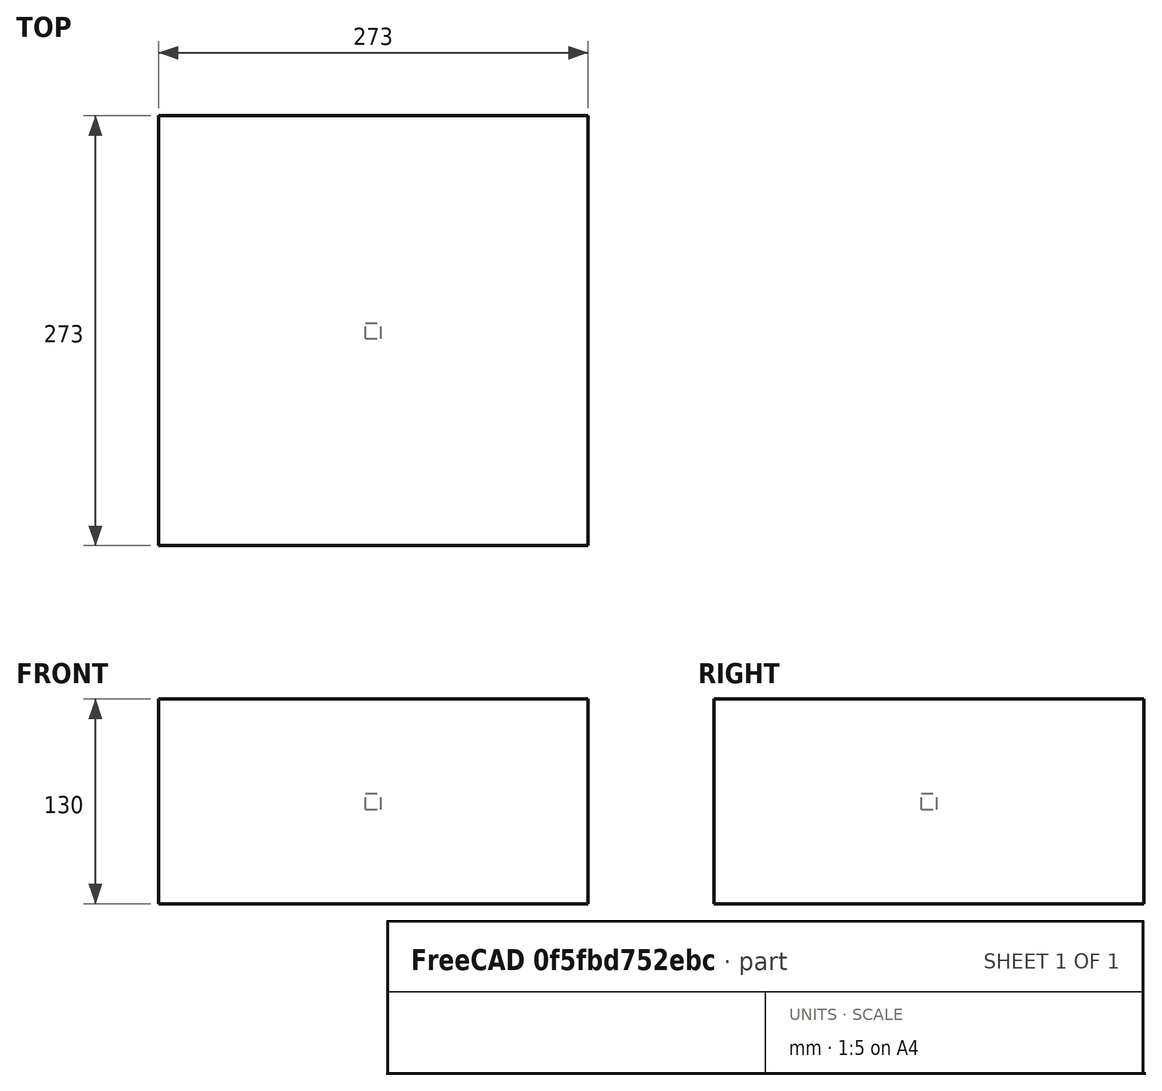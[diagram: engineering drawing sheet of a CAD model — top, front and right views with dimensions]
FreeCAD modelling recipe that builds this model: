
FCSTD DOCUMENT  (FreeCAD 0.20RUnknown)
Label: testExperiment
License: All rights reserved
LicenseURL: http://en.wikipedia.org/wiki/All_rights_reserved
objects: App::DocumentObjectGroupPython×1251, Part::FeaturePython×3, App::Part×2
note: 2 computed .brp shape members not serialized (recipe doc carries the construction recipe); baked Part::Feature solids carry a one-line shape summary decoded from their .brp

FEATURE [App::DocumentObjectGroupPython] HALFPI  # scripted group (container) (typed FeaturePython)
  name = HALFPI
  value = pi/2.
FEATURE [App::DocumentObjectGroupPython] PI  # scripted group (container) (typed FeaturePython)
  name = PI
  value = 1.*pi
FEATURE [App::DocumentObjectGroupPython] TWOPI  # scripted group (container) (typed FeaturePython)
  name = TWOPI
  value = 2.*pi
FEATURE [App::DocumentObjectGroupPython] Constants  # scripted group (container) (typed FeaturePython)
  Group = -> [HALFPI,PI,TWOPI]
FEATURE [App::DocumentObjectGroupPython] Variables  # scripted group (container) (typed FeaturePython)
FEATURE [App::DocumentObjectGroupPython] Quantities  # scripted group (container) (typed FeaturePython)
FEATURE [App::DocumentObjectGroupPython] Isotopes  # scripted group (container) (typed FeaturePython)
FEATURE [App::DocumentObjectGroupPython] Elements  # scripted group (container) (typed FeaturePython)
FEATURE [App::DocumentObjectGroupPython] Matrix  # scripted group (container) (typed FeaturePython)
FEATURE [App::DocumentObjectGroupPython] Surfaces  # scripted group (container) (typed FeaturePython)
FEATURE [App::DocumentObjectGroupPython] Opticals  # scripted group (container) (typed FeaturePython)
  Group = -> [Matrix,Surfaces]
FEATURE [App::DocumentObjectGroupPython] G4Isotopes  # scripted group (container) (typed FeaturePython)
FEATURE [App::DocumentObjectGroupPython] H_element  # scripted group (container) (typed FeaturePython)
  Z = 1
  atom_value = 1.008
  formula = H
  name = H_element
FEATURE [App::DocumentObjectGroupPython] He_element  # scripted group (container) (typed FeaturePython)
  Z = 2
  atom_value = 4.0026
  formula = He
  name = He_element
FEATURE [App::DocumentObjectGroupPython] Li_element  # scripted group (container) (typed FeaturePython)
  Z = 3
  atom_value = 6.94
  formula = Li
  name = Li_element
FEATURE [App::DocumentObjectGroupPython] Be_element  # scripted group (container) (typed FeaturePython)
  Z = 4
  atom_value = 9.01218
  formula = Be
  name = Be_element
FEATURE [App::DocumentObjectGroupPython] B_element  # scripted group (container) (typed FeaturePython)
  Z = 5
  atom_value = 10.81
  formula = B
  name = B_element
FEATURE [App::DocumentObjectGroupPython] C_element  # scripted group (container) (typed FeaturePython)
  Z = 6
  atom_value = 12.011
  formula = C
  name = C_element
FEATURE [App::DocumentObjectGroupPython] N_element  # scripted group (container) (typed FeaturePython)
  Z = 7
  atom_value = 14.007
  formula = N
  name = N_element
FEATURE [App::DocumentObjectGroupPython] O_element  # scripted group (container) (typed FeaturePython)
  Z = 8
  atom_value = 15.999
  formula = O
  name = O_element
FEATURE [App::DocumentObjectGroupPython] F_element  # scripted group (container) (typed FeaturePython)
  Z = 9
  atom_value = 18.9984
  formula = F
  name = F_element
FEATURE [App::DocumentObjectGroupPython] Ne_element  # scripted group (container) (typed FeaturePython)
  Z = 10
  atom_value = 20.1797
  formula = Ne
  name = Ne_element
FEATURE [App::DocumentObjectGroupPython] Na_element  # scripted group (container) (typed FeaturePython)
  Z = 11
  atom_value = 22.9898
  formula = Na
  name = Na_element
FEATURE [App::DocumentObjectGroupPython] Mg_element  # scripted group (container) (typed FeaturePython)
  Z = 12
  atom_value = 24.305
  formula = Mg
  name = Mg_element
FEATURE [App::DocumentObjectGroupPython] Al_element  # scripted group (container) (typed FeaturePython)
  Z = 13
  atom_value = 26.9815
  formula = Al
  name = Al_element
FEATURE [App::DocumentObjectGroupPython] Si_element  # scripted group (container) (typed FeaturePython)
  Z = 14
  atom_value = 28.085
  formula = Si
  name = Si_element
FEATURE [App::DocumentObjectGroupPython] P_element  # scripted group (container) (typed FeaturePython)
  Z = 15
  atom_value = 30.9738
  formula = P
  name = P_element
FEATURE [App::DocumentObjectGroupPython] S_element  # scripted group (container) (typed FeaturePython)
  Z = 16
  atom_value = 32.06
  formula = S
  name = S_element
FEATURE [App::DocumentObjectGroupPython] Cl_element  # scripted group (container) (typed FeaturePython)
  Z = 17
  atom_value = 35.45
  formula = Cl
  name = Cl_element
FEATURE [App::DocumentObjectGroupPython] Ar_element  # scripted group (container) (typed FeaturePython)
  Z = 18
  atom_value = 39.95
  formula = Ar
  name = Ar_element
FEATURE [App::DocumentObjectGroupPython] K_element  # scripted group (container) (typed FeaturePython)
  Z = 19
  atom_value = 39.0983
  formula = K
  name = K_element
FEATURE [App::DocumentObjectGroupPython] Ca_element  # scripted group (container) (typed FeaturePython)
  Z = 20
  atom_value = 40.078
  formula = Ca
  name = Ca_element
FEATURE [App::DocumentObjectGroupPython] Sc_element  # scripted group (container) (typed FeaturePython)
  Z = 21
  atom_value = 44.9559
  formula = Sc
  name = Sc_element
FEATURE [App::DocumentObjectGroupPython] Ti_element  # scripted group (container) (typed FeaturePython)
  Z = 22
  atom_value = 47.867
  formula = Ti
  name = Ti_element
FEATURE [App::DocumentObjectGroupPython] V_element  # scripted group (container) (typed FeaturePython)
  Z = 23
  atom_value = 50.9415
  formula = V
  name = V_element
FEATURE [App::DocumentObjectGroupPython] Cr_element  # scripted group (container) (typed FeaturePython)
  Z = 24
  atom_value = 51.9961
  formula = Cr
  name = Cr_element
FEATURE [App::DocumentObjectGroupPython] Mn_element  # scripted group (container) (typed FeaturePython)
  Z = 25
  atom_value = 54.938
  formula = Mn
  name = Mn_element
FEATURE [App::DocumentObjectGroupPython] Fe_element  # scripted group (container) (typed FeaturePython)
  Z = 26
  atom_value = 55.845
  formula = Fe
  name = Fe_element
FEATURE [App::DocumentObjectGroupPython] Co_element  # scripted group (container) (typed FeaturePython)
  Z = 27
  atom_value = 58.9332
  formula = Co
  name = Co_element
FEATURE [App::DocumentObjectGroupPython] Ni_element  # scripted group (container) (typed FeaturePython)
  Z = 28
  atom_value = 58.6934
  formula = Ni
  name = Ni_element
FEATURE [App::DocumentObjectGroupPython] Cu_element  # scripted group (container) (typed FeaturePython)
  Z = 29
  atom_value = 63.546
  formula = Cu
  name = Cu_element
FEATURE [App::DocumentObjectGroupPython] Zn_element  # scripted group (container) (typed FeaturePython)
  Z = 30
  atom_value = 65.38
  formula = Zn
  name = Zn_element
FEATURE [App::DocumentObjectGroupPython] Ga_element  # scripted group (container) (typed FeaturePython)
  Z = 31
  atom_value = 69.723
  formula = Ga
  name = Ga_element
FEATURE [App::DocumentObjectGroupPython] Ge_element  # scripted group (container) (typed FeaturePython)
  Z = 32
  atom_value = 72.63
  formula = Ge
  name = Ge_element
FEATURE [App::DocumentObjectGroupPython] As_element  # scripted group (container) (typed FeaturePython)
  Z = 33
  atom_value = 74.9216
  formula = As
  name = As_element
FEATURE [App::DocumentObjectGroupPython] Se_element  # scripted group (container) (typed FeaturePython)
  Z = 34
  atom_value = 78.971
  formula = Se
  name = Se_element
FEATURE [App::DocumentObjectGroupPython] Br_element  # scripted group (container) (typed FeaturePython)
  Z = 35
  atom_value = 79.904
  formula = Br
  name = Br_element
FEATURE [App::DocumentObjectGroupPython] Kr_element  # scripted group (container) (typed FeaturePython)
  Z = 36
  atom_value = 83.798
  formula = Kr
  name = Kr_element
FEATURE [App::DocumentObjectGroupPython] Rb_element  # scripted group (container) (typed FeaturePython)
  Z = 37
  atom_value = 85.4678
  formula = Rb
  name = Rb_element
FEATURE [App::DocumentObjectGroupPython] Sr_element  # scripted group (container) (typed FeaturePython)
  Z = 38
  atom_value = 87.62
  formula = Sr
  name = Sr_element
FEATURE [App::DocumentObjectGroupPython] Y_element  # scripted group (container) (typed FeaturePython)
  Z = 39
  atom_value = 88.9058
  formula = Y
  name = Y_element
FEATURE [App::DocumentObjectGroupPython] Zr_element  # scripted group (container) (typed FeaturePython)
  Z = 40
  atom_value = 91.224
  formula = Zr
  name = Zr_element
FEATURE [App::DocumentObjectGroupPython] Nb_element  # scripted group (container) (typed FeaturePython)
  Z = 41
  atom_value = 92.9064
  formula = Nb
  name = Nb_element
FEATURE [App::DocumentObjectGroupPython] Mo_element  # scripted group (container) (typed FeaturePython)
  Z = 42
  atom_value = 95.95
  formula = Mo
  name = Mo_element
FEATURE [App::DocumentObjectGroupPython] Tc_element  # scripted group (container) (typed FeaturePython)
  Z = 43
  atom_value = 97
  formula = Tc
  name = Tc_element
FEATURE [App::DocumentObjectGroupPython] Ru_element  # scripted group (container) (typed FeaturePython)
  Z = 44
  atom_value = 101.07
  formula = Ru
  name = Ru_element
FEATURE [App::DocumentObjectGroupPython] Rh_element  # scripted group (container) (typed FeaturePython)
  Z = 45
  atom_value = 102.905
  formula = Rh
  name = Rh_element
FEATURE [App::DocumentObjectGroupPython] Pd_element  # scripted group (container) (typed FeaturePython)
  Z = 46
  atom_value = 106.42
  formula = Pd
  name = Pd_element
FEATURE [App::DocumentObjectGroupPython] Ag_element  # scripted group (container) (typed FeaturePython)
  Z = 47
  atom_value = 107.868
  formula = Ag
  name = Ag_element
FEATURE [App::DocumentObjectGroupPython] Cd_element  # scripted group (container) (typed FeaturePython)
  Z = 48
  atom_value = 112.414
  formula = Cd
  name = Cd_element
FEATURE [App::DocumentObjectGroupPython] In_element  # scripted group (container) (typed FeaturePython)
  Z = 49
  atom_value = 114.818
  formula = In
  name = In_element
FEATURE [App::DocumentObjectGroupPython] Sn_element  # scripted group (container) (typed FeaturePython)
  Z = 50
  atom_value = 118.71
  formula = Sn
  name = Sn_element
FEATURE [App::DocumentObjectGroupPython] Sb_element  # scripted group (container) (typed FeaturePython)
  Z = 51
  atom_value = 121.76
  formula = Sb
  name = Sb_element
FEATURE [App::DocumentObjectGroupPython] Te_element  # scripted group (container) (typed FeaturePython)
  Z = 52
  atom_value = 127.6
  formula = Te
  name = Te_element
FEATURE [App::DocumentObjectGroupPython] I_element  # scripted group (container) (typed FeaturePython)
  Z = 53
  atom_value = 126.904
  formula = I
  name = I_element
FEATURE [App::DocumentObjectGroupPython] Xe_element  # scripted group (container) (typed FeaturePython)
  Z = 54
  atom_value = 131.293
  formula = Xe
  name = Xe_element
FEATURE [App::DocumentObjectGroupPython] Cs_element  # scripted group (container) (typed FeaturePython)
  Z = 55
  atom_value = 132.905
  formula = Cs
  name = Cs_element
FEATURE [App::DocumentObjectGroupPython] Ba_element  # scripted group (container) (typed FeaturePython)
  Z = 56
  atom_value = 137.327
  formula = Ba
  name = Ba_element
FEATURE [App::DocumentObjectGroupPython] La_element  # scripted group (container) (typed FeaturePython)
  Z = 57
  atom_value = 138.905
  formula = La
  name = La_element
FEATURE [App::DocumentObjectGroupPython] Ce_element  # scripted group (container) (typed FeaturePython)
  Z = 58
  atom_value = 140.116
  formula = Ce
  name = Ce_element
FEATURE [App::DocumentObjectGroupPython] Pr_element  # scripted group (container) (typed FeaturePython)
  Z = 59
  atom_value = 140.908
  formula = Pr
  name = Pr_element
FEATURE [App::DocumentObjectGroupPython] Nd_element  # scripted group (container) (typed FeaturePython)
  Z = 60
  atom_value = 144.242
  formula = Nd
  name = Nd_element
FEATURE [App::DocumentObjectGroupPython] Pm_element  # scripted group (container) (typed FeaturePython)
  Z = 61
  atom_value = 145
  formula = Pm
  name = Pm_element
FEATURE [App::DocumentObjectGroupPython] Sm_element  # scripted group (container) (typed FeaturePython)
  Z = 62
  atom_value = 150.36
  formula = Sm
  name = Sm_element
FEATURE [App::DocumentObjectGroupPython] Eu_element  # scripted group (container) (typed FeaturePython)
  Z = 63
  atom_value = 151.964
  formula = Eu
  name = Eu_element
FEATURE [App::DocumentObjectGroupPython] Gd_element  # scripted group (container) (typed FeaturePython)
  Z = 64
  atom_value = 157.25
  formula = Gd
  name = Gd_element
FEATURE [App::DocumentObjectGroupPython] Tb_element  # scripted group (container) (typed FeaturePython)
  Z = 65
  atom_value = 158.925
  formula = Tb
  name = Tb_element
FEATURE [App::DocumentObjectGroupPython] Dy_element  # scripted group (container) (typed FeaturePython)
  Z = 66
  atom_value = 162.5
  formula = Dy
  name = Dy_element
FEATURE [App::DocumentObjectGroupPython] Ho_element  # scripted group (container) (typed FeaturePython)
  Z = 67
  atom_value = 164.93
  formula = Ho
  name = Ho_element
FEATURE [App::DocumentObjectGroupPython] Er_element  # scripted group (container) (typed FeaturePython)
  Z = 68
  atom_value = 167.259
  formula = Er
  name = Er_element
FEATURE [App::DocumentObjectGroupPython] Tm_element  # scripted group (container) (typed FeaturePython)
  Z = 69
  atom_value = 168.934
  formula = Tm
  name = Tm_element
FEATURE [App::DocumentObjectGroupPython] Yb_element  # scripted group (container) (typed FeaturePython)
  Z = 70
  atom_value = 173.045
  formula = Yb
  name = Yb_element
FEATURE [App::DocumentObjectGroupPython] Lu_element  # scripted group (container) (typed FeaturePython)
  Z = 71
  atom_value = 174.967
  formula = Lu
  name = Lu_element
FEATURE [App::DocumentObjectGroupPython] Hf_element  # scripted group (container) (typed FeaturePython)
  Z = 72
  atom_value = 178.49
  formula = Hf
  name = Hf_element
FEATURE [App::DocumentObjectGroupPython] Ta_element  # scripted group (container) (typed FeaturePython)
  Z = 73
  atom_value = 180.948
  formula = Ta
  name = Ta_element
FEATURE [App::DocumentObjectGroupPython] W_element  # scripted group (container) (typed FeaturePython)
  Z = 74
  atom_value = 183.84
  formula = W
  name = W_element
FEATURE [App::DocumentObjectGroupPython] Re_element  # scripted group (container) (typed FeaturePython)
  Z = 75
  atom_value = 186.207
  formula = Re
  name = Re_element
FEATURE [App::DocumentObjectGroupPython] Os_element  # scripted group (container) (typed FeaturePython)
  Z = 76
  atom_value = 190.23
  formula = Os
  name = Os_element
FEATURE [App::DocumentObjectGroupPython] Ir_element  # scripted group (container) (typed FeaturePython)
  Z = 77
  atom_value = 192.217
  formula = Ir
  name = Ir_element
FEATURE [App::DocumentObjectGroupPython] Pt_element  # scripted group (container) (typed FeaturePython)
  Z = 78
  atom_value = 195.084
  formula = Pt
  name = Pt_element
FEATURE [App::DocumentObjectGroupPython] Au_element  # scripted group (container) (typed FeaturePython)
  Z = 79
  atom_value = 196.967
  formula = Au
  name = Au_element
FEATURE [App::DocumentObjectGroupPython] Hg_element  # scripted group (container) (typed FeaturePython)
  Z = 80
  atom_value = 200.592
  formula = Hg
  name = Hg_element
FEATURE [App::DocumentObjectGroupPython] Tl_element  # scripted group (container) (typed FeaturePython)
  Z = 81
  atom_value = 204.38
  formula = Tl
  name = Tl_element
FEATURE [App::DocumentObjectGroupPython] Pb_element  # scripted group (container) (typed FeaturePython)
  Z = 82
  atom_value = 207.2
  formula = Pb
  name = Pb_element
FEATURE [App::DocumentObjectGroupPython] Bi_element  # scripted group (container) (typed FeaturePython)
  Z = 83
  atom_value = 208.98
  formula = Bi
  name = Bi_element
FEATURE [App::DocumentObjectGroupPython] Po_element  # scripted group (container) (typed FeaturePython)
  Z = 84
  atom_value = 209
  formula = Po
  name = Po_element
FEATURE [App::DocumentObjectGroupPython] At_element  # scripted group (container) (typed FeaturePython)
  Z = 85
  atom_value = 210
  formula = At
  name = At_element
FEATURE [App::DocumentObjectGroupPython] Rn_element  # scripted group (container) (typed FeaturePython)
  Z = 86
  atom_value = 222
  formula = Rn
  name = Rn_element
FEATURE [App::DocumentObjectGroupPython] Fr_element  # scripted group (container) (typed FeaturePython)
  Z = 87
  atom_value = 223
  formula = Fr
  name = Fr_element
FEATURE [App::DocumentObjectGroupPython] Ra_element  # scripted group (container) (typed FeaturePython)
  Z = 88
  atom_value = 226
  formula = Ra
  name = Ra_element
FEATURE [App::DocumentObjectGroupPython] Ac_element  # scripted group (container) (typed FeaturePython)
  Z = 89
  atom_value = 227
  formula = Ac
  name = Ac_element
FEATURE [App::DocumentObjectGroupPython] Th_element  # scripted group (container) (typed FeaturePython)
  Z = 90
  atom_value = 232.038
  formula = Th
  name = Th_element
FEATURE [App::DocumentObjectGroupPython] Pa_element  # scripted group (container) (typed FeaturePython)
  Z = 91
  atom_value = 231.036
  formula = Pa
  name = Pa_element
FEATURE [App::DocumentObjectGroupPython] U_element  # scripted group (container) (typed FeaturePython)
  Z = 92
  atom_value = 238.029
  formula = U
  name = U_element
FEATURE [App::DocumentObjectGroupPython] Np_element  # scripted group (container) (typed FeaturePython)
  Z = 93
  atom_value = 237
  formula = Np
  name = Np_element
FEATURE [App::DocumentObjectGroupPython] Pu_element  # scripted group (container) (typed FeaturePython)
  Z = 94
  atom_value = 244
  formula = Pu
  name = Pu_element
FEATURE [App::DocumentObjectGroupPython] Am_element  # scripted group (container) (typed FeaturePython)
  Z = 95
  atom_value = 243
  formula = Am
  name = Am_element
FEATURE [App::DocumentObjectGroupPython] Cm_element  # scripted group (container) (typed FeaturePython)
  Z = 96
  atom_value = 247
  formula = Cm
  name = Cm_element
FEATURE [App::DocumentObjectGroupPython] Bk_element  # scripted group (container) (typed FeaturePython)
  Z = 97
  atom_value = 247
  formula = Bk
  name = Bk_element
FEATURE [App::DocumentObjectGroupPython] Cf_element  # scripted group (container) (typed FeaturePython)
  Z = 98
  atom_value = 251
  formula = Cf
  name = Cf_element
FEATURE [App::DocumentObjectGroupPython] G4Elements  # scripted group (container) (typed FeaturePython)
  Group = -> [H_element,He_element,Li_element,Be_element,B_element,C_element,N_element,O_element,F_element,Ne_element,Na_element,Mg_element,Al_element,Si_element,P_element,S_element,Cl_element,Ar_element,K_element,Ca_element,Sc_element,Ti_element,V_element,Cr_element,Mn_element,Fe_element,Co_element,Ni_element,Cu_element,Zn_element,Ga_element,Ge_element,As_element,Se_element,Br_element,Kr_element,Rb_element,+61 more]
FEATURE [App::DocumentObjectGroupPython] H_element001  label="H_element : 0.101"  # scripted group (container) (typed FeaturePython)
  n = 0.101327
FEATURE [App::DocumentObjectGroupPython] C_element001  label="C_element : 0.775"  # scripted group (container) (typed FeaturePython)
  n = 0.7755
FEATURE [App::DocumentObjectGroupPython] N_element001  label="N_element : 0.035"  # scripted group (container) (typed FeaturePython)
  n = 0.035057
FEATURE [App::DocumentObjectGroupPython] O_element001  label="O_element : 0.052"  # scripted group (container) (typed FeaturePython)
  n = 0.0523159
FEATURE [App::DocumentObjectGroupPython] F_element001  label="F_element : 0.017"  # scripted group (container) (typed FeaturePython)
  n = 0.017422
FEATURE [App::DocumentObjectGroupPython] Ca_element001  label="Ca_element : 0.018"  # scripted group (container) (typed FeaturePython)
  n = 0.018378
FEATURE [App::DocumentObjectGroupPython] G4_A_150_TISSUE  label="G4_A-150_TISSUE"  # scripted group (container) (typed FeaturePython)
  Dunit = g/cm3
  Dvalue = 1.127
  Group = -> [H_element001,C_element001,N_element001,O_element001,F_element001,Ca_element001]
  conduct = 2
  density = 1
  expand = 3
  formula = G4_A-150_TISSUE
  name = G4_A-150_TISSUE
  specific = 4
FEATURE [App::DocumentObjectGroupPython] C_element002  label="C_element : 3"  # scripted group (container) (typed FeaturePython)
  n = 3
  ref = C_element
FEATURE [App::DocumentObjectGroupPython] H_element002  label="H_element : 6"  # scripted group (container) (typed FeaturePython)
  n = 6
  ref = H_element
FEATURE [App::DocumentObjectGroupPython] O_element002  label="O_element : 1"  # scripted group (container) (typed FeaturePython)
  n = 1
  ref = O_element
FEATURE [App::DocumentObjectGroupPython] G4_ACETONE  # scripted group (container) (typed FeaturePython)
  Dunit = g/cm3
  Dvalue = 0.7899
  Group = -> [C_element002,H_element002,O_element002]
  conduct = 2
  density = 1
  expand = 3
  formula = G4_ACETONE
  name = G4_ACETONE
  specific = 4
FEATURE [App::DocumentObjectGroupPython] C_element003  label="C_element : 2"  # scripted group (container) (typed FeaturePython)
  n = 2
  ref = C_element
FEATURE [App::DocumentObjectGroupPython] H_element003  label="H_element : 2"  # scripted group (container) (typed FeaturePython)
  n = 2
  ref = H_element
FEATURE [App::DocumentObjectGroupPython] G4_ACETYLENE  # scripted group (container) (typed FeaturePython)
  Dunit = g/cm3
  Dvalue = 0.0010967
  Group = -> [C_element003,H_element003]
  conduct = 2
  density = 1
  expand = 3
  formula = G4_ACETYLENE
  name = G4_ACETYLENE
  specific = 4
FEATURE [App::DocumentObjectGroupPython] C_element004  label="C_element : 5"  # scripted group (container) (typed FeaturePython)
  n = 5
  ref = C_element
FEATURE [App::DocumentObjectGroupPython] H_element004  label="H_element : 5"  # scripted group (container) (typed FeaturePython)
  n = 5
  ref = H_element
FEATURE [App::DocumentObjectGroupPython] N_element002  label="N_element : 5"  # scripted group (container) (typed FeaturePython)
  n = 5
  ref = N_element
FEATURE [App::DocumentObjectGroupPython] G4_ADENINE  # scripted group (container) (typed FeaturePython)
  Dunit = g/cm3
  Dvalue = 1.6
  Group = -> [C_element004,H_element004,N_element002]
  conduct = 2
  density = 1
  expand = 3
  formula = G4_ADENINE
  name = G4_ADENINE
  specific = 4
FEATURE [App::DocumentObjectGroupPython] H_element005  label="H_element : 0.114"  # scripted group (container) (typed FeaturePython)
  n = 0.114
FEATURE [App::DocumentObjectGroupPython] C_element005  label="C_element : 0.598"  # scripted group (container) (typed FeaturePython)
  n = 0.598
FEATURE [App::DocumentObjectGroupPython] N_element003  label="N_element : 0.007"  # scripted group (container) (typed FeaturePython)
  n = 0.007
FEATURE [App::DocumentObjectGroupPython] O_element003  label="O_element : 0.278"  # scripted group (container) (typed FeaturePython)
  n = 0.278
FEATURE [App::DocumentObjectGroupPython] Na_element001  label="Na_element : 0.001"  # scripted group (container) (typed FeaturePython)
  n = 0.001
FEATURE [App::DocumentObjectGroupPython] S_element001  label="S_element : 0.001"  # scripted group (container) (typed FeaturePython)
  n = 0.001
FEATURE [App::DocumentObjectGroupPython] Cl_element001  label="Cl_element : 0.001"  # scripted group (container) (typed FeaturePython)
  n = 0.001
FEATURE [App::DocumentObjectGroupPython] G4_ADIPOSE_TISSUE_ICRP  # scripted group (container) (typed FeaturePython)
  Dunit = g/cm3
  Dvalue = 0.95
  Group = -> [H_element005,C_element005,N_element003,O_element003,Na_element001,S_element001,Cl_element001]
  conduct = 2
  density = 1
  expand = 3
  formula = G4_ADIPOSE_TISSUE_ICRP
  name = G4_ADIPOSE_TISSUE_ICRP
  specific = 4
FEATURE [App::DocumentObjectGroupPython] C_element006  label="C_element : 0.000"  # scripted group (container) (typed FeaturePython)
  n = 0.000124
FEATURE [App::DocumentObjectGroupPython] N_element004  label="N_element : 0.755"  # scripted group (container) (typed FeaturePython)
  n = 0.755268
FEATURE [App::DocumentObjectGroupPython] O_element004  label="O_element : 0.232"  # scripted group (container) (typed FeaturePython)
  n = 0.231781
FEATURE [App::DocumentObjectGroupPython] Ar_element001  label="Ar_element : 0.013"  # scripted group (container) (typed FeaturePython)
  n = 0.012827
FEATURE [App::DocumentObjectGroupPython] G4_AIR  # scripted group (container) (typed FeaturePython)
  Dunit = g/cm3
  Dvalue = 0.00120479
  Group = -> [C_element006,N_element004,O_element004,Ar_element001]
  conduct = 2
  density = 1
  expand = 3
  formula = G4_AIR
  name = G4_AIR
  specific = 4
FEATURE [App::DocumentObjectGroupPython] C_element007  label="C_element : 006"  # scripted group (container) (typed FeaturePython)
  n = 3
  ref = C_element
FEATURE [App::DocumentObjectGroupPython] H_element006  label="H_element : 7"  # scripted group (container) (typed FeaturePython)
  n = 7
  ref = H_element
FEATURE [App::DocumentObjectGroupPython] N_element005  label="N_element : 1"  # scripted group (container) (typed FeaturePython)
  n = 1
  ref = N_element
FEATURE [App::DocumentObjectGroupPython] O_element005  label="O_element : 2"  # scripted group (container) (typed FeaturePython)
  n = 2
  ref = O_element
FEATURE [App::DocumentObjectGroupPython] G4_ALANINE  # scripted group (container) (typed FeaturePython)
  Dunit = g/cm3
  Dvalue = 1.42
  Group = -> [C_element007,H_element006,N_element005,O_element005]
  conduct = 2
  density = 1
  expand = 3
  formula = G4_ALANINE
  name = G4_ALANINE
  specific = 4
FEATURE [App::DocumentObjectGroupPython] Al_element001  label="Al_element : 2"  # scripted group (container) (typed FeaturePython)
  n = 2
  ref = Al_element
FEATURE [App::DocumentObjectGroupPython] O_element006  label="O_element : 3"  # scripted group (container) (typed FeaturePython)
  n = 3
  ref = O_element
FEATURE [App::DocumentObjectGroupPython] G4_ALUMINUM_OXIDE  # scripted group (container) (typed FeaturePython)
  Dunit = g/cm3
  Dvalue = 3.97
  Group = -> [Al_element001,O_element006]
  conduct = 2
  density = 1
  expand = 3
  formula = G4_ALUMINUM_OXIDE
  name = G4_ALUMINUM_OXIDE
  specific = 4
FEATURE [App::DocumentObjectGroupPython] H_element007  label="H_element : 0.106"  # scripted group (container) (typed FeaturePython)
  n = 0.10593
FEATURE [App::DocumentObjectGroupPython] C_element008  label="C_element : 0.789"  # scripted group (container) (typed FeaturePython)
  n = 0.788974
FEATURE [App::DocumentObjectGroupPython] O_element007  label="O_element : 0.105"  # scripted group (container) (typed FeaturePython)
  n = 0.105096
FEATURE [App::DocumentObjectGroupPython] G4_AMBER  # scripted group (container) (typed FeaturePython)
  Dunit = g/cm3
  Dvalue = 1.1
  Group = -> [H_element007,C_element008,O_element007]
  conduct = 2
  density = 1
  expand = 3
  formula = G4_AMBER
  name = G4_AMBER
  specific = 4
FEATURE [App::DocumentObjectGroupPython] N_element006  label="N_element : 006"  # scripted group (container) (typed FeaturePython)
  n = 1
  ref = N_element
FEATURE [App::DocumentObjectGroupPython] H_element008  label="H_element : 3"  # scripted group (container) (typed FeaturePython)
  n = 3
  ref = H_element
FEATURE [App::DocumentObjectGroupPython] G4_AMMONIA  # scripted group (container) (typed FeaturePython)
  Dunit = g/cm3
  Dvalue = 0.000826019
  Group = -> [N_element006,H_element008]
  conduct = 2
  density = 1
  expand = 3
  formula = G4_AMMONIA
  name = G4_AMMONIA
  specific = 4
FEATURE [App::DocumentObjectGroupPython] C_element009  label="C_element : 6"  # scripted group (container) (typed FeaturePython)
  n = 6
  ref = C_element
FEATURE [App::DocumentObjectGroupPython] H_element009  label="H_element : 008"  # scripted group (container) (typed FeaturePython)
  n = 7
  ref = H_element
FEATURE [App::DocumentObjectGroupPython] N_element007  label="N_element : 007"  # scripted group (container) (typed FeaturePython)
  n = 1
  ref = N_element
FEATURE [App::DocumentObjectGroupPython] G4_ANILINE  # scripted group (container) (typed FeaturePython)
  Dunit = g/cm3
  Dvalue = 1.0235
  Group = -> [C_element009,H_element009,N_element007]
  conduct = 2
  density = 1
  expand = 3
  formula = G4_ANILINE
  name = G4_ANILINE
  specific = 4
FEATURE [App::DocumentObjectGroupPython] C_element010  label="C_element : 14"  # scripted group (container) (typed FeaturePython)
  n = 14
  ref = C_element
FEATURE [App::DocumentObjectGroupPython] H_element010  label="H_element : 10"  # scripted group (container) (typed FeaturePython)
  n = 10
  ref = H_element
FEATURE [App::DocumentObjectGroupPython] G4_ANTHRACENE  # scripted group (container) (typed FeaturePython)
  Dunit = g/cm3
  Dvalue = 1.283
  Group = -> [C_element010,H_element010]
  conduct = 2
  density = 1
  expand = 3
  formula = G4_ANTHRACENE
  name = G4_ANTHRACENE
  specific = 4
FEATURE [App::DocumentObjectGroupPython] H_element011  label="H_element : 0.065"  # scripted group (container) (typed FeaturePython)
  n = 0.0654709
FEATURE [App::DocumentObjectGroupPython] C_element011  label="C_element : 0.537"  # scripted group (container) (typed FeaturePython)
  n = 0.536944
FEATURE [App::DocumentObjectGroupPython] N_element008  label="N_element : 0.021"  # scripted group (container) (typed FeaturePython)
  n = 0.0215
FEATURE [App::DocumentObjectGroupPython] O_element008  label="O_element : 0.032"  # scripted group (container) (typed FeaturePython)
  n = 0.032085
FEATURE [App::DocumentObjectGroupPython] F_element002  label="F_element : 0.167"  # scripted group (container) (typed FeaturePython)
  n = 0.167411
FEATURE [App::DocumentObjectGroupPython] Ca_element002  label="Ca_element : 0.177"  # scripted group (container) (typed FeaturePython)
  n = 0.176589
FEATURE [App::DocumentObjectGroupPython] G4_B_100_BONE  label="G4_B-100_BONE"  # scripted group (container) (typed FeaturePython)
  Dunit = g/cm3
  Dvalue = 1.45
  Group = -> [H_element011,C_element011,N_element008,O_element008,F_element002,Ca_element002]
  conduct = 2
  density = 1
  expand = 3
  formula = G4_B-100_BONE
  name = G4_B-100_BONE
  specific = 4
FEATURE [App::DocumentObjectGroupPython] H_element012  label="H_element : 0.057"  # scripted group (container) (typed FeaturePython)
  n = 0.057441
FEATURE [App::DocumentObjectGroupPython] C_element012  label="C_element : 0.790"  # scripted group (container) (typed FeaturePython)
  n = 0.774591
FEATURE [App::DocumentObjectGroupPython] O_element009  label="O_element : 0.168"  # scripted group (container) (typed FeaturePython)
  n = 0.167968
FEATURE [App::DocumentObjectGroupPython] G4_BAKELITE  # scripted group (container) (typed FeaturePython)
  Dunit = g/cm3
  Dvalue = 1.25
  Group = -> [H_element012,C_element012,O_element009]
  conduct = 2
  density = 1
  expand = 3
  formula = G4_BAKELITE
  name = G4_BAKELITE
  specific = 4
FEATURE [App::DocumentObjectGroupPython] Ba_element001  label="Ba_element : 1"  # scripted group (container) (typed FeaturePython)
  n = 1
  ref = Ba_element
FEATURE [App::DocumentObjectGroupPython] F_element003  label="F_element : 2"  # scripted group (container) (typed FeaturePython)
  n = 2
  ref = F_element
FEATURE [App::DocumentObjectGroupPython] G4_BARIUM_FLUORIDE  # scripted group (container) (typed FeaturePython)
  Dunit = g/cm3
  Dvalue = 4.89
  Group = -> [Ba_element001,F_element003]
  conduct = 2
  density = 1
  expand = 3
  formula = G4_BARIUM_FLUORIDE
  name = G4_BARIUM_FLUORIDE
  specific = 4
FEATURE [App::DocumentObjectGroupPython] Ba_element002  label="Ba_element : 002"  # scripted group (container) (typed FeaturePython)
  n = 1
  ref = Ba_element
FEATURE [App::DocumentObjectGroupPython] S_element002  label="S_element : 1"  # scripted group (container) (typed FeaturePython)
  n = 1
  ref = S_element
FEATURE [App::DocumentObjectGroupPython] O_element010  label="O_element : 4"  # scripted group (container) (typed FeaturePython)
  n = 4
  ref = O_element
FEATURE [App::DocumentObjectGroupPython] G4_BARIUM_SULFATE  # scripted group (container) (typed FeaturePython)
  Dunit = g/cm3
  Dvalue = 4.5
  Group = -> [Ba_element002,S_element002,O_element010]
  conduct = 2
  density = 1
  expand = 3
  formula = G4_BARIUM_SULFATE
  name = G4_BARIUM_SULFATE
  specific = 4
FEATURE [App::DocumentObjectGroupPython] C_element013  label="C_element : 007"  # scripted group (container) (typed FeaturePython)
  n = 6
  ref = C_element
FEATURE [App::DocumentObjectGroupPython] H_element013  label="H_element : 009"  # scripted group (container) (typed FeaturePython)
  n = 6
  ref = H_element
FEATURE [App::DocumentObjectGroupPython] G4_BENZENE  # scripted group (container) (typed FeaturePython)
  Dunit = g/cm3
  Dvalue = 0.87865
  Group = -> [C_element013,H_element013]
  conduct = 2
  density = 1
  expand = 3
  formula = G4_BENZENE
  name = G4_BENZENE
  specific = 4
FEATURE [App::DocumentObjectGroupPython] Be_element001  label="Be_element : 1"  # scripted group (container) (typed FeaturePython)
  n = 1
  ref = Be_element
FEATURE [App::DocumentObjectGroupPython] O_element011  label="O_element : 005"  # scripted group (container) (typed FeaturePython)
  n = 1
  ref = O_element
FEATURE [App::DocumentObjectGroupPython] G4_BERYLLIUM_OXIDE  # scripted group (container) (typed FeaturePython)
  Dunit = g/cm3
  Dvalue = 3.01
  Group = -> [Be_element001,O_element011]
  conduct = 2
  density = 1
  expand = 3
  formula = G4_BERYLLIUM_OXIDE
  name = G4_BERYLLIUM_OXIDE
  specific = 4
FEATURE [App::DocumentObjectGroupPython] Bi_element001  label="Bi_element : 4"  # scripted group (container) (typed FeaturePython)
  n = 4
  ref = Bi_element
FEATURE [App::DocumentObjectGroupPython] Ge_element001  label="Ge_element : 3"  # scripted group (container) (typed FeaturePython)
  n = 3
  ref = Ge_element
FEATURE [App::DocumentObjectGroupPython] O_element012  label="O_element : 12"  # scripted group (container) (typed FeaturePython)
  n = 12
  ref = O_element
FEATURE [App::DocumentObjectGroupPython] G4_BGO  # scripted group (container) (typed FeaturePython)
  Dunit = g/cm3
  Dvalue = 7.13
  Group = -> [Bi_element001,Ge_element001,O_element012]
  conduct = 2
  density = 1
  expand = 3
  formula = G4_BGO
  name = G4_BGO
  specific = 4
FEATURE [App::DocumentObjectGroupPython] H_element014  label="H_element : 0.102"  # scripted group (container) (typed FeaturePython)
  n = 0.102
FEATURE [App::DocumentObjectGroupPython] C_element014  label="C_element : 0.110"  # scripted group (container) (typed FeaturePython)
  n = 0.11
FEATURE [App::DocumentObjectGroupPython] N_element009  label="N_element : 0.033"  # scripted group (container) (typed FeaturePython)
  n = 0.033
FEATURE [App::DocumentObjectGroupPython] O_element013  label="O_element : 0.745"  # scripted group (container) (typed FeaturePython)
  n = 0.745
FEATURE [App::DocumentObjectGroupPython] Na_element002  label="Na_element : 0.002"  # scripted group (container) (typed FeaturePython)
  n = 0.001
FEATURE [App::DocumentObjectGroupPython] P_element001  label="P_element : 0.001"  # scripted group (container) (typed FeaturePython)
  n = 0.001
FEATURE [App::DocumentObjectGroupPython] S_element003  label="S_element : 0.002"  # scripted group (container) (typed FeaturePython)
  n = 0.002
FEATURE [App::DocumentObjectGroupPython] Cl_element002  label="Cl_element : 0.003"  # scripted group (container) (typed FeaturePython)
  n = 0.003
FEATURE [App::DocumentObjectGroupPython] K_element001  label="K_element : 0.002"  # scripted group (container) (typed FeaturePython)
  n = 0.002
FEATURE [App::DocumentObjectGroupPython] Fe_element001  label="Fe_element : 0.001"  # scripted group (container) (typed FeaturePython)
  n = 0.001
FEATURE [App::DocumentObjectGroupPython] G4_BLOOD_ICRP  # scripted group (container) (typed FeaturePython)
  Dunit = g/cm3
  Dvalue = 1.06
  Group = -> [H_element014,C_element014,N_element009,O_element013,Na_element002,P_element001,S_element003,Cl_element002,K_element001,Fe_element001]
  conduct = 2
  density = 1
  expand = 3
  formula = G4_BLOOD_ICRP
  name = G4_BLOOD_ICRP
  specific = 4
FEATURE [App::DocumentObjectGroupPython] H_element015  label="H_element : 0.064"  # scripted group (container) (typed FeaturePython)
  n = 0.064
FEATURE [App::DocumentObjectGroupPython] C_element015  label="C_element : 0.278"  # scripted group (container) (typed FeaturePython)
  n = 0.278
FEATURE [App::DocumentObjectGroupPython] N_element010  label="N_element : 0.027"  # scripted group (container) (typed FeaturePython)
  n = 0.027
FEATURE [App::DocumentObjectGroupPython] O_element014  label="O_element : 0.410"  # scripted group (container) (typed FeaturePython)
  n = 0.41
FEATURE [App::DocumentObjectGroupPython] Mg_element001  label="Mg_element : 0.002"  # scripted group (container) (typed FeaturePython)
  n = 0.002
FEATURE [App::DocumentObjectGroupPython] P_element002  label="P_element : 0.070"  # scripted group (container) (typed FeaturePython)
  n = 0.07
FEATURE [App::DocumentObjectGroupPython] S_element004  label="S_element : 0.003"  # scripted group (container) (typed FeaturePython)
  n = 0.002
FEATURE [App::DocumentObjectGroupPython] Ca_element003  label="Ca_element : 0.147"  # scripted group (container) (typed FeaturePython)
  n = 0.147
FEATURE [App::DocumentObjectGroupPython] G4_BONE_COMPACT_ICRU  # scripted group (container) (typed FeaturePython)
  Dunit = g/cm3
  Dvalue = 1.85
  Group = -> [H_element015,C_element015,N_element010,O_element014,Mg_element001,P_element002,S_element004,Ca_element003]
  conduct = 2
  density = 1
  expand = 3
  formula = G4_BONE_COMPACT_ICRU
  name = G4_BONE_COMPACT_ICRU
  specific = 4
FEATURE [App::DocumentObjectGroupPython] H_element016  label="H_element : 0.034"  # scripted group (container) (typed FeaturePython)
  n = 0.034
FEATURE [App::DocumentObjectGroupPython] C_element016  label="C_element : 0.155"  # scripted group (container) (typed FeaturePython)
  n = 0.155
FEATURE [App::DocumentObjectGroupPython] N_element011  label="N_element : 0.042"  # scripted group (container) (typed FeaturePython)
  n = 0.042
FEATURE [App::DocumentObjectGroupPython] O_element015  label="O_element : 0.435"  # scripted group (container) (typed FeaturePython)
  n = 0.435
FEATURE [App::DocumentObjectGroupPython] Na_element003  label="Na_element : 0.003"  # scripted group (container) (typed FeaturePython)
  n = 0.001
FEATURE [App::DocumentObjectGroupPython] Mg_element002  label="Mg_element : 0.003"  # scripted group (container) (typed FeaturePython)
  n = 0.002
FEATURE [App::DocumentObjectGroupPython] P_element003  label="P_element : 0.103"  # scripted group (container) (typed FeaturePython)
  n = 0.103
FEATURE [App::DocumentObjectGroupPython] S_element005  label="S_element : 0.004"  # scripted group (container) (typed FeaturePython)
  n = 0.003
FEATURE [App::DocumentObjectGroupPython] Ca_element004  label="Ca_element : 0.225"  # scripted group (container) (typed FeaturePython)
  n = 0.225
FEATURE [App::DocumentObjectGroupPython] G4_BONE_CORTICAL_ICRP  # scripted group (container) (typed FeaturePython)
  Dunit = g/cm3
  Dvalue = 1.92
  Group = -> [H_element016,C_element016,N_element011,O_element015,Na_element003,Mg_element002,P_element003,S_element005,Ca_element004]
  conduct = 2
  density = 1
  expand = 3
  formula = G4_BONE_CORTICAL_ICRP
  name = G4_BONE_CORTICAL_ICRP
  specific = 4
FEATURE [App::DocumentObjectGroupPython] B_element001  label="B_element : 4"  # scripted group (container) (typed FeaturePython)
  n = 4
  ref = B_element
FEATURE [App::DocumentObjectGroupPython] C_element017  label="C_element : 1"  # scripted group (container) (typed FeaturePython)
  n = 1
  ref = C_element
FEATURE [App::DocumentObjectGroupPython] G4_BORON_CARBIDE  # scripted group (container) (typed FeaturePython)
  Dunit = g/cm3
  Dvalue = 2.52
  Group = -> [B_element001,C_element017]
  conduct = 2
  density = 1
  expand = 3
  formula = G4_BORON_CARBIDE
  name = G4_BORON_CARBIDE
  specific = 4
FEATURE [App::DocumentObjectGroupPython] B_element002  label="B_element : 2"  # scripted group (container) (typed FeaturePython)
  n = 2
  ref = B_element
FEATURE [App::DocumentObjectGroupPython] O_element016  label="O_element : 006"  # scripted group (container) (typed FeaturePython)
  n = 3
  ref = O_element
FEATURE [App::DocumentObjectGroupPython] G4_BORON_OXIDE  # scripted group (container) (typed FeaturePython)
  Dunit = g/cm3
  Dvalue = 1.812
  Group = -> [B_element002,O_element016]
  conduct = 2
  density = 1
  expand = 3
  formula = G4_BORON_OXIDE
  name = G4_BORON_OXIDE
  specific = 4
FEATURE [App::DocumentObjectGroupPython] H_element017  label="H_element : 0.107"  # scripted group (container) (typed FeaturePython)
  n = 0.107
FEATURE [App::DocumentObjectGroupPython] C_element018  label="C_element : 0.145"  # scripted group (container) (typed FeaturePython)
  n = 0.145
FEATURE [App::DocumentObjectGroupPython] N_element012  label="N_element : 0.022"  # scripted group (container) (typed FeaturePython)
  n = 0.022
FEATURE [App::DocumentObjectGroupPython] O_element017  label="O_element : 0.712"  # scripted group (container) (typed FeaturePython)
  n = 0.712
FEATURE [App::DocumentObjectGroupPython] Na_element004  label="Na_element : 0.004"  # scripted group (container) (typed FeaturePython)
  n = 0.002
FEATURE [App::DocumentObjectGroupPython] P_element004  label="P_element : 0.004"  # scripted group (container) (typed FeaturePython)
  n = 0.004
FEATURE [App::DocumentObjectGroupPython] S_element006  label="S_element : 0.005"  # scripted group (container) (typed FeaturePython)
  n = 0.002
FEATURE [App::DocumentObjectGroupPython] Cl_element003  label="Cl_element : 0.004"  # scripted group (container) (typed FeaturePython)
  n = 0.003
FEATURE [App::DocumentObjectGroupPython] K_element002  label="K_element : 0.003"  # scripted group (container) (typed FeaturePython)
  n = 0.003
FEATURE [App::DocumentObjectGroupPython] G4_BRAIN_ICRP  # scripted group (container) (typed FeaturePython)
  Dunit = g/cm3
  Dvalue = 1.04
  Group = -> [H_element017,C_element018,N_element012,O_element017,Na_element004,P_element004,S_element006,Cl_element003,K_element002]
  conduct = 2
  density = 1
  expand = 3
  formula = G4_BRAIN_ICRP
  name = G4_BRAIN_ICRP
  specific = 4
FEATURE [App::DocumentObjectGroupPython] C_element019  label="C_element : 4"  # scripted group (container) (typed FeaturePython)
  n = 4
  ref = C_element
FEATURE [App::DocumentObjectGroupPython] H_element018  label="H_element : 010"  # scripted group (container) (typed FeaturePython)
  n = 10
  ref = H_element
FEATURE [App::DocumentObjectGroupPython] G4_BUTANE  # scripted group (container) (typed FeaturePython)
  Dunit = g/cm3
  Dvalue = 0.00249343
  Group = -> [C_element019,H_element018]
  conduct = 2
  density = 1
  expand = 3
  formula = G4_BUTANE
  name = G4_BUTANE
  specific = 4
FEATURE [App::DocumentObjectGroupPython] C_element020  label="C_element : 008"  # scripted group (container) (typed FeaturePython)
  n = 4
  ref = C_element
FEATURE [App::DocumentObjectGroupPython] H_element019  label="H_element : 011"  # scripted group (container) (typed FeaturePython)
  n = 10
  ref = H_element
FEATURE [App::DocumentObjectGroupPython] O_element018  label="O_element : 007"  # scripted group (container) (typed FeaturePython)
  n = 1
  ref = O_element
FEATURE [App::DocumentObjectGroupPython] G4_N_BUTYL_ALCOHOL  label="G4_N-BUTYL_ALCOHOL"  # scripted group (container) (typed FeaturePython)
  Dunit = g/cm3
  Dvalue = 0.8098
  Group = -> [C_element020,H_element019,O_element018]
  conduct = 2
  density = 1
  expand = 3
  formula = G4_N-BUTYL_ALCOHOL
  name = G4_N-BUTYL_ALCOHOL
  specific = 4
FEATURE [App::DocumentObjectGroupPython] H_element020  label="H_element : 0.025"  # scripted group (container) (typed FeaturePython)
  n = 0.02468
FEATURE [App::DocumentObjectGroupPython] C_element021  label="C_element : 0.502"  # scripted group (container) (typed FeaturePython)
  n = 0.501611
FEATURE [App::DocumentObjectGroupPython] O_element019  label="O_element : 0.005"  # scripted group (container) (typed FeaturePython)
  n = 0.004527
FEATURE [App::DocumentObjectGroupPython] F_element004  label="F_element : 0.465"  # scripted group (container) (typed FeaturePython)
  n = 0.465209
FEATURE [App::DocumentObjectGroupPython] Si_element001  label="Si_element : 0.004"  # scripted group (container) (typed FeaturePython)
  n = 0.003973
FEATURE [App::DocumentObjectGroupPython] G4_C_552  label="G4_C-552"  # scripted group (container) (typed FeaturePython)
  Dunit = g/cm3
  Dvalue = 1.76
  Group = -> [H_element020,C_element021,O_element019,F_element004,Si_element001]
  conduct = 2
  density = 1
  expand = 3
  formula = G4_C-552
  name = G4_C-552
  specific = 4
FEATURE [App::DocumentObjectGroupPython] Cd_element001  label="Cd_element : 1"  # scripted group (container) (typed FeaturePython)
  n = 1
  ref = Cd_element
FEATURE [App::DocumentObjectGroupPython] Te_element001  label="Te_element : 1"  # scripted group (container) (typed FeaturePython)
  n = 1
  ref = Te_element
FEATURE [App::DocumentObjectGroupPython] G4_CADMIUM_TELLURIDE  # scripted group (container) (typed FeaturePython)
  Dunit = g/cm3
  Dvalue = 6.2
  Group = -> [Cd_element001,Te_element001]
  conduct = 2
  density = 1
  expand = 3
  formula = G4_CADMIUM_TELLURIDE
  name = G4_CADMIUM_TELLURIDE
  specific = 4
FEATURE [App::DocumentObjectGroupPython] Cd_element002  label="Cd_element : 002"  # scripted group (container) (typed FeaturePython)
  n = 1
  ref = Cd_element
FEATURE [App::DocumentObjectGroupPython] W_element001  label="W_element : 1"  # scripted group (container) (typed FeaturePython)
  n = 1
  ref = W_element
FEATURE [App::DocumentObjectGroupPython] O_element020  label="O_element : 008"  # scripted group (container) (typed FeaturePython)
  n = 4
  ref = O_element
FEATURE [App::DocumentObjectGroupPython] G4_CADMIUM_TUNGSTATE  # scripted group (container) (typed FeaturePython)
  Dunit = g/cm3
  Dvalue = 7.9
  Group = -> [Cd_element002,W_element001,O_element020]
  conduct = 2
  density = 1
  expand = 3
  formula = G4_CADMIUM_TUNGSTATE
  name = G4_CADMIUM_TUNGSTATE
  specific = 4
FEATURE [App::DocumentObjectGroupPython] Ca_element005  label="Ca_element : 1"  # scripted group (container) (typed FeaturePython)
  n = 1
  ref = Ca_element
FEATURE [App::DocumentObjectGroupPython] C_element022  label="C_element : 009"  # scripted group (container) (typed FeaturePython)
  n = 1
  ref = C_element
FEATURE [App::DocumentObjectGroupPython] O_element021  label="O_element : 009"  # scripted group (container) (typed FeaturePython)
  n = 3
  ref = O_element
FEATURE [App::DocumentObjectGroupPython] G4_CALCIUM_CARBONATE  # scripted group (container) (typed FeaturePython)
  Dunit = g/cm3
  Dvalue = 2.8
  Group = -> [Ca_element005,C_element022,O_element021]
  conduct = 2
  density = 1
  expand = 3
  formula = G4_CALCIUM_CARBONATE
  name = G4_CALCIUM_CARBONATE
  specific = 4
FEATURE [App::DocumentObjectGroupPython] Ca_element006  label="Ca_element : 002"  # scripted group (container) (typed FeaturePython)
  n = 1
  ref = Ca_element
FEATURE [App::DocumentObjectGroupPython] F_element005  label="F_element : 003"  # scripted group (container) (typed FeaturePython)
  n = 2
  ref = F_element
FEATURE [App::DocumentObjectGroupPython] G4_CALCIUM_FLUORIDE  # scripted group (container) (typed FeaturePython)
  Dunit = g/cm3
  Dvalue = 3.18
  Group = -> [Ca_element006,F_element005]
  conduct = 2
  density = 1
  expand = 3
  formula = G4_CALCIUM_FLUORIDE
  name = G4_CALCIUM_FLUORIDE
  specific = 4
FEATURE [App::DocumentObjectGroupPython] Ca_element007  label="Ca_element : 003"  # scripted group (container) (typed FeaturePython)
  n = 1
  ref = Ca_element
FEATURE [App::DocumentObjectGroupPython] O_element022  label="O_element : 010"  # scripted group (container) (typed FeaturePython)
  n = 1
  ref = O_element
FEATURE [App::DocumentObjectGroupPython] G4_CALCIUM_OXIDE  # scripted group (container) (typed FeaturePython)
  Dunit = g/cm3
  Dvalue = 3.3
  Group = -> [Ca_element007,O_element022]
  conduct = 2
  density = 1
  expand = 3
  formula = G4_CALCIUM_OXIDE
  name = G4_CALCIUM_OXIDE
  specific = 4
FEATURE [App::DocumentObjectGroupPython] Ca_element008  label="Ca_element : 004"  # scripted group (container) (typed FeaturePython)
  n = 1
  ref = Ca_element
FEATURE [App::DocumentObjectGroupPython] S_element007  label="S_element : 002"  # scripted group (container) (typed FeaturePython)
  n = 1
  ref = S_element
FEATURE [App::DocumentObjectGroupPython] O_element023  label="O_element : 011"  # scripted group (container) (typed FeaturePython)
  n = 4
  ref = O_element
FEATURE [App::DocumentObjectGroupPython] G4_CALCIUM_SULFATE  # scripted group (container) (typed FeaturePython)
  Dunit = g/cm3
  Dvalue = 2.96
  Group = -> [Ca_element008,S_element007,O_element023]
  conduct = 2
  density = 1
  expand = 3
  formula = G4_CALCIUM_SULFATE
  name = G4_CALCIUM_SULFATE
  specific = 4
FEATURE [App::DocumentObjectGroupPython] Ca_element009  label="Ca_element : 005"  # scripted group (container) (typed FeaturePython)
  n = 1
  ref = Ca_element
FEATURE [App::DocumentObjectGroupPython] W_element002  label="W_element : 002"  # scripted group (container) (typed FeaturePython)
  n = 1
  ref = W_element
FEATURE [App::DocumentObjectGroupPython] O_element024  label="O_element : 012"  # scripted group (container) (typed FeaturePython)
  n = 4
  ref = O_element
FEATURE [App::DocumentObjectGroupPython] G4_CALCIUM_TUNGSTATE  # scripted group (container) (typed FeaturePython)
  Dunit = g/cm3
  Dvalue = 6.062
  Group = -> [Ca_element009,W_element002,O_element024]
  conduct = 2
  density = 1
  expand = 3
  formula = G4_CALCIUM_TUNGSTATE
  name = G4_CALCIUM_TUNGSTATE
  specific = 4
FEATURE [App::DocumentObjectGroupPython] C_element023  label="C_element : 010"  # scripted group (container) (typed FeaturePython)
  n = 1
  ref = C_element
FEATURE [App::DocumentObjectGroupPython] O_element025  label="O_element : 013"  # scripted group (container) (typed FeaturePython)
  n = 2
  ref = O_element
FEATURE [App::DocumentObjectGroupPython] G4_CARBON_DIOXIDE  # scripted group (container) (typed FeaturePython)
  Dunit = g/cm3
  Dvalue = 0.00184212
  Group = -> [C_element023,O_element025]
  conduct = 2
  density = 1
  expand = 3
  formula = G4_CARBON_DIOXIDE
  name = G4_CARBON_DIOXIDE
  specific = 4
FEATURE [App::DocumentObjectGroupPython] C_element024  label="C_element : 011"  # scripted group (container) (typed FeaturePython)
  n = 1
  ref = C_element
FEATURE [App::DocumentObjectGroupPython] Cl_element004  label="Cl_element : 4"  # scripted group (container) (typed FeaturePython)
  n = 4
  ref = Cl_element
FEATURE [App::DocumentObjectGroupPython] G4_CARBON_TETRACHLORIDE  # scripted group (container) (typed FeaturePython)
  Dunit = g/cm3
  Dvalue = 1.594
  Group = -> [C_element024,Cl_element004]
  conduct = 2
  density = 1
  expand = 3
  formula = G4_CARBON_TETRACHLORIDE
  name = G4_CARBON_TETRACHLORIDE
  specific = 4
FEATURE [App::DocumentObjectGroupPython] C_element025  label="C_element : 012"  # scripted group (container) (typed FeaturePython)
  n = 6
  ref = C_element
FEATURE [App::DocumentObjectGroupPython] H_element021  label="H_element : 012"  # scripted group (container) (typed FeaturePython)
  n = 10
  ref = H_element
FEATURE [App::DocumentObjectGroupPython] O_element026  label="O_element : 5"  # scripted group (container) (typed FeaturePython)
  n = 5
  ref = O_element
FEATURE [App::DocumentObjectGroupPython] G4_CELLULOSE_CELLOPHANE  # scripted group (container) (typed FeaturePython)
  Dunit = g/cm3
  Dvalue = 1.42
  Group = -> [C_element025,H_element021,O_element026]
  conduct = 2
  density = 1
  expand = 3
  formula = G4_CELLULOSE_CELLOPHANE
  name = G4_CELLULOSE_CELLOPHANE
  specific = 4
FEATURE [App::DocumentObjectGroupPython] H_element022  label="H_element : 0.067"  # scripted group (container) (typed FeaturePython)
  n = 0.067125
FEATURE [App::DocumentObjectGroupPython] C_element026  label="C_element : 0.545"  # scripted group (container) (typed FeaturePython)
  n = 0.545403
FEATURE [App::DocumentObjectGroupPython] O_element027  label="O_element : 0.387"  # scripted group (container) (typed FeaturePython)
  n = 0.387472
FEATURE [App::DocumentObjectGroupPython] G4_CELLULOSE_BUTYRATE  # scripted group (container) (typed FeaturePython)
  Dunit = g/cm3
  Dvalue = 1.2
  Group = -> [H_element022,C_element026,O_element027]
  conduct = 2
  density = 1
  expand = 3
  formula = G4_CELLULOSE_BUTYRATE
  name = G4_CELLULOSE_BUTYRATE
  specific = 4
FEATURE [App::DocumentObjectGroupPython] H_element023  label="H_element : 0.029"  # scripted group (container) (typed FeaturePython)
  n = 0.029216
FEATURE [App::DocumentObjectGroupPython] C_element027  label="C_element : 0.271"  # scripted group (container) (typed FeaturePython)
  n = 0.271296
FEATURE [App::DocumentObjectGroupPython] N_element013  label="N_element : 0.121"  # scripted group (container) (typed FeaturePython)
  n = 0.121276
FEATURE [App::DocumentObjectGroupPython] O_element028  label="O_element : 0.578"  # scripted group (container) (typed FeaturePython)
  n = 0.578212
FEATURE [App::DocumentObjectGroupPython] G4_CELLULOSE_NITRATE  # scripted group (container) (typed FeaturePython)
  Dunit = g/cm3
  Dvalue = 1.49
  Group = -> [H_element023,C_element027,N_element013,O_element028]
  conduct = 2
  density = 1
  expand = 3
  formula = G4_CELLULOSE_NITRATE
  name = G4_CELLULOSE_NITRATE
  specific = 4
FEATURE [App::DocumentObjectGroupPython] H_element024  label="H_element : 0.108"  # scripted group (container) (typed FeaturePython)
  n = 0.107596
FEATURE [App::DocumentObjectGroupPython] N_element014  label="N_element : 0.001"  # scripted group (container) (typed FeaturePython)
  n = 0.0008
FEATURE [App::DocumentObjectGroupPython] O_element029  label="O_element : 0.875"  # scripted group (container) (typed FeaturePython)
  n = 0.874976
FEATURE [App::DocumentObjectGroupPython] S_element008  label="S_element : 0.015"  # scripted group (container) (typed FeaturePython)
  n = 0.014627
FEATURE [App::DocumentObjectGroupPython] Ce_element001  label="Ce_element : 0.002"  # scripted group (container) (typed FeaturePython)
  n = 0.002001
FEATURE [App::DocumentObjectGroupPython] G4_CERIC_SULFATE  # scripted group (container) (typed FeaturePython)
  Dunit = g/cm3
  Dvalue = 1.03
  Group = -> [H_element024,N_element014,O_element029,S_element008,Ce_element001]
  conduct = 2
  density = 1
  expand = 3
  formula = G4_CERIC_SULFATE
  name = G4_CERIC_SULFATE
  specific = 4
FEATURE [App::DocumentObjectGroupPython] Cs_element001  label="Cs_element : 1"  # scripted group (container) (typed FeaturePython)
  n = 1
  ref = Cs_element
FEATURE [App::DocumentObjectGroupPython] F_element006  label="F_element : 1"  # scripted group (container) (typed FeaturePython)
  n = 1
  ref = F_element
FEATURE [App::DocumentObjectGroupPython] G4_CESIUM_FLUORIDE  # scripted group (container) (typed FeaturePython)
  Dunit = g/cm3
  Dvalue = 4.115
  Group = -> [Cs_element001,F_element006]
  conduct = 2
  density = 1
  expand = 3
  formula = G4_CESIUM_FLUORIDE
  name = G4_CESIUM_FLUORIDE
  specific = 4
FEATURE [App::DocumentObjectGroupPython] Cs_element002  label="Cs_element : 002"  # scripted group (container) (typed FeaturePython)
  n = 1
  ref = Cs_element
FEATURE [App::DocumentObjectGroupPython] I_element001  label="I_element : 1"  # scripted group (container) (typed FeaturePython)
  n = 1
  ref = I_element
FEATURE [App::DocumentObjectGroupPython] G4_CESIUM_IODIDE  # scripted group (container) (typed FeaturePython)
  Dunit = g/cm3
  Dvalue = 4.51
  Group = -> [Cs_element002,I_element001]
  conduct = 2
  density = 1
  expand = 3
  formula = G4_CESIUM_IODIDE
  name = G4_CESIUM_IODIDE
  specific = 4
FEATURE [App::DocumentObjectGroupPython] C_element028  label="C_element : 013"  # scripted group (container) (typed FeaturePython)
  n = 6
  ref = C_element
FEATURE [App::DocumentObjectGroupPython] H_element025  label="H_element : 013"  # scripted group (container) (typed FeaturePython)
  n = 5
  ref = H_element
FEATURE [App::DocumentObjectGroupPython] Cl_element005  label="Cl_element : 1"  # scripted group (container) (typed FeaturePython)
  n = 1
  ref = Cl_element
FEATURE [App::DocumentObjectGroupPython] G4_CHLOROBENZENE  # scripted group (container) (typed FeaturePython)
  Dunit = g/cm3
  Dvalue = 1.1058
  Group = -> [C_element028,H_element025,Cl_element005]
  conduct = 2
  density = 1
  expand = 3
  formula = G4_CHLOROBENZENE
  name = G4_CHLOROBENZENE
  specific = 4
FEATURE [App::DocumentObjectGroupPython] C_element029  label="C_element : 014"  # scripted group (container) (typed FeaturePython)
  n = 1
  ref = C_element
FEATURE [App::DocumentObjectGroupPython] H_element026  label="H_element : 1"  # scripted group (container) (typed FeaturePython)
  n = 1
  ref = H_element
FEATURE [App::DocumentObjectGroupPython] Cl_element006  label="Cl_element : 3"  # scripted group (container) (typed FeaturePython)
  n = 3
  ref = Cl_element
FEATURE [App::DocumentObjectGroupPython] G4_CHLOROFORM  # scripted group (container) (typed FeaturePython)
  Dunit = g/cm3
  Dvalue = 1.4832
  Group = -> [C_element029,H_element026,Cl_element006]
  conduct = 2
  density = 1
  expand = 3
  formula = G4_CHLOROFORM
  name = G4_CHLOROFORM
  specific = 4
FEATURE [App::DocumentObjectGroupPython] H_element027  label="H_element : 0.010"  # scripted group (container) (typed FeaturePython)
  n = 0.01
FEATURE [App::DocumentObjectGroupPython] C_element030  label="C_element : 0.001"  # scripted group (container) (typed FeaturePython)
  n = 0.001
FEATURE [App::DocumentObjectGroupPython] O_element030  label="O_element : 0.529"  # scripted group (container) (typed FeaturePython)
  n = 0.529107
FEATURE [App::DocumentObjectGroupPython] Na_element005  label="Na_element : 0.016"  # scripted group (container) (typed FeaturePython)
  n = 0.016
FEATURE [App::DocumentObjectGroupPython] Mg_element003  label="Mg_element : 0.004"  # scripted group (container) (typed FeaturePython)
  n = 0.002
FEATURE [App::DocumentObjectGroupPython] Al_element002  label="Al_element : 0.034"  # scripted group (container) (typed FeaturePython)
  n = 0.033872
FEATURE [App::DocumentObjectGroupPython] Si_element002  label="Si_element : 0.337"  # scripted group (container) (typed FeaturePython)
  n = 0.337021
FEATURE [App::DocumentObjectGroupPython] K_element003  label="K_element : 0.013"  # scripted group (container) (typed FeaturePython)
  n = 0.013
FEATURE [App::DocumentObjectGroupPython] Ca_element010  label="Ca_element : 0.044"  # scripted group (container) (typed FeaturePython)
  n = 0.044
FEATURE [App::DocumentObjectGroupPython] Fe_element002  label="Fe_element : 0.014"  # scripted group (container) (typed FeaturePython)
  n = 0.014
FEATURE [App::DocumentObjectGroupPython] G4_CONCRETE  # scripted group (container) (typed FeaturePython)
  Dunit = g/cm3
  Dvalue = 2.3
  Group = -> [H_element027,C_element030,O_element030,Na_element005,Mg_element003,Al_element002,Si_element002,K_element003,Ca_element010,Fe_element002]
  conduct = 2
  density = 1
  expand = 3
  formula = G4_CONCRETE
  name = G4_CONCRETE
  specific = 4
FEATURE [App::DocumentObjectGroupPython] C_element031  label="C_element : 015"  # scripted group (container) (typed FeaturePython)
  n = 6
  ref = C_element
FEATURE [App::DocumentObjectGroupPython] H_element028  label="H_element : 12"  # scripted group (container) (typed FeaturePython)
  n = 12
  ref = H_element
FEATURE [App::DocumentObjectGroupPython] G4_CYCLOHEXANE  # scripted group (container) (typed FeaturePython)
  Dunit = g/cm3
  Dvalue = 0.779
  Group = -> [C_element031,H_element028]
  conduct = 2
  density = 1
  expand = 3
  formula = G4_CYCLOHEXANE
  name = G4_CYCLOHEXANE
  specific = 4
FEATURE [App::DocumentObjectGroupPython] C_element032  label="C_element : 016"  # scripted group (container) (typed FeaturePython)
  n = 6
  ref = C_element
FEATURE [App::DocumentObjectGroupPython] H_element029  label="H_element : 4"  # scripted group (container) (typed FeaturePython)
  n = 4
  ref = H_element
FEATURE [App::DocumentObjectGroupPython] Cl_element007  label="Cl_element : 2"  # scripted group (container) (typed FeaturePython)
  n = 2
  ref = Cl_element
FEATURE [App::DocumentObjectGroupPython] G4_1_2_DICHLOROBENZENE  label="G4_1.2-DICHLOROBENZENE"  # scripted group (container) (typed FeaturePython)
  Dunit = g/cm3
  Dvalue = 1.3048
  Group = -> [C_element032,H_element029,Cl_element007]
  conduct = 2
  density = 1
  expand = 3
  formula = G4_1.2-DICHLOROBENZENE
  name = G4_1.2-DICHLOROBENZENE
  specific = 4
FEATURE [App::DocumentObjectGroupPython] C_element033  label="C_element : 017"  # scripted group (container) (typed FeaturePython)
  n = 4
  ref = C_element
FEATURE [App::DocumentObjectGroupPython] H_element030  label="H_element : 8"  # scripted group (container) (typed FeaturePython)
  n = 8
  ref = H_element
FEATURE [App::DocumentObjectGroupPython] O_element031  label="O_element : 014"  # scripted group (container) (typed FeaturePython)
  n = 1
  ref = O_element
FEATURE [App::DocumentObjectGroupPython] Cl_element008  label="Cl_element : 005"  # scripted group (container) (typed FeaturePython)
  n = 2
  ref = Cl_element
FEATURE [App::DocumentObjectGroupPython] G4_DICHLORODIETHYL_ETHER  # scripted group (container) (typed FeaturePython)
  Dunit = g/cm3
  Dvalue = 1.2199
  Group = -> [C_element033,H_element030,O_element031,Cl_element008]
  conduct = 2
  density = 1
  expand = 3
  formula = G4_DICHLORODIETHYL_ETHER
  name = G4_DICHLORODIETHYL_ETHER
  specific = 4
FEATURE [App::DocumentObjectGroupPython] C_element034  label="C_element : 018"  # scripted group (container) (typed FeaturePython)
  n = 2
  ref = C_element
FEATURE [App::DocumentObjectGroupPython] H_element031  label="H_element : 014"  # scripted group (container) (typed FeaturePython)
  n = 4
  ref = H_element
FEATURE [App::DocumentObjectGroupPython] Cl_element009  label="Cl_element : 006"  # scripted group (container) (typed FeaturePython)
  n = 2
  ref = Cl_element
FEATURE [App::DocumentObjectGroupPython] G4_1_2_DICHLOROETHANE  label="G4_1.2-DICHLOROETHANE"  # scripted group (container) (typed FeaturePython)
  Dunit = g/cm3
  Dvalue = 1.2351
  Group = -> [C_element034,H_element031,Cl_element009]
  conduct = 2
  density = 1
  expand = 3
  formula = G4_1.2-DICHLOROETHANE
  name = G4_1.2-DICHLOROETHANE
  specific = 4
FEATURE [App::DocumentObjectGroupPython] C_element035  label="C_element : 019"  # scripted group (container) (typed FeaturePython)
  n = 4
  ref = C_element
FEATURE [App::DocumentObjectGroupPython] H_element032  label="H_element : 015"  # scripted group (container) (typed FeaturePython)
  n = 10
  ref = H_element
FEATURE [App::DocumentObjectGroupPython] O_element032  label="O_element : 015"  # scripted group (container) (typed FeaturePython)
  n = 1
  ref = O_element
FEATURE [App::DocumentObjectGroupPython] G4_DIETHYL_ETHER  # scripted group (container) (typed FeaturePython)
  Dunit = g/cm3
  Dvalue = 0.71378
  Group = -> [C_element035,H_element032,O_element032]
  conduct = 2
  density = 1
  expand = 3
  formula = G4_DIETHYL_ETHER
  name = G4_DIETHYL_ETHER
  specific = 4
FEATURE [App::DocumentObjectGroupPython] C_element036  label="C_element : 020"  # scripted group (container) (typed FeaturePython)
  n = 3
  ref = C_element
FEATURE [App::DocumentObjectGroupPython] H_element033  label="H_element : 016"  # scripted group (container) (typed FeaturePython)
  n = 7
  ref = H_element
FEATURE [App::DocumentObjectGroupPython] N_element015  label="N_element : 008"  # scripted group (container) (typed FeaturePython)
  n = 1
  ref = N_element
FEATURE [App::DocumentObjectGroupPython] O_element033  label="O_element : 016"  # scripted group (container) (typed FeaturePython)
  n = 1
  ref = O_element
FEATURE [App::DocumentObjectGroupPython] G4_N_N_DIMETHYL_FORMAMIDE  label="G4_N.N-DIMETHYL_FORMAMIDE"  # scripted group (container) (typed FeaturePython)
  Dunit = g/cm3
  Dvalue = 0.9487
  Group = -> [C_element036,H_element033,N_element015,O_element033]
  conduct = 2
  density = 1
  expand = 3
  formula = G4_N.N-DIMETHYL_FORMAMIDE
  name = G4_N.N-DIMETHYL_FORMAMIDE
  specific = 4
FEATURE [App::DocumentObjectGroupPython] C_element037  label="C_element : 021"  # scripted group (container) (typed FeaturePython)
  n = 2
  ref = C_element
FEATURE [App::DocumentObjectGroupPython] H_element034  label="H_element : 017"  # scripted group (container) (typed FeaturePython)
  n = 6
  ref = H_element
FEATURE [App::DocumentObjectGroupPython] O_element034  label="O_element : 017"  # scripted group (container) (typed FeaturePython)
  n = 1
  ref = O_element
FEATURE [App::DocumentObjectGroupPython] S_element009  label="S_element : 003"  # scripted group (container) (typed FeaturePython)
  n = 1
  ref = S_element
FEATURE [App::DocumentObjectGroupPython] G4_DIMETHYL_SULFOXIDE  # scripted group (container) (typed FeaturePython)
  Dunit = g/cm3
  Dvalue = 1.1014
  Group = -> [C_element037,H_element034,O_element034,S_element009]
  conduct = 2
  density = 1
  expand = 3
  formula = G4_DIMETHYL_SULFOXIDE
  name = G4_DIMETHYL_SULFOXIDE
  specific = 4
FEATURE [App::DocumentObjectGroupPython] C_element038  label="C_element : 022"  # scripted group (container) (typed FeaturePython)
  n = 2
  ref = C_element
FEATURE [App::DocumentObjectGroupPython] H_element035  label="H_element : 018"  # scripted group (container) (typed FeaturePython)
  n = 6
  ref = H_element
FEATURE [App::DocumentObjectGroupPython] G4_ETHANE  # scripted group (container) (typed FeaturePython)
  Dunit = g/cm3
  Dvalue = 0.00125324
  Group = -> [C_element038,H_element035]
  conduct = 2
  density = 1
  expand = 3
  formula = G4_ETHANE
  name = G4_ETHANE
  specific = 4
FEATURE [App::DocumentObjectGroupPython] C_element039  label="C_element : 023"  # scripted group (container) (typed FeaturePython)
  n = 2
  ref = C_element
FEATURE [App::DocumentObjectGroupPython] H_element036  label="H_element : 019"  # scripted group (container) (typed FeaturePython)
  n = 6
  ref = H_element
FEATURE [App::DocumentObjectGroupPython] O_element035  label="O_element : 018"  # scripted group (container) (typed FeaturePython)
  n = 1
  ref = O_element
FEATURE [App::DocumentObjectGroupPython] G4_ETHYL_ALCOHOL  # scripted group (container) (typed FeaturePython)
  Dunit = g/cm3
  Dvalue = 0.7893
  Group = -> [C_element039,H_element036,O_element035]
  conduct = 2
  density = 1
  expand = 3
  formula = G4_ETHYL_ALCOHOL
  name = G4_ETHYL_ALCOHOL
  specific = 4
FEATURE [App::DocumentObjectGroupPython] H_element037  label="H_element : 0.090"  # scripted group (container) (typed FeaturePython)
  n = 0.090027
FEATURE [App::DocumentObjectGroupPython] C_element040  label="C_element : 0.585"  # scripted group (container) (typed FeaturePython)
  n = 0.585182
FEATURE [App::DocumentObjectGroupPython] O_element036  label="O_element : 0.325"  # scripted group (container) (typed FeaturePython)
  n = 0.324791
FEATURE [App::DocumentObjectGroupPython] G4_ETHYL_CELLULOSE  # scripted group (container) (typed FeaturePython)
  Dunit = g/cm3
  Dvalue = 1.13
  Group = -> [H_element037,C_element040,O_element036]
  conduct = 2
  density = 1
  expand = 3
  formula = G4_ETHYL_CELLULOSE
  name = G4_ETHYL_CELLULOSE
  specific = 4
FEATURE [App::DocumentObjectGroupPython] C_element041  label="C_element : 024"  # scripted group (container) (typed FeaturePython)
  n = 2
  ref = C_element
FEATURE [App::DocumentObjectGroupPython] H_element038  label="H_element : 020"  # scripted group (container) (typed FeaturePython)
  n = 4
  ref = H_element
FEATURE [App::DocumentObjectGroupPython] G4_ETHYLENE  # scripted group (container) (typed FeaturePython)
  Dunit = g/cm3
  Dvalue = 0.00117497
  Group = -> [C_element041,H_element038]
  conduct = 2
  density = 1
  expand = 3
  formula = G4_ETHYLENE
  name = G4_ETHYLENE
  specific = 4
FEATURE [App::DocumentObjectGroupPython] H_element039  label="H_element : 0.096"  # scripted group (container) (typed FeaturePython)
  n = 0.096
FEATURE [App::DocumentObjectGroupPython] C_element042  label="C_element : 0.195"  # scripted group (container) (typed FeaturePython)
  n = 0.195
FEATURE [App::DocumentObjectGroupPython] N_element016  label="N_element : 0.057"  # scripted group (container) (typed FeaturePython)
  n = 0.057
FEATURE [App::DocumentObjectGroupPython] O_element037  label="O_element : 0.646"  # scripted group (container) (typed FeaturePython)
  n = 0.646
FEATURE [App::DocumentObjectGroupPython] Na_element006  label="Na_element : 0.017"  # scripted group (container) (typed FeaturePython)
  n = 0.001
FEATURE [App::DocumentObjectGroupPython] P_element005  label="P_element : 0.104"  # scripted group (container) (typed FeaturePython)
  n = 0.001
FEATURE [App::DocumentObjectGroupPython] S_element010  label="S_element : 0.016"  # scripted group (container) (typed FeaturePython)
  n = 0.003
FEATURE [App::DocumentObjectGroupPython] Cl_element010  label="Cl_element : 0.005"  # scripted group (container) (typed FeaturePython)
  n = 0.001
FEATURE [App::DocumentObjectGroupPython] G4_EYE_LENS_ICRP  # scripted group (container) (typed FeaturePython)
  Dunit = g/cm3
  Dvalue = 1.07
  Group = -> [H_element039,C_element042,N_element016,O_element037,Na_element006,P_element005,S_element010,Cl_element010]
  conduct = 2
  density = 1
  expand = 3
  formula = G4_EYE_LENS_ICRP
  name = G4_EYE_LENS_ICRP
  specific = 4
FEATURE [App::DocumentObjectGroupPython] Fe_element003  label="Fe_element : 2"  # scripted group (container) (typed FeaturePython)
  n = 2
  ref = Fe_element
FEATURE [App::DocumentObjectGroupPython] O_element038  label="O_element : 019"  # scripted group (container) (typed FeaturePython)
  n = 3
  ref = O_element
FEATURE [App::DocumentObjectGroupPython] G4_FERRIC_OXIDE  # scripted group (container) (typed FeaturePython)
  Dunit = g/cm3
  Dvalue = 5.2
  Group = -> [Fe_element003,O_element038]
  conduct = 2
  density = 1
  expand = 3
  formula = G4_FERRIC_OXIDE
  name = G4_FERRIC_OXIDE
  specific = 4
FEATURE [App::DocumentObjectGroupPython] Fe_element004  label="Fe_element : 1"  # scripted group (container) (typed FeaturePython)
  n = 1
  ref = Fe_element
FEATURE [App::DocumentObjectGroupPython] B_element003  label="B_element : 1"  # scripted group (container) (typed FeaturePython)
  n = 1
  ref = B_element
FEATURE [App::DocumentObjectGroupPython] G4_FERROBORIDE  # scripted group (container) (typed FeaturePython)
  Dunit = g/cm3
  Dvalue = 7.15
  Group = -> [Fe_element004,B_element003]
  conduct = 2
  density = 1
  expand = 3
  formula = G4_FERROBORIDE
  name = G4_FERROBORIDE
  specific = 4
FEATURE [App::DocumentObjectGroupPython] Fe_element005  label="Fe_element : 003"  # scripted group (container) (typed FeaturePython)
  n = 1
  ref = Fe_element
FEATURE [App::DocumentObjectGroupPython] O_element039  label="O_element : 020"  # scripted group (container) (typed FeaturePython)
  n = 1
  ref = O_element
FEATURE [App::DocumentObjectGroupPython] G4_FERROUS_OXIDE  # scripted group (container) (typed FeaturePython)
  Dunit = g/cm3
  Dvalue = 5.7
  Group = -> [Fe_element005,O_element039]
  conduct = 2
  density = 1
  expand = 3
  formula = G4_FERROUS_OXIDE
  name = G4_FERROUS_OXIDE
  specific = 4
FEATURE [App::DocumentObjectGroupPython] H_element040  label="H_element : 0.115"  # scripted group (container) (typed FeaturePython)
  n = 0.108259
FEATURE [App::DocumentObjectGroupPython] N_element017  label="N_element : 0.000"  # scripted group (container) (typed FeaturePython)
  n = 2.7e-05
FEATURE [App::DocumentObjectGroupPython] O_element040  label="O_element : 0.879"  # scripted group (container) (typed FeaturePython)
  n = 0.878636
FEATURE [App::DocumentObjectGroupPython] Na_element007  label="Na_element : 0.000"  # scripted group (container) (typed FeaturePython)
  n = 2.2e-05
FEATURE [App::DocumentObjectGroupPython] S_element011  label="S_element : 0.013"  # scripted group (container) (typed FeaturePython)
  n = 0.012968
FEATURE [App::DocumentObjectGroupPython] Cl_element011  label="Cl_element : 0.000"  # scripted group (container) (typed FeaturePython)
  n = 3.4e-05
FEATURE [App::DocumentObjectGroupPython] Fe_element006  label="Fe_element : 0.000"  # scripted group (container) (typed FeaturePython)
  n = 5.4e-05
FEATURE [App::DocumentObjectGroupPython] G4_FERROUS_SULFATE  # scripted group (container) (typed FeaturePython)
  Dunit = g/cm3
  Dvalue = 1.024
  Group = -> [H_element040,N_element017,O_element040,Na_element007,S_element011,Cl_element011,Fe_element006]
  conduct = 2
  density = 1
  expand = 3
  formula = G4_FERROUS_SULFATE
  name = G4_FERROUS_SULFATE
  specific = 4
FEATURE [App::DocumentObjectGroupPython] C_element043  label="C_element : 0.099"  # scripted group (container) (typed FeaturePython)
  n = 0.099335
FEATURE [App::DocumentObjectGroupPython] F_element007  label="F_element : 0.314"  # scripted group (container) (typed FeaturePython)
  n = 0.314247
FEATURE [App::DocumentObjectGroupPython] Cl_element012  label="Cl_element : 0.586"  # scripted group (container) (typed FeaturePython)
  n = 0.586418
FEATURE [App::DocumentObjectGroupPython] G4_FREON_12  label="G4_FREON-12"  # scripted group (container) (typed FeaturePython)
  Dunit = g/cm3
  Dvalue = 1.12
  Group = -> [C_element043,F_element007,Cl_element012]
  conduct = 2
  density = 1
  expand = 3
  formula = G4_FREON-12
  name = G4_FREON-12
  specific = 4
FEATURE [App::DocumentObjectGroupPython] C_element044  label="C_element : 0.057"  # scripted group (container) (typed FeaturePython)
  n = 0.057245
FEATURE [App::DocumentObjectGroupPython] F_element008  label="F_element : 0.181"  # scripted group (container) (typed FeaturePython)
  n = 0.181096
FEATURE [App::DocumentObjectGroupPython] Br_element001  label="Br_element : 0.762"  # scripted group (container) (typed FeaturePython)
  n = 0.761659
FEATURE [App::DocumentObjectGroupPython] G4_FREON_12B2  label="G4_FREON-12B2"  # scripted group (container) (typed FeaturePython)
  Dunit = g/cm3
  Dvalue = 1.8
  Group = -> [C_element044,F_element008,Br_element001]
  conduct = 2
  density = 1
  expand = 3
  formula = G4_FREON-12B2
  name = G4_FREON-12B2
  specific = 4
FEATURE [App::DocumentObjectGroupPython] C_element045  label="C_element : 0.115"  # scripted group (container) (typed FeaturePython)
  n = 0.114983
FEATURE [App::DocumentObjectGroupPython] F_element009  label="F_element : 0.546"  # scripted group (container) (typed FeaturePython)
  n = 0.545621
FEATURE [App::DocumentObjectGroupPython] Cl_element013  label="Cl_element : 0.339"  # scripted group (container) (typed FeaturePython)
  n = 0.339396
FEATURE [App::DocumentObjectGroupPython] G4_FREON_13  label="G4_FREON-13"  # scripted group (container) (typed FeaturePython)
  Dunit = g/cm3
  Dvalue = 0.95
  Group = -> [C_element045,F_element009,Cl_element013]
  conduct = 2
  density = 1
  expand = 3
  formula = G4_FREON-13
  name = G4_FREON-13
  specific = 4
FEATURE [App::DocumentObjectGroupPython] C_element046  label="C_element : 025"  # scripted group (container) (typed FeaturePython)
  n = 1
  ref = C_element
FEATURE [App::DocumentObjectGroupPython] F_element010  label="F_element : 3"  # scripted group (container) (typed FeaturePython)
  n = 3
  ref = F_element
FEATURE [App::DocumentObjectGroupPython] Br_element002  label="Br_element : 1"  # scripted group (container) (typed FeaturePython)
  n = 1
  ref = Br_element
FEATURE [App::DocumentObjectGroupPython] G4_FREON_13B1  label="G4_FREON-13B1"  # scripted group (container) (typed FeaturePython)
  Dunit = g/cm3
  Dvalue = 1.5
  Group = -> [C_element046,F_element010,Br_element002]
  conduct = 2
  density = 1
  expand = 3
  formula = G4_FREON-13B1
  name = G4_FREON-13B1
  specific = 4
FEATURE [App::DocumentObjectGroupPython] C_element047  label="C_element : 0.061"  # scripted group (container) (typed FeaturePython)
  n = 0.061309
FEATURE [App::DocumentObjectGroupPython] F_element011  label="F_element : 0.291"  # scripted group (container) (typed FeaturePython)
  n = 0.290924
FEATURE [App::DocumentObjectGroupPython] I_element002  label="I_element : 0.648"  # scripted group (container) (typed FeaturePython)
  n = 0.647767
FEATURE [App::DocumentObjectGroupPython] G4_FREON_13I1  label="G4_FREON-13I1"  # scripted group (container) (typed FeaturePython)
  Dunit = g/cm3
  Dvalue = 1.8
  Group = -> [C_element047,F_element011,I_element002]
  conduct = 2
  density = 1
  expand = 3
  formula = G4_FREON-13I1
  name = G4_FREON-13I1
  specific = 4
FEATURE [App::DocumentObjectGroupPython] Gd_element001  label="Gd_element : 2"  # scripted group (container) (typed FeaturePython)
  n = 2
  ref = Gd_element
FEATURE [App::DocumentObjectGroupPython] O_element041  label="O_element : 021"  # scripted group (container) (typed FeaturePython)
  n = 2
  ref = O_element
FEATURE [App::DocumentObjectGroupPython] S_element012  label="S_element : 004"  # scripted group (container) (typed FeaturePython)
  n = 1
  ref = S_element
FEATURE [App::DocumentObjectGroupPython] G4_GADOLINIUM_OXYSULFIDE  # scripted group (container) (typed FeaturePython)
  Dunit = g/cm3
  Dvalue = 7.44
  Group = -> [Gd_element001,O_element041,S_element012]
  conduct = 2
  density = 1
  expand = 3
  formula = G4_GADOLINIUM_OXYSULFIDE
  name = G4_GADOLINIUM_OXYSULFIDE
  specific = 4
FEATURE [App::DocumentObjectGroupPython] Ga_element001  label="Ga_element : 1"  # scripted group (container) (typed FeaturePython)
  n = 1
  ref = Ga_element
FEATURE [App::DocumentObjectGroupPython] As_element001  label="As_element : 1"  # scripted group (container) (typed FeaturePython)
  n = 1
  ref = As_element
FEATURE [App::DocumentObjectGroupPython] G4_GALLIUM_ARSENIDE  # scripted group (container) (typed FeaturePython)
  Dunit = g/cm3
  Dvalue = 5.31
  Group = -> [Ga_element001,As_element001]
  conduct = 2
  density = 1
  expand = 3
  formula = G4_GALLIUM_ARSENIDE
  name = G4_GALLIUM_ARSENIDE
  specific = 4
FEATURE [App::DocumentObjectGroupPython] H_element041  label="H_element : 0.081"  # scripted group (container) (typed FeaturePython)
  n = 0.08118
FEATURE [App::DocumentObjectGroupPython] C_element048  label="C_element : 0.416"  # scripted group (container) (typed FeaturePython)
  n = 0.41606
FEATURE [App::DocumentObjectGroupPython] N_element018  label="N_element : 0.111"  # scripted group (container) (typed FeaturePython)
  n = 0.11124
FEATURE [App::DocumentObjectGroupPython] O_element042  label="O_element : 0.381"  # scripted group (container) (typed FeaturePython)
  n = 0.38064
FEATURE [App::DocumentObjectGroupPython] S_element013  label="S_element : 0.011"  # scripted group (container) (typed FeaturePython)
  n = 0.01088
FEATURE [App::DocumentObjectGroupPython] G4_GEL_PHOTO_EMULSION  # scripted group (container) (typed FeaturePython)
  Dunit = g/cm3
  Dvalue = 1.2914
  Group = -> [H_element041,C_element048,N_element018,O_element042,S_element013]
  conduct = 2
  density = 1
  expand = 3
  formula = G4_GEL_PHOTO_EMULSION
  name = G4_GEL_PHOTO_EMULSION
  specific = 4
FEATURE [App::DocumentObjectGroupPython] B_element004  label="B_element : 0.040"  # scripted group (container) (typed FeaturePython)
  n = 0.0400639
FEATURE [App::DocumentObjectGroupPython] O_element043  label="O_element : 0.540"  # scripted group (container) (typed FeaturePython)
  n = 0.539561
FEATURE [App::DocumentObjectGroupPython] Na_element008  label="Na_element : 0.028"  # scripted group (container) (typed FeaturePython)
  n = 0.0281909
FEATURE [App::DocumentObjectGroupPython] Al_element003  label="Al_element : 0.012"  # scripted group (container) (typed FeaturePython)
  n = 0.011644
FEATURE [App::DocumentObjectGroupPython] Si_element003  label="Si_element : 0.377"  # scripted group (container) (typed FeaturePython)
  n = 0.377219
FEATURE [App::DocumentObjectGroupPython] K_element004  label="K_element : 0.014"  # scripted group (container) (typed FeaturePython)
  n = 0.00332099
FEATURE [App::DocumentObjectGroupPython] G4_Pyrex_Glass  # scripted group (container) (typed FeaturePython)
  Dunit = g/cm3
  Dvalue = 2.23
  Group = -> [B_element004,O_element043,Na_element008,Al_element003,Si_element003,K_element004]
  conduct = 2
  density = 1
  expand = 3
  formula = G4_Pyrex_Glass
  name = G4_Pyrex_Glass
  specific = 4
FEATURE [App::DocumentObjectGroupPython] O_element044  label="O_element : 0.156"  # scripted group (container) (typed FeaturePython)
  n = 0.156453
FEATURE [App::DocumentObjectGroupPython] Si_element004  label="Si_element : 0.081"  # scripted group (container) (typed FeaturePython)
  n = 0.080866
FEATURE [App::DocumentObjectGroupPython] Ti_element001  label="Ti_element : 0.008"  # scripted group (container) (typed FeaturePython)
  n = 0.008092
FEATURE [App::DocumentObjectGroupPython] As_element002  label="As_element : 0.003"  # scripted group (container) (typed FeaturePython)
  n = 0.002651
FEATURE [App::DocumentObjectGroupPython] Pb_element001  label="Pb_element : 0.752"  # scripted group (container) (typed FeaturePython)
  n = 0.751938
FEATURE [App::DocumentObjectGroupPython] G4_GLASS_LEAD  # scripted group (container) (typed FeaturePython)
  Dunit = g/cm3
  Dvalue = 6.22
  Group = -> [O_element044,Si_element004,Ti_element001,As_element002,Pb_element001]
  conduct = 2
  density = 1
  expand = 3
  formula = G4_GLASS_LEAD
  name = G4_GLASS_LEAD
  specific = 4
FEATURE [App::DocumentObjectGroupPython] O_element045  label="O_element : 0.460"  # scripted group (container) (typed FeaturePython)
  n = 0.4598
FEATURE [App::DocumentObjectGroupPython] Na_element009  label="Na_element : 0.096"  # scripted group (container) (typed FeaturePython)
  n = 0.0964411
FEATURE [App::DocumentObjectGroupPython] Si_element005  label="Si_element : 0.378"  # scripted group (container) (typed FeaturePython)
  n = 0.336553
FEATURE [App::DocumentObjectGroupPython] Ca_element011  label="Ca_element : 0.107"  # scripted group (container) (typed FeaturePython)
  n = 0.107205
FEATURE [App::DocumentObjectGroupPython] G4_GLASS_PLATE  # scripted group (container) (typed FeaturePython)
  Dunit = g/cm3
  Dvalue = 2.4
  Group = -> [O_element045,Na_element009,Si_element005,Ca_element011]
  conduct = 2
  density = 1
  expand = 3
  formula = G4_GLASS_PLATE
  name = G4_GLASS_PLATE
  specific = 4
FEATURE [App::DocumentObjectGroupPython] C_element049  label="C_element : 026"  # scripted group (container) (typed FeaturePython)
  n = 5
  ref = C_element
FEATURE [App::DocumentObjectGroupPython] H_element042  label="H_element : 021"  # scripted group (container) (typed FeaturePython)
  n = 10
  ref = H_element
FEATURE [App::DocumentObjectGroupPython] N_element019  label="N_element : 2"  # scripted group (container) (typed FeaturePython)
  n = 2
  ref = N_element
FEATURE [App::DocumentObjectGroupPython] O_element046  label="O_element : 022"  # scripted group (container) (typed FeaturePython)
  n = 3
  ref = O_element
FEATURE [App::DocumentObjectGroupPython] G4_GLUTAMINE  # scripted group (container) (typed FeaturePython)
  Dunit = g/cm3
  Dvalue = 1.46
  Group = -> [C_element049,H_element042,N_element019,O_element046]
  conduct = 2
  density = 1
  expand = 3
  formula = G4_GLUTAMINE
  name = G4_GLUTAMINE
  specific = 4
FEATURE [App::DocumentObjectGroupPython] C_element050  label="C_element : 027"  # scripted group (container) (typed FeaturePython)
  n = 3
  ref = C_element
FEATURE [App::DocumentObjectGroupPython] H_element043  label="H_element : 022"  # scripted group (container) (typed FeaturePython)
  n = 8
  ref = H_element
FEATURE [App::DocumentObjectGroupPython] O_element047  label="O_element : 023"  # scripted group (container) (typed FeaturePython)
  n = 3
  ref = O_element
FEATURE [App::DocumentObjectGroupPython] G4_GLYCEROL  # scripted group (container) (typed FeaturePython)
  Dunit = g/cm3
  Dvalue = 1.2613
  Group = -> [C_element050,H_element043,O_element047]
  conduct = 2
  density = 1
  expand = 3
  formula = G4_GLYCEROL
  name = G4_GLYCEROL
  specific = 4
FEATURE [App::DocumentObjectGroupPython] C_element051  label="C_element : 028"  # scripted group (container) (typed FeaturePython)
  n = 5
  ref = C_element
FEATURE [App::DocumentObjectGroupPython] H_element044  label="H_element : 023"  # scripted group (container) (typed FeaturePython)
  n = 5
  ref = H_element
FEATURE [App::DocumentObjectGroupPython] N_element020  label="N_element : 009"  # scripted group (container) (typed FeaturePython)
  n = 5
  ref = N_element
FEATURE [App::DocumentObjectGroupPython] O_element048  label="O_element : 024"  # scripted group (container) (typed FeaturePython)
  n = 1
  ref = O_element
FEATURE [App::DocumentObjectGroupPython] G4_GUANINE  # scripted group (container) (typed FeaturePython)
  Dunit = g/cm3
  Dvalue = 2.2
  Group = -> [C_element051,H_element044,N_element020,O_element048]
  conduct = 2
  density = 1
  expand = 3
  formula = G4_GUANINE
  name = G4_GUANINE
  specific = 4
FEATURE [App::DocumentObjectGroupPython] Ca_element012  label="Ca_element : 006"  # scripted group (container) (typed FeaturePython)
  n = 1
  ref = Ca_element
FEATURE [App::DocumentObjectGroupPython] S_element014  label="S_element : 005"  # scripted group (container) (typed FeaturePython)
  n = 1
  ref = S_element
FEATURE [App::DocumentObjectGroupPython] O_element049  label="O_element : 6"  # scripted group (container) (typed FeaturePython)
  n = 6
  ref = O_element
FEATURE [App::DocumentObjectGroupPython] H_element045  label="H_element : 024"  # scripted group (container) (typed FeaturePython)
  n = 4
  ref = H_element
FEATURE [App::DocumentObjectGroupPython] G4_GYPSUM  # scripted group (container) (typed FeaturePython)
  Dunit = g/cm3
  Dvalue = 2.32
  Group = -> [Ca_element012,S_element014,O_element049,H_element045]
  conduct = 2
  density = 1
  expand = 3
  formula = G4_GYPSUM
  name = G4_GYPSUM
  specific = 4
FEATURE [App::DocumentObjectGroupPython] C_element052  label="C_element : 7"  # scripted group (container) (typed FeaturePython)
  n = 7
  ref = C_element
FEATURE [App::DocumentObjectGroupPython] H_element046  label="H_element : 16"  # scripted group (container) (typed FeaturePython)
  n = 16
  ref = H_element
FEATURE [App::DocumentObjectGroupPython] G4_N_HEPTANE  label="G4_N-HEPTANE"  # scripted group (container) (typed FeaturePython)
  Dunit = g/cm3
  Dvalue = 0.68376
  Group = -> [C_element052,H_element046]
  conduct = 2
  density = 1
  expand = 3
  formula = G4_N-HEPTANE
  name = G4_N-HEPTANE
  specific = 4
FEATURE [App::DocumentObjectGroupPython] C_element053  label="C_element : 029"  # scripted group (container) (typed FeaturePython)
  n = 6
  ref = C_element
FEATURE [App::DocumentObjectGroupPython] H_element047  label="H_element : 14"  # scripted group (container) (typed FeaturePython)
  n = 14
  ref = H_element
FEATURE [App::DocumentObjectGroupPython] G4_N_HEXANE  label="G4_N-HEXANE"  # scripted group (container) (typed FeaturePython)
  Dunit = g/cm3
  Dvalue = 0.6603
  Group = -> [C_element053,H_element047]
  conduct = 2
  density = 1
  expand = 3
  formula = G4_N-HEXANE
  name = G4_N-HEXANE
  specific = 4
FEATURE [App::DocumentObjectGroupPython] C_element054  label="C_element : 22"  # scripted group (container) (typed FeaturePython)
  n = 22
  ref = C_element
FEATURE [App::DocumentObjectGroupPython] H_element048  label="H_element : 025"  # scripted group (container) (typed FeaturePython)
  n = 10
  ref = H_element
FEATURE [App::DocumentObjectGroupPython] N_element021  label="N_element : 010"  # scripted group (container) (typed FeaturePython)
  n = 2
  ref = N_element
FEATURE [App::DocumentObjectGroupPython] O_element050  label="O_element : 025"  # scripted group (container) (typed FeaturePython)
  n = 5
  ref = O_element
FEATURE [App::DocumentObjectGroupPython] G4_KAPTON  # scripted group (container) (typed FeaturePython)
  Dunit = g/cm3
  Dvalue = 1.42
  Group = -> [C_element054,H_element048,N_element021,O_element050]
  conduct = 2
  density = 1
  expand = 3
  formula = G4_KAPTON
  name = G4_KAPTON
  specific = 4
FEATURE [App::DocumentObjectGroupPython] La_element001  label="La_element : 1"  # scripted group (container) (typed FeaturePython)
  n = 1
  ref = La_element
FEATURE [App::DocumentObjectGroupPython] Br_element003  label="Br_element : 002"  # scripted group (container) (typed FeaturePython)
  n = 1
  ref = Br_element
FEATURE [App::DocumentObjectGroupPython] O_element051  label="O_element : 026"  # scripted group (container) (typed FeaturePython)
  n = 1
  ref = O_element
FEATURE [App::DocumentObjectGroupPython] G4_LANTHANUM_OXYBROMIDE  # scripted group (container) (typed FeaturePython)
  Dunit = g/cm3
  Dvalue = 6.28
  Group = -> [La_element001,Br_element003,O_element051]
  conduct = 2
  density = 1
  expand = 3
  formula = G4_LANTHANUM_OXYBROMIDE
  name = G4_LANTHANUM_OXYBROMIDE
  specific = 4
FEATURE [App::DocumentObjectGroupPython] La_element002  label="La_element : 2"  # scripted group (container) (typed FeaturePython)
  n = 2
  ref = La_element
FEATURE [App::DocumentObjectGroupPython] O_element052  label="O_element : 027"  # scripted group (container) (typed FeaturePython)
  n = 2
  ref = O_element
FEATURE [App::DocumentObjectGroupPython] S_element015  label="S_element : 006"  # scripted group (container) (typed FeaturePython)
  n = 1
  ref = S_element
FEATURE [App::DocumentObjectGroupPython] G4_LANTHANUM_OXYSULFIDE  # scripted group (container) (typed FeaturePython)
  Dunit = g/cm3
  Dvalue = 5.86
  Group = -> [La_element002,O_element052,S_element015]
  conduct = 2
  density = 1
  expand = 3
  formula = G4_LANTHANUM_OXYSULFIDE
  name = G4_LANTHANUM_OXYSULFIDE
  specific = 4
FEATURE [App::DocumentObjectGroupPython] O_element053  label="O_element : 0.072"  # scripted group (container) (typed FeaturePython)
  n = 0.071682
FEATURE [App::DocumentObjectGroupPython] Pb_element002  label="Pb_element : 0.928"  # scripted group (container) (typed FeaturePython)
  n = 0.928318
FEATURE [App::DocumentObjectGroupPython] G4_LEAD_OXIDE  # scripted group (container) (typed FeaturePython)
  Dunit = g/cm3
  Dvalue = 9.53
  Group = -> [O_element053,Pb_element002]
  conduct = 2
  density = 1
  expand = 3
  formula = G4_LEAD_OXIDE
  name = G4_LEAD_OXIDE
  specific = 4
FEATURE [App::DocumentObjectGroupPython] Li_element001  label="Li_element : 1"  # scripted group (container) (typed FeaturePython)
  n = 1
  ref = Li_element
FEATURE [App::DocumentObjectGroupPython] N_element022  label="N_element : 011"  # scripted group (container) (typed FeaturePython)
  n = 1
  ref = N_element
FEATURE [App::DocumentObjectGroupPython] H_element049  label="H_element : 026"  # scripted group (container) (typed FeaturePython)
  n = 2
  ref = H_element
FEATURE [App::DocumentObjectGroupPython] G4_LITHIUM_AMIDE  # scripted group (container) (typed FeaturePython)
  Dunit = g/cm3
  Dvalue = 1.178
  Group = -> [Li_element001,N_element022,H_element049]
  conduct = 2
  density = 1
  expand = 3
  formula = G4_LITHIUM_AMIDE
  name = G4_LITHIUM_AMIDE
  specific = 4
FEATURE [App::DocumentObjectGroupPython] Li_element002  label="Li_element : 2"  # scripted group (container) (typed FeaturePython)
  n = 2
  ref = Li_element
FEATURE [App::DocumentObjectGroupPython] C_element055  label="C_element : 030"  # scripted group (container) (typed FeaturePython)
  n = 1
  ref = C_element
FEATURE [App::DocumentObjectGroupPython] O_element054  label="O_element : 028"  # scripted group (container) (typed FeaturePython)
  n = 3
  ref = O_element
FEATURE [App::DocumentObjectGroupPython] G4_LITHIUM_CARBONATE  # scripted group (container) (typed FeaturePython)
  Dunit = g/cm3
  Dvalue = 2.11
  Group = -> [Li_element002,C_element055,O_element054]
  conduct = 2
  density = 1
  expand = 3
  formula = G4_LITHIUM_CARBONATE
  name = G4_LITHIUM_CARBONATE
  specific = 4
FEATURE [App::DocumentObjectGroupPython] Li_element003  label="Li_element : 003"  # scripted group (container) (typed FeaturePython)
  n = 1
  ref = Li_element
FEATURE [App::DocumentObjectGroupPython] F_element012  label="F_element : 004"  # scripted group (container) (typed FeaturePython)
  n = 1
  ref = F_element
FEATURE [App::DocumentObjectGroupPython] G4_LITHIUM_FLUORIDE  # scripted group (container) (typed FeaturePython)
  Dunit = g/cm3
  Dvalue = 2.635
  Group = -> [Li_element003,F_element012]
  conduct = 2
  density = 1
  expand = 3
  formula = G4_LITHIUM_FLUORIDE
  name = G4_LITHIUM_FLUORIDE
  specific = 4
FEATURE [App::DocumentObjectGroupPython] Li_element004  label="Li_element : 004"  # scripted group (container) (typed FeaturePython)
  n = 1
  ref = Li_element
FEATURE [App::DocumentObjectGroupPython] H_element050  label="H_element : 027"  # scripted group (container) (typed FeaturePython)
  n = 1
  ref = H_element
FEATURE [App::DocumentObjectGroupPython] G4_LITHIUM_HYDRIDE  # scripted group (container) (typed FeaturePython)
  Dunit = g/cm3
  Dvalue = 0.82
  Group = -> [Li_element004,H_element050]
  conduct = 2
  density = 1
  expand = 3
  formula = G4_LITHIUM_HYDRIDE
  name = G4_LITHIUM_HYDRIDE
  specific = 4
FEATURE [App::DocumentObjectGroupPython] Li_element005  label="Li_element : 005"  # scripted group (container) (typed FeaturePython)
  n = 1
  ref = Li_element
FEATURE [App::DocumentObjectGroupPython] I_element003  label="I_element : 002"  # scripted group (container) (typed FeaturePython)
  n = 1
  ref = I_element
FEATURE [App::DocumentObjectGroupPython] G4_LITHIUM_IODIDE  # scripted group (container) (typed FeaturePython)
  Dunit = g/cm3
  Dvalue = 3.494
  Group = -> [Li_element005,I_element003]
  conduct = 2
  density = 1
  expand = 3
  formula = G4_LITHIUM_IODIDE
  name = G4_LITHIUM_IODIDE
  specific = 4
FEATURE [App::DocumentObjectGroupPython] Li_element006  label="Li_element : 006"  # scripted group (container) (typed FeaturePython)
  n = 2
  ref = Li_element
FEATURE [App::DocumentObjectGroupPython] O_element055  label="O_element : 029"  # scripted group (container) (typed FeaturePython)
  n = 1
  ref = O_element
FEATURE [App::DocumentObjectGroupPython] G4_LITHIUM_OXIDE  # scripted group (container) (typed FeaturePython)
  Dunit = g/cm3
  Dvalue = 2.013
  Group = -> [Li_element006,O_element055]
  conduct = 2
  density = 1
  expand = 3
  formula = G4_LITHIUM_OXIDE
  name = G4_LITHIUM_OXIDE
  specific = 4
FEATURE [App::DocumentObjectGroupPython] Li_element007  label="Li_element : 007"  # scripted group (container) (typed FeaturePython)
  n = 2
  ref = Li_element
FEATURE [App::DocumentObjectGroupPython] B_element005  label="B_element : 005"  # scripted group (container) (typed FeaturePython)
  n = 4
  ref = B_element
FEATURE [App::DocumentObjectGroupPython] O_element056  label="O_element : 7"  # scripted group (container) (typed FeaturePython)
  n = 7
  ref = O_element
FEATURE [App::DocumentObjectGroupPython] G4_LITHIUM_TETRABORATE  # scripted group (container) (typed FeaturePython)
  Dunit = g/cm3
  Dvalue = 2.44
  Group = -> [Li_element007,B_element005,O_element056]
  conduct = 2
  density = 1
  expand = 3
  formula = G4_LITHIUM_TETRABORATE
  name = G4_LITHIUM_TETRABORATE
  specific = 4
FEATURE [App::DocumentObjectGroupPython] H_element051  label="H_element : 0.105"  # scripted group (container) (typed FeaturePython)
  n = 0.105
FEATURE [App::DocumentObjectGroupPython] C_element056  label="C_element : 0.083"  # scripted group (container) (typed FeaturePython)
  n = 0.083
FEATURE [App::DocumentObjectGroupPython] N_element023  label="N_element : 0.023"  # scripted group (container) (typed FeaturePython)
  n = 0.023
FEATURE [App::DocumentObjectGroupPython] O_element057  label="O_element : 0.779"  # scripted group (container) (typed FeaturePython)
  n = 0.779
FEATURE [App::DocumentObjectGroupPython] Na_element010  label="Na_element : 0.097"  # scripted group (container) (typed FeaturePython)
  n = 0.002
FEATURE [App::DocumentObjectGroupPython] P_element006  label="P_element : 0.105"  # scripted group (container) (typed FeaturePython)
  n = 0.001
FEATURE [App::DocumentObjectGroupPython] S_element016  label="S_element : 0.017"  # scripted group (container) (typed FeaturePython)
  n = 0.002
FEATURE [App::DocumentObjectGroupPython] Cl_element014  label="Cl_element : 0.587"  # scripted group (container) (typed FeaturePython)
  n = 0.003
FEATURE [App::DocumentObjectGroupPython] K_element005  label="K_element : 0.015"  # scripted group (container) (typed FeaturePython)
  n = 0.002
FEATURE [App::DocumentObjectGroupPython] G4_LUNG_ICRP  # scripted group (container) (typed FeaturePython)
  Dunit = g/cm3
  Dvalue = 1.04
  Group = -> [H_element051,C_element056,N_element023,O_element057,Na_element010,P_element006,S_element016,Cl_element014,K_element005]
  conduct = 2
  density = 1
  expand = 3
  formula = G4_LUNG_ICRP
  name = G4_LUNG_ICRP
  specific = 4
FEATURE [App::DocumentObjectGroupPython] H_element052  label="H_element : 0.116"  # scripted group (container) (typed FeaturePython)
  n = 0.114318
FEATURE [App::DocumentObjectGroupPython] C_element057  label="C_element : 0.656"  # scripted group (container) (typed FeaturePython)
  n = 0.655824
FEATURE [App::DocumentObjectGroupPython] O_element058  label="O_element : 0.092"  # scripted group (container) (typed FeaturePython)
  n = 0.0921831
FEATURE [App::DocumentObjectGroupPython] Mg_element004  label="Mg_element : 0.135"  # scripted group (container) (typed FeaturePython)
  n = 0.134792
FEATURE [App::DocumentObjectGroupPython] Ca_element013  label="Ca_element : 0.003"  # scripted group (container) (typed FeaturePython)
  n = 0.002883
FEATURE [App::DocumentObjectGroupPython] G4_M3_WAX  # scripted group (container) (typed FeaturePython)
  Dunit = g/cm3
  Dvalue = 1.05
  Group = -> [H_element052,C_element057,O_element058,Mg_element004,Ca_element013]
  conduct = 2
  density = 1
  expand = 3
  formula = G4_M3_WAX
  name = G4_M3_WAX
  specific = 4
FEATURE [App::DocumentObjectGroupPython] Mg_element005  label="Mg_element : 1"  # scripted group (container) (typed FeaturePython)
  n = 1
  ref = Mg_element
FEATURE [App::DocumentObjectGroupPython] C_element058  label="C_element : 031"  # scripted group (container) (typed FeaturePython)
  n = 1
  ref = C_element
FEATURE [App::DocumentObjectGroupPython] O_element059  label="O_element : 030"  # scripted group (container) (typed FeaturePython)
  n = 3
  ref = O_element
FEATURE [App::DocumentObjectGroupPython] G4_MAGNESIUM_CARBONATE  # scripted group (container) (typed FeaturePython)
  Dunit = g/cm3
  Dvalue = 2.958
  Group = -> [Mg_element005,C_element058,O_element059]
  conduct = 2
  density = 1
  expand = 3
  formula = G4_MAGNESIUM_CARBONATE
  name = G4_MAGNESIUM_CARBONATE
  specific = 4
FEATURE [App::DocumentObjectGroupPython] Mg_element006  label="Mg_element : 002"  # scripted group (container) (typed FeaturePython)
  n = 1
  ref = Mg_element
FEATURE [App::DocumentObjectGroupPython] F_element013  label="F_element : 005"  # scripted group (container) (typed FeaturePython)
  n = 2
  ref = F_element
FEATURE [App::DocumentObjectGroupPython] G4_MAGNESIUM_FLUORIDE  # scripted group (container) (typed FeaturePython)
  Dunit = g/cm3
  Dvalue = 3
  Group = -> [Mg_element006,F_element013]
  conduct = 2
  density = 1
  expand = 3
  formula = G4_MAGNESIUM_FLUORIDE
  name = G4_MAGNESIUM_FLUORIDE
  specific = 4
FEATURE [App::DocumentObjectGroupPython] Mg_element007  label="Mg_element : 003"  # scripted group (container) (typed FeaturePython)
  n = 1
  ref = Mg_element
FEATURE [App::DocumentObjectGroupPython] O_element060  label="O_element : 031"  # scripted group (container) (typed FeaturePython)
  n = 1
  ref = O_element
FEATURE [App::DocumentObjectGroupPython] G4_MAGNESIUM_OXIDE  # scripted group (container) (typed FeaturePython)
  Dunit = g/cm3
  Dvalue = 3.58
  Group = -> [Mg_element007,O_element060]
  conduct = 2
  density = 1
  expand = 3
  formula = G4_MAGNESIUM_OXIDE
  name = G4_MAGNESIUM_OXIDE
  specific = 4
FEATURE [App::DocumentObjectGroupPython] Mg_element008  label="Mg_element : 004"  # scripted group (container) (typed FeaturePython)
  n = 1
  ref = Mg_element
FEATURE [App::DocumentObjectGroupPython] B_element006  label="B_element : 006"  # scripted group (container) (typed FeaturePython)
  n = 4
  ref = B_element
FEATURE [App::DocumentObjectGroupPython] O_element061  label="O_element : 032"  # scripted group (container) (typed FeaturePython)
  n = 7
  ref = O_element
FEATURE [App::DocumentObjectGroupPython] G4_MAGNESIUM_TETRABORATE  # scripted group (container) (typed FeaturePython)
  Dunit = g/cm3
  Dvalue = 2.53
  Group = -> [Mg_element008,B_element006,O_element061]
  conduct = 2
  density = 1
  expand = 3
  formula = G4_MAGNESIUM_TETRABORATE
  name = G4_MAGNESIUM_TETRABORATE
  specific = 4
FEATURE [App::DocumentObjectGroupPython] Hg_element001  label="Hg_element : 1"  # scripted group (container) (typed FeaturePython)
  n = 1
  ref = Hg_element
FEATURE [App::DocumentObjectGroupPython] I_element004  label="I_element : 2"  # scripted group (container) (typed FeaturePython)
  n = 2
  ref = I_element
FEATURE [App::DocumentObjectGroupPython] G4_MERCURIC_IODIDE  # scripted group (container) (typed FeaturePython)
  Dunit = g/cm3
  Dvalue = 6.36
  Group = -> [Hg_element001,I_element004]
  conduct = 2
  density = 1
  expand = 3
  formula = G4_MERCURIC_IODIDE
  name = G4_MERCURIC_IODIDE
  specific = 4
FEATURE [App::DocumentObjectGroupPython] C_element059  label="C_element : 032"  # scripted group (container) (typed FeaturePython)
  n = 1
  ref = C_element
FEATURE [App::DocumentObjectGroupPython] H_element053  label="H_element : 028"  # scripted group (container) (typed FeaturePython)
  n = 4
  ref = H_element
FEATURE [App::DocumentObjectGroupPython] G4_METHANE  # scripted group (container) (typed FeaturePython)
  Dunit = g/cm3
  Dvalue = 0.000667151
  Group = -> [C_element059,H_element053]
  conduct = 2
  density = 1
  expand = 3
  formula = G4_METHANE
  name = G4_METHANE
  specific = 4
FEATURE [App::DocumentObjectGroupPython] C_element060  label="C_element : 033"  # scripted group (container) (typed FeaturePython)
  n = 1
  ref = C_element
FEATURE [App::DocumentObjectGroupPython] H_element054  label="H_element : 029"  # scripted group (container) (typed FeaturePython)
  n = 4
  ref = H_element
FEATURE [App::DocumentObjectGroupPython] O_element062  label="O_element : 033"  # scripted group (container) (typed FeaturePython)
  n = 1
  ref = O_element
FEATURE [App::DocumentObjectGroupPython] G4_METHANOL  # scripted group (container) (typed FeaturePython)
  Dunit = g/cm3
  Dvalue = 0.7914
  Group = -> [C_element060,H_element054,O_element062]
  conduct = 2
  density = 1
  expand = 3
  formula = G4_METHANOL
  name = G4_METHANOL
  specific = 4
FEATURE [App::DocumentObjectGroupPython] H_element055  label="H_element : 0.134"  # scripted group (container) (typed FeaturePython)
  n = 0.13404
FEATURE [App::DocumentObjectGroupPython] C_element061  label="C_element : 0.778"  # scripted group (container) (typed FeaturePython)
  n = 0.77796
FEATURE [App::DocumentObjectGroupPython] O_element063  label="O_element : 0.035"  # scripted group (container) (typed FeaturePython)
  n = 0.03502
FEATURE [App::DocumentObjectGroupPython] Mg_element009  label="Mg_element : 0.039"  # scripted group (container) (typed FeaturePython)
  n = 0.038594
FEATURE [App::DocumentObjectGroupPython] Ti_element002  label="Ti_element : 0.014"  # scripted group (container) (typed FeaturePython)
  n = 0.014386
FEATURE [App::DocumentObjectGroupPython] G4_MIX_D_WAX  # scripted group (container) (typed FeaturePython)
  Dunit = g/cm3
  Dvalue = 0.99
  Group = -> [H_element055,C_element061,O_element063,Mg_element009,Ti_element002]
  conduct = 2
  density = 1
  expand = 3
  formula = G4_MIX_D_WAX
  name = G4_MIX_D_WAX
  specific = 4
FEATURE [App::DocumentObjectGroupPython] H_element056  label="H_element : 0.135"  # scripted group (container) (typed FeaturePython)
  n = 0.081192
FEATURE [App::DocumentObjectGroupPython] C_element062  label="C_element : 0.583"  # scripted group (container) (typed FeaturePython)
  n = 0.583442
FEATURE [App::DocumentObjectGroupPython] N_element024  label="N_element : 0.018"  # scripted group (container) (typed FeaturePython)
  n = 0.017798
FEATURE [App::DocumentObjectGroupPython] O_element064  label="O_element : 0.186"  # scripted group (container) (typed FeaturePython)
  n = 0.186381
FEATURE [App::DocumentObjectGroupPython] Mg_element010  label="Mg_element : 0.130"  # scripted group (container) (typed FeaturePython)
  n = 0.130287
FEATURE [App::DocumentObjectGroupPython] Cl_element015  label="Cl_element : 0.588"  # scripted group (container) (typed FeaturePython)
  n = 0.0009
FEATURE [App::DocumentObjectGroupPython] G4_MS20_TISSUE  # scripted group (container) (typed FeaturePython)
  Dunit = g/cm3
  Dvalue = 1
  Group = -> [H_element056,C_element062,N_element024,O_element064,Mg_element010,Cl_element015]
  conduct = 2
  density = 1
  expand = 3
  formula = G4_MS20_TISSUE
  name = G4_MS20_TISSUE
  specific = 4
FEATURE [App::DocumentObjectGroupPython] H_element057  label="H_element : 0.136"  # scripted group (container) (typed FeaturePython)
  n = 0.102
FEATURE [App::DocumentObjectGroupPython] C_element063  label="C_element : 0.143"  # scripted group (container) (typed FeaturePython)
  n = 0.143
FEATURE [App::DocumentObjectGroupPython] N_element025  label="N_element : 0.034"  # scripted group (container) (typed FeaturePython)
  n = 0.034
FEATURE [App::DocumentObjectGroupPython] O_element065  label="O_element : 0.710"  # scripted group (container) (typed FeaturePython)
  n = 0.71
FEATURE [App::DocumentObjectGroupPython] Na_element011  label="Na_element : 0.098"  # scripted group (container) (typed FeaturePython)
  n = 0.001
FEATURE [App::DocumentObjectGroupPython] P_element007  label="P_element : 0.002"  # scripted group (container) (typed FeaturePython)
  n = 0.002
FEATURE [App::DocumentObjectGroupPython] S_element017  label="S_element : 0.018"  # scripted group (container) (typed FeaturePython)
  n = 0.003
FEATURE [App::DocumentObjectGroupPython] Cl_element016  label="Cl_element : 0.589"  # scripted group (container) (typed FeaturePython)
  n = 0.001
FEATURE [App::DocumentObjectGroupPython] K_element006  label="K_element : 0.004"  # scripted group (container) (typed FeaturePython)
  n = 0.004
FEATURE [App::DocumentObjectGroupPython] G4_MUSCLE_SKELETAL_ICRP  # scripted group (container) (typed FeaturePython)
  Dunit = g/cm3
  Dvalue = 1.05
  Group = -> [H_element057,C_element063,N_element025,O_element065,Na_element011,P_element007,S_element017,Cl_element016,K_element006]
  conduct = 2
  density = 1
  expand = 3
  formula = G4_MUSCLE_SKELETAL_ICRP
  name = G4_MUSCLE_SKELETAL_ICRP
  specific = 4
FEATURE [App::DocumentObjectGroupPython] H_element058  label="H_element : 0.137"  # scripted group (container) (typed FeaturePython)
  n = 0.102102
FEATURE [App::DocumentObjectGroupPython] C_element064  label="C_element : 0.123"  # scripted group (container) (typed FeaturePython)
  n = 0.123123
FEATURE [App::DocumentObjectGroupPython] N_element026  label="N_element : 0.756"  # scripted group (container) (typed FeaturePython)
  n = 0.035035
FEATURE [App::DocumentObjectGroupPython] O_element066  label="O_element : 0.730"  # scripted group (container) (typed FeaturePython)
  n = 0.72973
FEATURE [App::DocumentObjectGroupPython] Na_element012  label="Na_element : 0.099"  # scripted group (container) (typed FeaturePython)
  n = 0.001001
FEATURE [App::DocumentObjectGroupPython] P_element008  label="P_element : 0.106"  # scripted group (container) (typed FeaturePython)
  n = 0.002002
FEATURE [App::DocumentObjectGroupPython] S_element018  label="S_element : 0.019"  # scripted group (container) (typed FeaturePython)
  n = 0.004004
FEATURE [App::DocumentObjectGroupPython] K_element007  label="K_element : 0.016"  # scripted group (container) (typed FeaturePython)
  n = 0.003003
FEATURE [App::DocumentObjectGroupPython] G4_MUSCLE_STRIATED_ICRU  # scripted group (container) (typed FeaturePython)
  Dunit = g/cm3
  Dvalue = 1.04
  Group = -> [H_element058,C_element064,N_element026,O_element066,Na_element012,P_element008,S_element018,K_element007]
  conduct = 2
  density = 1
  expand = 3
  formula = G4_MUSCLE_STRIATED_ICRU
  name = G4_MUSCLE_STRIATED_ICRU
  specific = 4
FEATURE [App::DocumentObjectGroupPython] H_element059  label="H_element : 0.098"  # scripted group (container) (typed FeaturePython)
  n = 0.0982341
FEATURE [App::DocumentObjectGroupPython] C_element065  label="C_element : 0.156"  # scripted group (container) (typed FeaturePython)
  n = 0.156214
FEATURE [App::DocumentObjectGroupPython] N_element027  label="N_element : 0.757"  # scripted group (container) (typed FeaturePython)
  n = 0.035451
FEATURE [App::DocumentObjectGroupPython] O_element067  label="O_element : 0.880"  # scripted group (container) (typed FeaturePython)
  n = 0.710101
FEATURE [App::DocumentObjectGroupPython] G4_MUSCLE_WITH_SUCROSE  # scripted group (container) (typed FeaturePython)
  Dunit = g/cm3
  Dvalue = 1.11
  Group = -> [H_element059,C_element065,N_element027,O_element067]
  conduct = 2
  density = 1
  expand = 3
  formula = G4_MUSCLE_WITH_SUCROSE
  name = G4_MUSCLE_WITH_SUCROSE
  specific = 4
FEATURE [App::DocumentObjectGroupPython] H_element060  label="H_element : 0.138"  # scripted group (container) (typed FeaturePython)
  n = 0.101969
FEATURE [App::DocumentObjectGroupPython] C_element066  label="C_element : 0.120"  # scripted group (container) (typed FeaturePython)
  n = 0.120058
FEATURE [App::DocumentObjectGroupPython] N_element028  label="N_element : 0.758"  # scripted group (container) (typed FeaturePython)
  n = 0.035451
FEATURE [App::DocumentObjectGroupPython] O_element068  label="O_element : 0.743"  # scripted group (container) (typed FeaturePython)
  n = 0.742522
FEATURE [App::DocumentObjectGroupPython] G4_MUSCLE_WITHOUT_SUCROSE  # scripted group (container) (typed FeaturePython)
  Dunit = g/cm3
  Dvalue = 1.07
  Group = -> [H_element060,C_element066,N_element028,O_element068]
  conduct = 2
  density = 1
  expand = 3
  formula = G4_MUSCLE_WITHOUT_SUCROSE
  name = G4_MUSCLE_WITHOUT_SUCROSE
  specific = 4
FEATURE [App::DocumentObjectGroupPython] C_element067  label="C_element : 10"  # scripted group (container) (typed FeaturePython)
  n = 10
  ref = C_element
FEATURE [App::DocumentObjectGroupPython] H_element061  label="H_element : 030"  # scripted group (container) (typed FeaturePython)
  n = 8
  ref = H_element
FEATURE [App::DocumentObjectGroupPython] G4_NAPHTHALENE  # scripted group (container) (typed FeaturePython)
  Dunit = g/cm3
  Dvalue = 1.145
  Group = -> [C_element067,H_element061]
  conduct = 2
  density = 1
  expand = 3
  formula = G4_NAPHTHALENE
  name = G4_NAPHTHALENE
  specific = 4
FEATURE [App::DocumentObjectGroupPython] C_element068  label="C_element : 034"  # scripted group (container) (typed FeaturePython)
  n = 6
  ref = C_element
FEATURE [App::DocumentObjectGroupPython] H_element062  label="H_element : 031"  # scripted group (container) (typed FeaturePython)
  n = 5
  ref = H_element
FEATURE [App::DocumentObjectGroupPython] N_element029  label="N_element : 012"  # scripted group (container) (typed FeaturePython)
  n = 1
  ref = N_element
FEATURE [App::DocumentObjectGroupPython] O_element069  label="O_element : 034"  # scripted group (container) (typed FeaturePython)
  n = 2
  ref = O_element
FEATURE [App::DocumentObjectGroupPython] G4_NITROBENZENE  # scripted group (container) (typed FeaturePython)
  Dunit = g/cm3
  Dvalue = 1.19867
  Group = -> [C_element068,H_element062,N_element029,O_element069]
  conduct = 2
  density = 1
  expand = 3
  formula = G4_NITROBENZENE
  name = G4_NITROBENZENE
  specific = 4
FEATURE [App::DocumentObjectGroupPython] N_element030  label="N_element : 013"  # scripted group (container) (typed FeaturePython)
  n = 2
  ref = N_element
FEATURE [App::DocumentObjectGroupPython] O_element070  label="O_element : 035"  # scripted group (container) (typed FeaturePython)
  n = 1
  ref = O_element
FEATURE [App::DocumentObjectGroupPython] G4_NITROUS_OXIDE  # scripted group (container) (typed FeaturePython)
  Dunit = g/cm3
  Dvalue = 0.00183094
  Group = -> [N_element030,O_element070]
  conduct = 2
  density = 1
  expand = 3
  formula = G4_NITROUS_OXIDE
  name = G4_NITROUS_OXIDE
  specific = 4
FEATURE [App::DocumentObjectGroupPython] H_element063  label="H_element : 0.104"  # scripted group (container) (typed FeaturePython)
  n = 0.103509
FEATURE [App::DocumentObjectGroupPython] C_element069  label="C_element : 0.648"  # scripted group (container) (typed FeaturePython)
  n = 0.648416
FEATURE [App::DocumentObjectGroupPython] N_element031  label="N_element : 0.100"  # scripted group (container) (typed FeaturePython)
  n = 0.0995361
FEATURE [App::DocumentObjectGroupPython] O_element071  label="O_element : 0.149"  # scripted group (container) (typed FeaturePython)
  n = 0.148539
FEATURE [App::DocumentObjectGroupPython] G4_NYLON_8062  label="G4_NYLON-8062"  # scripted group (container) (typed FeaturePython)
  Dunit = g/cm3
  Dvalue = 1.08
  Group = -> [H_element063,C_element069,N_element031,O_element071]
  conduct = 2
  density = 1
  expand = 3
  formula = G4_NYLON-8062
  name = G4_NYLON-8062
  specific = 4
FEATURE [App::DocumentObjectGroupPython] C_element070  label="C_element : 035"  # scripted group (container) (typed FeaturePython)
  n = 6
  ref = C_element
FEATURE [App::DocumentObjectGroupPython] H_element064  label="H_element : 11"  # scripted group (container) (typed FeaturePython)
  n = 11
  ref = H_element
FEATURE [App::DocumentObjectGroupPython] N_element032  label="N_element : 014"  # scripted group (container) (typed FeaturePython)
  n = 1
  ref = N_element
FEATURE [App::DocumentObjectGroupPython] O_element072  label="O_element : 036"  # scripted group (container) (typed FeaturePython)
  n = 1
  ref = O_element
FEATURE [App::DocumentObjectGroupPython] G4_NYLON_6_6  label="G4_NYLON-6-6"  # scripted group (container) (typed FeaturePython)
  Dunit = g/cm3
  Dvalue = 1.14
  Group = -> [C_element070,H_element064,N_element032,O_element072]
  conduct = 2
  density = 1
  expand = 3
  formula = G4_NYLON-6-6
  name = G4_NYLON-6-6
  specific = 4
FEATURE [App::DocumentObjectGroupPython] H_element065  label="H_element : 0.139"  # scripted group (container) (typed FeaturePython)
  n = 0.107062
FEATURE [App::DocumentObjectGroupPython] C_element071  label="C_element : 0.680"  # scripted group (container) (typed FeaturePython)
  n = 0.680449
FEATURE [App::DocumentObjectGroupPython] N_element033  label="N_element : 0.099"  # scripted group (container) (typed FeaturePython)
  n = 0.099189
FEATURE [App::DocumentObjectGroupPython] O_element073  label="O_element : 0.113"  # scripted group (container) (typed FeaturePython)
  n = 0.1133
FEATURE [App::DocumentObjectGroupPython] G4_NYLON_6_10  label="G4_NYLON-6-10"  # scripted group (container) (typed FeaturePython)
  Dunit = g/cm3
  Dvalue = 1.14
  Group = -> [H_element065,C_element071,N_element033,O_element073]
  conduct = 2
  density = 1
  expand = 3
  formula = G4_NYLON-6-10
  name = G4_NYLON-6-10
  specific = 4
FEATURE [App::DocumentObjectGroupPython] H_element066  label="H_element : 0.140"  # scripted group (container) (typed FeaturePython)
  n = 0.115476
FEATURE [App::DocumentObjectGroupPython] C_element072  label="C_element : 0.721"  # scripted group (container) (typed FeaturePython)
  n = 0.720818
FEATURE [App::DocumentObjectGroupPython] N_element034  label="N_element : 0.076"  # scripted group (container) (typed FeaturePython)
  n = 0.0764169
FEATURE [App::DocumentObjectGroupPython] O_element074  label="O_element : 0.087"  # scripted group (container) (typed FeaturePython)
  n = 0.0872889
FEATURE [App::DocumentObjectGroupPython] G4_NYLON_11_RILSAN  label="G4_NYLON-11_RILSAN"  # scripted group (container) (typed FeaturePython)
  Dunit = g/cm3
  Dvalue = 1.425
  Group = -> [H_element066,C_element072,N_element034,O_element074]
  conduct = 2
  density = 1
  expand = 3
  formula = G4_NYLON-11_RILSAN
  name = G4_NYLON-11_RILSAN
  specific = 4
FEATURE [App::DocumentObjectGroupPython] C_element073  label="C_element : 8"  # scripted group (container) (typed FeaturePython)
  n = 8
  ref = C_element
FEATURE [App::DocumentObjectGroupPython] H_element067  label="H_element : 18"  # scripted group (container) (typed FeaturePython)
  n = 18
  ref = H_element
FEATURE [App::DocumentObjectGroupPython] G4_OCTANE  # scripted group (container) (typed FeaturePython)
  Dunit = g/cm3
  Dvalue = 0.7026
  Group = -> [C_element073,H_element067]
  conduct = 2
  density = 1
  expand = 3
  formula = G4_OCTANE
  name = G4_OCTANE
  specific = 4
FEATURE [App::DocumentObjectGroupPython] C_element074  label="C_element : 25"  # scripted group (container) (typed FeaturePython)
  n = 25
  ref = C_element
FEATURE [App::DocumentObjectGroupPython] H_element068  label="H_element : 52"  # scripted group (container) (typed FeaturePython)
  n = 52
  ref = H_element
FEATURE [App::DocumentObjectGroupPython] G4_PARAFFIN  # scripted group (container) (typed FeaturePython)
  Dunit = g/cm3
  Dvalue = 0.93
  Group = -> [C_element074,H_element068]
  conduct = 2
  density = 1
  expand = 3
  formula = G4_PARAFFIN
  name = G4_PARAFFIN
  specific = 4
FEATURE [App::DocumentObjectGroupPython] C_element075  label="C_element : 036"  # scripted group (container) (typed FeaturePython)
  n = 5
  ref = C_element
FEATURE [App::DocumentObjectGroupPython] H_element069  label="H_element : 032"  # scripted group (container) (typed FeaturePython)
  n = 12
  ref = H_element
FEATURE [App::DocumentObjectGroupPython] G4_N_PENTANE  label="G4_N-PENTANE"  # scripted group (container) (typed FeaturePython)
  Dunit = g/cm3
  Dvalue = 0.6262
  Group = -> [C_element075,H_element069]
  conduct = 2
  density = 1
  expand = 3
  formula = G4_N-PENTANE
  name = G4_N-PENTANE
  specific = 4
FEATURE [App::DocumentObjectGroupPython] H_element070  label="H_element : 0.014"  # scripted group (container) (typed FeaturePython)
  n = 0.0141
FEATURE [App::DocumentObjectGroupPython] C_element076  label="C_element : 0.072"  # scripted group (container) (typed FeaturePython)
  n = 0.072261
FEATURE [App::DocumentObjectGroupPython] N_element035  label="N_element : 0.019"  # scripted group (container) (typed FeaturePython)
  n = 0.01932
FEATURE [App::DocumentObjectGroupPython] O_element075  label="O_element : 0.066"  # scripted group (container) (typed FeaturePython)
  n = 0.066101
FEATURE [App::DocumentObjectGroupPython] S_element019  label="S_element : 0.020"  # scripted group (container) (typed FeaturePython)
  n = 0.00189
FEATURE [App::DocumentObjectGroupPython] Br_element004  label="Br_element : 0.349"  # scripted group (container) (typed FeaturePython)
  n = 0.349103
FEATURE [App::DocumentObjectGroupPython] Ag_element001  label="Ag_element : 0.474"  # scripted group (container) (typed FeaturePython)
  n = 0.474105
FEATURE [App::DocumentObjectGroupPython] I_element005  label="I_element : 0.003"  # scripted group (container) (typed FeaturePython)
  n = 0.00312
FEATURE [App::DocumentObjectGroupPython] G4_PHOTO_EMULSION  # scripted group (container) (typed FeaturePython)
  Dunit = g/cm3
  Dvalue = 3.815
  Group = -> [H_element070,C_element076,N_element035,O_element075,S_element019,Br_element004,Ag_element001,I_element005]
  conduct = 2
  density = 1
  expand = 3
  formula = G4_PHOTO_EMULSION
  name = G4_PHOTO_EMULSION
  specific = 4
FEATURE [App::DocumentObjectGroupPython] C_element077  label="C_element : 9"  # scripted group (container) (typed FeaturePython)
  n = 9
  ref = C_element
FEATURE [App::DocumentObjectGroupPython] H_element071  label="H_element : 033"  # scripted group (container) (typed FeaturePython)
  n = 10
  ref = H_element
FEATURE [App::DocumentObjectGroupPython] G4_PLASTIC_SC_VINYLTOLUENE  # scripted group (container) (typed FeaturePython)
  Dunit = g/cm3
  Dvalue = 1.032
  Group = -> [C_element077,H_element071]
  conduct = 2
  density = 1
  expand = 3
  formula = G4_PLASTIC_SC_VINYLTOLUENE
  name = G4_PLASTIC_SC_VINYLTOLUENE
  specific = 4
FEATURE [App::DocumentObjectGroupPython] Pu_element001  label="Pu_element : 1"  # scripted group (container) (typed FeaturePython)
  n = 1
  ref = Pu_element
FEATURE [App::DocumentObjectGroupPython] O_element076  label="O_element : 037"  # scripted group (container) (typed FeaturePython)
  n = 2
  ref = O_element
FEATURE [App::DocumentObjectGroupPython] G4_PLUTONIUM_DIOXIDE  # scripted group (container) (typed FeaturePython)
  Dunit = g/cm3
  Dvalue = 11.46
  Group = -> [Pu_element001,O_element076]
  conduct = 2
  density = 1
  expand = 3
  formula = G4_PLUTONIUM_DIOXIDE
  name = G4_PLUTONIUM_DIOXIDE
  specific = 4
FEATURE [App::DocumentObjectGroupPython] C_element078  label="C_element : 037"  # scripted group (container) (typed FeaturePython)
  n = 3
  ref = C_element
FEATURE [App::DocumentObjectGroupPython] H_element072  label="H_element : 034"  # scripted group (container) (typed FeaturePython)
  n = 3
  ref = H_element
FEATURE [App::DocumentObjectGroupPython] N_element036  label="N_element : 015"  # scripted group (container) (typed FeaturePython)
  n = 1
  ref = N_element
FEATURE [App::DocumentObjectGroupPython] G4_POLYACRYLONITRILE  # scripted group (container) (typed FeaturePython)
  Dunit = g/cm3
  Dvalue = 1.17
  Group = -> [C_element078,H_element072,N_element036]
  conduct = 2
  density = 1
  expand = 3
  formula = G4_POLYACRYLONITRILE
  name = G4_POLYACRYLONITRILE
  specific = 4
FEATURE [App::DocumentObjectGroupPython] C_element079  label="C_element : 16"  # scripted group (container) (typed FeaturePython)
  n = 16
  ref = C_element
FEATURE [App::DocumentObjectGroupPython] H_element073  label="H_element : 035"  # scripted group (container) (typed FeaturePython)
  n = 14
  ref = H_element
FEATURE [App::DocumentObjectGroupPython] O_element077  label="O_element : 038"  # scripted group (container) (typed FeaturePython)
  n = 3
  ref = O_element
FEATURE [App::DocumentObjectGroupPython] G4_POLYCARBONATE  # scripted group (container) (typed FeaturePython)
  Dunit = g/cm3
  Dvalue = 1.2
  Group = -> [C_element079,H_element073,O_element077]
  conduct = 2
  density = 1
  expand = 3
  formula = G4_POLYCARBONATE
  name = G4_POLYCARBONATE
  specific = 4
FEATURE [App::DocumentObjectGroupPython] C_element080  label="C_element : 038"  # scripted group (container) (typed FeaturePython)
  n = 8
  ref = C_element
FEATURE [App::DocumentObjectGroupPython] H_element074  label="H_element : 036"  # scripted group (container) (typed FeaturePython)
  n = 7
  ref = H_element
FEATURE [App::DocumentObjectGroupPython] Cl_element017  label="Cl_element : 007"  # scripted group (container) (typed FeaturePython)
  n = 1
  ref = Cl_element
FEATURE [App::DocumentObjectGroupPython] G4_POLYCHLOROSTYRENE  # scripted group (container) (typed FeaturePython)
  Dunit = g/cm3
  Dvalue = 1.3
  Group = -> [C_element080,H_element074,Cl_element017]
  conduct = 2
  density = 1
  expand = 3
  formula = G4_POLYCHLOROSTYRENE
  name = G4_POLYCHLOROSTYRENE
  specific = 4
FEATURE [App::DocumentObjectGroupPython] C_element081  label="C_element : 039"  # scripted group (container) (typed FeaturePython)
  n = 1
  ref = C_element
FEATURE [App::DocumentObjectGroupPython] H_element075  label="H_element : 037"  # scripted group (container) (typed FeaturePython)
  n = 2
  ref = H_element
FEATURE [App::DocumentObjectGroupPython] G4_POLYETHYLENE  # scripted group (container) (typed FeaturePython)
  Dunit = g/cm3
  Dvalue = 0.94
  Group = -> [C_element081,H_element075]
  conduct = 2
  density = 1
  expand = 3
  formula = G4_POLYETHYLENE
  name = G4_POLYETHYLENE
  specific = 4
FEATURE [App::DocumentObjectGroupPython] C_element082  label="C_element : 040"  # scripted group (container) (typed FeaturePython)
  n = 10
  ref = C_element
FEATURE [App::DocumentObjectGroupPython] H_element076  label="H_element : 038"  # scripted group (container) (typed FeaturePython)
  n = 8
  ref = H_element
FEATURE [App::DocumentObjectGroupPython] O_element078  label="O_element : 039"  # scripted group (container) (typed FeaturePython)
  n = 4
  ref = O_element
FEATURE [App::DocumentObjectGroupPython] G4_MYLAR  # scripted group (container) (typed FeaturePython)
  Dunit = g/cm3
  Dvalue = 1.4
  Group = -> [C_element082,H_element076,O_element078]
  conduct = 2
  density = 1
  expand = 3
  formula = G4_MYLAR
  name = G4_MYLAR
  specific = 4
FEATURE [App::DocumentObjectGroupPython] C_element083  label="C_element : 041"  # scripted group (container) (typed FeaturePython)
  n = 5
  ref = C_element
FEATURE [App::DocumentObjectGroupPython] H_element077  label="H_element : 039"  # scripted group (container) (typed FeaturePython)
  n = 8
  ref = H_element
FEATURE [App::DocumentObjectGroupPython] O_element079  label="O_element : 040"  # scripted group (container) (typed FeaturePython)
  n = 2
  ref = O_element
FEATURE [App::DocumentObjectGroupPython] G4_PLEXIGLASS  # scripted group (container) (typed FeaturePython)
  Dunit = g/cm3
  Dvalue = 1.19
  Group = -> [C_element083,H_element077,O_element079]
  conduct = 2
  density = 1
  expand = 3
  formula = G4_PLEXIGLASS
  name = G4_PLEXIGLASS
  specific = 4
FEATURE [App::DocumentObjectGroupPython] C_element084  label="C_element : 042"  # scripted group (container) (typed FeaturePython)
  n = 1
  ref = C_element
FEATURE [App::DocumentObjectGroupPython] H_element078  label="H_element : 040"  # scripted group (container) (typed FeaturePython)
  n = 2
  ref = H_element
FEATURE [App::DocumentObjectGroupPython] O_element080  label="O_element : 041"  # scripted group (container) (typed FeaturePython)
  n = 1
  ref = O_element
FEATURE [App::DocumentObjectGroupPython] G4_POLYOXYMETHYLENE  # scripted group (container) (typed FeaturePython)
  Dunit = g/cm3
  Dvalue = 1.425
  Group = -> [C_element084,H_element078,O_element080]
  conduct = 2
  density = 1
  expand = 3
  formula = G4_POLYOXYMETHYLENE
  name = G4_POLYOXYMETHYLENE
  specific = 4
FEATURE [App::DocumentObjectGroupPython] C_element085  label="C_element : 043"  # scripted group (container) (typed FeaturePython)
  n = 2
  ref = C_element
FEATURE [App::DocumentObjectGroupPython] H_element079  label="H_element : 041"  # scripted group (container) (typed FeaturePython)
  n = 4
  ref = H_element
FEATURE [App::DocumentObjectGroupPython] G4_POLYPROPYLENE  # scripted group (container) (typed FeaturePython)
  Dunit = g/cm3
  Dvalue = 0.9
  Group = -> [C_element085,H_element079]
  conduct = 2
  density = 1
  expand = 3
  formula = G4_POLYPROPYLENE
  name = G4_POLYPROPYLENE
  specific = 4
FEATURE [App::DocumentObjectGroupPython] C_element086  label="C_element : 044"  # scripted group (container) (typed FeaturePython)
  n = 8
  ref = C_element
FEATURE [App::DocumentObjectGroupPython] H_element080  label="H_element : 042"  # scripted group (container) (typed FeaturePython)
  n = 8
  ref = H_element
FEATURE [App::DocumentObjectGroupPython] G4_POLYSTYRENE  # scripted group (container) (typed FeaturePython)
  Dunit = g/cm3
  Dvalue = 1.06
  Group = -> [C_element086,H_element080]
  conduct = 2
  density = 1
  expand = 3
  formula = G4_POLYSTYRENE
  name = G4_POLYSTYRENE
  specific = 4
FEATURE [App::DocumentObjectGroupPython] C_element087  label="C_element : 045"  # scripted group (container) (typed FeaturePython)
  n = 2
  ref = C_element
FEATURE [App::DocumentObjectGroupPython] F_element014  label="F_element : 4"  # scripted group (container) (typed FeaturePython)
  n = 4
  ref = F_element
FEATURE [App::DocumentObjectGroupPython] G4_TEFLON  # scripted group (container) (typed FeaturePython)
  Dunit = g/cm3
  Dvalue = 2.2
  Group = -> [C_element087,F_element014]
  conduct = 2
  density = 1
  expand = 3
  formula = G4_TEFLON
  name = G4_TEFLON
  specific = 4
FEATURE [App::DocumentObjectGroupPython] C_element088  label="C_element : 046"  # scripted group (container) (typed FeaturePython)
  n = 2
  ref = C_element
FEATURE [App::DocumentObjectGroupPython] F_element015  label="F_element : 006"  # scripted group (container) (typed FeaturePython)
  n = 3
  ref = F_element
FEATURE [App::DocumentObjectGroupPython] Cl_element018  label="Cl_element : 008"  # scripted group (container) (typed FeaturePython)
  n = 1
  ref = Cl_element
FEATURE [App::DocumentObjectGroupPython] G4_POLYTRIFLUOROCHLOROETHYLENE  # scripted group (container) (typed FeaturePython)
  Dunit = g/cm3
  Dvalue = 2.1
  Group = -> [C_element088,F_element015,Cl_element018]
  conduct = 2
  density = 1
  expand = 3
  formula = G4_POLYTRIFLUOROCHLOROETHYLENE
  name = G4_POLYTRIFLUOROCHLOROETHYLENE
  specific = 4
FEATURE [App::DocumentObjectGroupPython] C_element089  label="C_element : 047"  # scripted group (container) (typed FeaturePython)
  n = 4
  ref = C_element
FEATURE [App::DocumentObjectGroupPython] H_element081  label="H_element : 043"  # scripted group (container) (typed FeaturePython)
  n = 6
  ref = H_element
FEATURE [App::DocumentObjectGroupPython] O_element081  label="O_element : 042"  # scripted group (container) (typed FeaturePython)
  n = 2
  ref = O_element
FEATURE [App::DocumentObjectGroupPython] G4_POLYVINYL_ACETATE  # scripted group (container) (typed FeaturePython)
  Dunit = g/cm3
  Dvalue = 1.19
  Group = -> [C_element089,H_element081,O_element081]
  conduct = 2
  density = 1
  expand = 3
  formula = G4_POLYVINYL_ACETATE
  name = G4_POLYVINYL_ACETATE
  specific = 4
FEATURE [App::DocumentObjectGroupPython] C_element090  label="C_element : 048"  # scripted group (container) (typed FeaturePython)
  n = 2
  ref = C_element
FEATURE [App::DocumentObjectGroupPython] H_element082  label="H_element : 044"  # scripted group (container) (typed FeaturePython)
  n = 4
  ref = H_element
FEATURE [App::DocumentObjectGroupPython] O_element082  label="O_element : 043"  # scripted group (container) (typed FeaturePython)
  n = 1
  ref = O_element
FEATURE [App::DocumentObjectGroupPython] G4_POLYVINYL_ALCOHOL  # scripted group (container) (typed FeaturePython)
  Dunit = g/cm3
  Dvalue = 1.3
  Group = -> [C_element090,H_element082,O_element082]
  conduct = 2
  density = 1
  expand = 3
  formula = G4_POLYVINYL_ALCOHOL
  name = G4_POLYVINYL_ALCOHOL
  specific = 4
FEATURE [App::DocumentObjectGroupPython] C_element091  label="C_element : 049"  # scripted group (container) (typed FeaturePython)
  n = 8
  ref = C_element
FEATURE [App::DocumentObjectGroupPython] H_element083  label="H_element : 045"  # scripted group (container) (typed FeaturePython)
  n = 14
  ref = H_element
FEATURE [App::DocumentObjectGroupPython] O_element083  label="O_element : 044"  # scripted group (container) (typed FeaturePython)
  n = 2
  ref = O_element
FEATURE [App::DocumentObjectGroupPython] G4_POLYVINYL_BUTYRAL  # scripted group (container) (typed FeaturePython)
  Dunit = g/cm3
  Dvalue = 1.12
  Group = -> [C_element091,H_element083,O_element083]
  conduct = 2
  density = 1
  expand = 3
  formula = G4_POLYVINYL_BUTYRAL
  name = G4_POLYVINYL_BUTYRAL
  specific = 4
FEATURE [App::DocumentObjectGroupPython] C_element092  label="C_element : 050"  # scripted group (container) (typed FeaturePython)
  n = 2
  ref = C_element
FEATURE [App::DocumentObjectGroupPython] H_element084  label="H_element : 046"  # scripted group (container) (typed FeaturePython)
  n = 3
  ref = H_element
FEATURE [App::DocumentObjectGroupPython] Cl_element019  label="Cl_element : 009"  # scripted group (container) (typed FeaturePython)
  n = 1
  ref = Cl_element
FEATURE [App::DocumentObjectGroupPython] G4_POLYVINYL_CHLORIDE  # scripted group (container) (typed FeaturePython)
  Dunit = g/cm3
  Dvalue = 1.3
  Group = -> [C_element092,H_element084,Cl_element019]
  conduct = 2
  density = 1
  expand = 3
  formula = G4_POLYVINYL_CHLORIDE
  name = G4_POLYVINYL_CHLORIDE
  specific = 4
FEATURE [App::DocumentObjectGroupPython] C_element093  label="C_element : 051"  # scripted group (container) (typed FeaturePython)
  n = 2
  ref = C_element
FEATURE [App::DocumentObjectGroupPython] H_element085  label="H_element : 047"  # scripted group (container) (typed FeaturePython)
  n = 2
  ref = H_element
FEATURE [App::DocumentObjectGroupPython] Cl_element020  label="Cl_element : 010"  # scripted group (container) (typed FeaturePython)
  n = 2
  ref = Cl_element
FEATURE [App::DocumentObjectGroupPython] G4_POLYVINYLIDENE_CHLORIDE  # scripted group (container) (typed FeaturePython)
  Dunit = g/cm3
  Dvalue = 1.7
  Group = -> [C_element093,H_element085,Cl_element020]
  conduct = 2
  density = 1
  expand = 3
  formula = G4_POLYVINYLIDENE_CHLORIDE
  name = G4_POLYVINYLIDENE_CHLORIDE
  specific = 4
FEATURE [App::DocumentObjectGroupPython] C_element094  label="C_element : 052"  # scripted group (container) (typed FeaturePython)
  n = 2
  ref = C_element
FEATURE [App::DocumentObjectGroupPython] H_element086  label="H_element : 048"  # scripted group (container) (typed FeaturePython)
  n = 2
  ref = H_element
FEATURE [App::DocumentObjectGroupPython] F_element016  label="F_element : 007"  # scripted group (container) (typed FeaturePython)
  n = 2
  ref = F_element
FEATURE [App::DocumentObjectGroupPython] G4_POLYVINYLIDENE_FLUORIDE  # scripted group (container) (typed FeaturePython)
  Dunit = g/cm3
  Dvalue = 1.76
  Group = -> [C_element094,H_element086,F_element016]
  conduct = 2
  density = 1
  expand = 3
  formula = G4_POLYVINYLIDENE_FLUORIDE
  name = G4_POLYVINYLIDENE_FLUORIDE
  specific = 4
FEATURE [App::DocumentObjectGroupPython] C_element095  label="C_element : 053"  # scripted group (container) (typed FeaturePython)
  n = 6
  ref = C_element
FEATURE [App::DocumentObjectGroupPython] H_element087  label="H_element : 9"  # scripted group (container) (typed FeaturePython)
  n = 9
  ref = H_element
FEATURE [App::DocumentObjectGroupPython] N_element037  label="N_element : 016"  # scripted group (container) (typed FeaturePython)
  n = 1
  ref = N_element
FEATURE [App::DocumentObjectGroupPython] O_element084  label="O_element : 045"  # scripted group (container) (typed FeaturePython)
  n = 1
  ref = O_element
FEATURE [App::DocumentObjectGroupPython] G4_POLYVINYL_PYRROLIDONE  # scripted group (container) (typed FeaturePython)
  Dunit = g/cm3
  Dvalue = 1.25
  Group = -> [C_element095,H_element087,N_element037,O_element084]
  conduct = 2
  density = 1
  expand = 3
  formula = G4_POLYVINYL_PYRROLIDONE
  name = G4_POLYVINYL_PYRROLIDONE
  specific = 4
FEATURE [App::DocumentObjectGroupPython] K_element008  label="K_element : 1"  # scripted group (container) (typed FeaturePython)
  n = 1
  ref = K_element
FEATURE [App::DocumentObjectGroupPython] I_element006  label="I_element : 003"  # scripted group (container) (typed FeaturePython)
  n = 1
  ref = I_element
FEATURE [App::DocumentObjectGroupPython] G4_POTASSIUM_IODIDE  # scripted group (container) (typed FeaturePython)
  Dunit = g/cm3
  Dvalue = 3.13
  Group = -> [K_element008,I_element006]
  conduct = 2
  density = 1
  expand = 3
  formula = G4_POTASSIUM_IODIDE
  name = G4_POTASSIUM_IODIDE
  specific = 4
FEATURE [App::DocumentObjectGroupPython] K_element009  label="K_element : 2"  # scripted group (container) (typed FeaturePython)
  n = 2
  ref = K_element
FEATURE [App::DocumentObjectGroupPython] O_element085  label="O_element : 046"  # scripted group (container) (typed FeaturePython)
  n = 1
  ref = O_element
FEATURE [App::DocumentObjectGroupPython] G4_POTASSIUM_OXIDE  # scripted group (container) (typed FeaturePython)
  Dunit = g/cm3
  Dvalue = 2.32
  Group = -> [K_element009,O_element085]
  conduct = 2
  density = 1
  expand = 3
  formula = G4_POTASSIUM_OXIDE
  name = G4_POTASSIUM_OXIDE
  specific = 4
FEATURE [App::DocumentObjectGroupPython] C_element096  label="C_element : 054"  # scripted group (container) (typed FeaturePython)
  n = 3
  ref = C_element
FEATURE [App::DocumentObjectGroupPython] H_element088  label="H_element : 049"  # scripted group (container) (typed FeaturePython)
  n = 8
  ref = H_element
FEATURE [App::DocumentObjectGroupPython] G4_PROPANE  # scripted group (container) (typed FeaturePython)
  Dunit = g/cm3
  Dvalue = 0.00187939
  Group = -> [C_element096,H_element088]
  conduct = 2
  density = 1
  expand = 3
  formula = G4_PROPANE
  name = G4_PROPANE
  specific = 4
FEATURE [App::DocumentObjectGroupPython] C_element097  label="C_element : 055"  # scripted group (container) (typed FeaturePython)
  n = 3
  ref = C_element
FEATURE [App::DocumentObjectGroupPython] H_element089  label="H_element : 050"  # scripted group (container) (typed FeaturePython)
  n = 8
  ref = H_element
FEATURE [App::DocumentObjectGroupPython] G4_lPROPANE  # scripted group (container) (typed FeaturePython)
  Dunit = g/cm3
  Dvalue = 0.43
  Group = -> [C_element097,H_element089]
  conduct = 2
  density = 1
  expand = 3
  formula = G4_lPROPANE
  name = G4_lPROPANE
  specific = 4
FEATURE [App::DocumentObjectGroupPython] C_element098  label="C_element : 056"  # scripted group (container) (typed FeaturePython)
  n = 3
  ref = C_element
FEATURE [App::DocumentObjectGroupPython] H_element090  label="H_element : 051"  # scripted group (container) (typed FeaturePython)
  n = 8
  ref = H_element
FEATURE [App::DocumentObjectGroupPython] O_element086  label="O_element : 047"  # scripted group (container) (typed FeaturePython)
  n = 1
  ref = O_element
FEATURE [App::DocumentObjectGroupPython] G4_N_PROPYL_ALCOHOL  label="G4_N-PROPYL_ALCOHOL"  # scripted group (container) (typed FeaturePython)
  Dunit = g/cm3
  Dvalue = 0.8035
  Group = -> [C_element098,H_element090,O_element086]
  conduct = 2
  density = 1
  expand = 3
  formula = G4_N-PROPYL_ALCOHOL
  name = G4_N-PROPYL_ALCOHOL
  specific = 4
FEATURE [App::DocumentObjectGroupPython] C_element099  label="C_element : 057"  # scripted group (container) (typed FeaturePython)
  n = 5
  ref = C_element
FEATURE [App::DocumentObjectGroupPython] H_element091  label="H_element : 052"  # scripted group (container) (typed FeaturePython)
  n = 5
  ref = H_element
FEATURE [App::DocumentObjectGroupPython] N_element038  label="N_element : 017"  # scripted group (container) (typed FeaturePython)
  n = 1
  ref = N_element
FEATURE [App::DocumentObjectGroupPython] G4_PYRIDINE  # scripted group (container) (typed FeaturePython)
  Dunit = g/cm3
  Dvalue = 0.9819
  Group = -> [C_element099,H_element091,N_element038]
  conduct = 2
  density = 1
  expand = 3
  formula = G4_PYRIDINE
  name = G4_PYRIDINE
  specific = 4
FEATURE [App::DocumentObjectGroupPython] H_element092  label="H_element : 0.144"  # scripted group (container) (typed FeaturePython)
  n = 0.143711
FEATURE [App::DocumentObjectGroupPython] C_element100  label="C_element : 0.856"  # scripted group (container) (typed FeaturePython)
  n = 0.856289
FEATURE [App::DocumentObjectGroupPython] G4_RUBBER_BUTYL  # scripted group (container) (typed FeaturePython)
  Dunit = g/cm3
  Dvalue = 0.92
  Group = -> [H_element092,C_element100]
  conduct = 2
  density = 1
  expand = 3
  formula = G4_RUBBER_BUTYL
  name = G4_RUBBER_BUTYL
  specific = 4
FEATURE [App::DocumentObjectGroupPython] H_element093  label="H_element : 0.118"  # scripted group (container) (typed FeaturePython)
  n = 0.118371
FEATURE [App::DocumentObjectGroupPython] C_element101  label="C_element : 0.882"  # scripted group (container) (typed FeaturePython)
  n = 0.881629
FEATURE [App::DocumentObjectGroupPython] G4_RUBBER_NATURAL  # scripted group (container) (typed FeaturePython)
  Dunit = g/cm3
  Dvalue = 0.92
  Group = -> [H_element093,C_element101]
  conduct = 2
  density = 1
  expand = 3
  formula = G4_RUBBER_NATURAL
  name = G4_RUBBER_NATURAL
  specific = 4
FEATURE [App::DocumentObjectGroupPython] H_element094  label="H_element : 0.145"  # scripted group (container) (typed FeaturePython)
  n = 0.05692
FEATURE [App::DocumentObjectGroupPython] C_element102  label="C_element : 0.543"  # scripted group (container) (typed FeaturePython)
  n = 0.542646
FEATURE [App::DocumentObjectGroupPython] Cl_element021  label="Cl_element : 0.400"  # scripted group (container) (typed FeaturePython)
  n = 0.400434
FEATURE [App::DocumentObjectGroupPython] G4_RUBBER_NEOPRENE  # scripted group (container) (typed FeaturePython)
  Dunit = g/cm3
  Dvalue = 1.23
  Group = -> [H_element094,C_element102,Cl_element021]
  conduct = 2
  density = 1
  expand = 3
  formula = G4_RUBBER_NEOPRENE
  name = G4_RUBBER_NEOPRENE
  specific = 4
FEATURE [App::DocumentObjectGroupPython] Si_element006  label="Si_element : 1"  # scripted group (container) (typed FeaturePython)
  n = 1
  ref = Si_element
FEATURE [App::DocumentObjectGroupPython] O_element087  label="O_element : 048"  # scripted group (container) (typed FeaturePython)
  n = 2
  ref = O_element
FEATURE [App::DocumentObjectGroupPython] G4_SILICON_DIOXIDE  # scripted group (container) (typed FeaturePython)
  Dunit = g/cm3
  Dvalue = 2.32
  Group = -> [Si_element006,O_element087]
  conduct = 2
  density = 1
  expand = 3
  formula = G4_SILICON_DIOXIDE
  name = G4_SILICON_DIOXIDE
  specific = 4
FEATURE [App::DocumentObjectGroupPython] Ag_element002  label="Ag_element : 1"  # scripted group (container) (typed FeaturePython)
  n = 1
  ref = Ag_element
FEATURE [App::DocumentObjectGroupPython] Br_element005  label="Br_element : 003"  # scripted group (container) (typed FeaturePython)
  n = 1
  ref = Br_element
FEATURE [App::DocumentObjectGroupPython] G4_SILVER_BROMIDE  # scripted group (container) (typed FeaturePython)
  Dunit = g/cm3
  Dvalue = 6.473
  Group = -> [Ag_element002,Br_element005]
  conduct = 2
  density = 1
  expand = 3
  formula = G4_SILVER_BROMIDE
  name = G4_SILVER_BROMIDE
  specific = 4
FEATURE [App::DocumentObjectGroupPython] Ag_element003  label="Ag_element : 002"  # scripted group (container) (typed FeaturePython)
  n = 1
  ref = Ag_element
FEATURE [App::DocumentObjectGroupPython] Cl_element022  label="Cl_element : 011"  # scripted group (container) (typed FeaturePython)
  n = 1
  ref = Cl_element
FEATURE [App::DocumentObjectGroupPython] G4_SILVER_CHLORIDE  # scripted group (container) (typed FeaturePython)
  Dunit = g/cm3
  Dvalue = 5.56
  Group = -> [Ag_element003,Cl_element022]
  conduct = 2
  density = 1
  expand = 3
  formula = G4_SILVER_CHLORIDE
  name = G4_SILVER_CHLORIDE
  specific = 4
FEATURE [App::DocumentObjectGroupPython] Br_element006  label="Br_element : 0.423"  # scripted group (container) (typed FeaturePython)
  n = 0.422895
FEATURE [App::DocumentObjectGroupPython] Ag_element004  label="Ag_element : 0.574"  # scripted group (container) (typed FeaturePython)
  n = 0.573748
FEATURE [App::DocumentObjectGroupPython] I_element007  label="I_element : 0.649"  # scripted group (container) (typed FeaturePython)
  n = 0.003357
FEATURE [App::DocumentObjectGroupPython] G4_SILVER_HALIDES  # scripted group (container) (typed FeaturePython)
  Dunit = g/cm3
  Dvalue = 6.47
  Group = -> [Br_element006,Ag_element004,I_element007]
  conduct = 2
  density = 1
  expand = 3
  formula = G4_SILVER_HALIDES
  name = G4_SILVER_HALIDES
  specific = 4
FEATURE [App::DocumentObjectGroupPython] Ag_element005  label="Ag_element : 003"  # scripted group (container) (typed FeaturePython)
  n = 1
  ref = Ag_element
FEATURE [App::DocumentObjectGroupPython] I_element008  label="I_element : 004"  # scripted group (container) (typed FeaturePython)
  n = 1
  ref = I_element
FEATURE [App::DocumentObjectGroupPython] G4_SILVER_IODIDE  # scripted group (container) (typed FeaturePython)
  Dunit = g/cm3
  Dvalue = 6.01
  Group = -> [Ag_element005,I_element008]
  conduct = 2
  density = 1
  expand = 3
  formula = G4_SILVER_IODIDE
  name = G4_SILVER_IODIDE
  specific = 4
FEATURE [App::DocumentObjectGroupPython] H_element095  label="H_element : 0.100"  # scripted group (container) (typed FeaturePython)
  n = 0.1
FEATURE [App::DocumentObjectGroupPython] C_element103  label="C_element : 0.204"  # scripted group (container) (typed FeaturePython)
  n = 0.204
FEATURE [App::DocumentObjectGroupPython] N_element039  label="N_element : 0.759"  # scripted group (container) (typed FeaturePython)
  n = 0.042
FEATURE [App::DocumentObjectGroupPython] O_element088  label="O_element : 0.645"  # scripted group (container) (typed FeaturePython)
  n = 0.645
FEATURE [App::DocumentObjectGroupPython] Na_element013  label="Na_element : 0.100"  # scripted group (container) (typed FeaturePython)
  n = 0.002
FEATURE [App::DocumentObjectGroupPython] P_element009  label="P_element : 0.107"  # scripted group (container) (typed FeaturePython)
  n = 0.001
FEATURE [App::DocumentObjectGroupPython] S_element020  label="S_element : 0.021"  # scripted group (container) (typed FeaturePython)
  n = 0.002
FEATURE [App::DocumentObjectGroupPython] Cl_element023  label="Cl_element : 0.590"  # scripted group (container) (typed FeaturePython)
  n = 0.003
FEATURE [App::DocumentObjectGroupPython] K_element010  label="K_element : 0.001"  # scripted group (container) (typed FeaturePython)
  n = 0.001
FEATURE [App::DocumentObjectGroupPython] G4_SKIN_ICRP  # scripted group (container) (typed FeaturePython)
  Dunit = g/cm3
  Dvalue = 1.09
  Group = -> [H_element095,C_element103,N_element039,O_element088,Na_element013,P_element009,S_element020,Cl_element023,K_element010]
  conduct = 2
  density = 1
  expand = 3
  formula = G4_SKIN_ICRP
  name = G4_SKIN_ICRP
  specific = 4
FEATURE [App::DocumentObjectGroupPython] Na_element014  label="Na_element : 2"  # scripted group (container) (typed FeaturePython)
  n = 2
  ref = Na_element
FEATURE [App::DocumentObjectGroupPython] C_element104  label="C_element : 058"  # scripted group (container) (typed FeaturePython)
  n = 1
  ref = C_element
FEATURE [App::DocumentObjectGroupPython] O_element089  label="O_element : 049"  # scripted group (container) (typed FeaturePython)
  n = 3
  ref = O_element
FEATURE [App::DocumentObjectGroupPython] G4_SODIUM_CARBONATE  # scripted group (container) (typed FeaturePython)
  Dunit = g/cm3
  Dvalue = 2.532
  Group = -> [Na_element014,C_element104,O_element089]
  conduct = 2
  density = 1
  expand = 3
  formula = G4_SODIUM_CARBONATE
  name = G4_SODIUM_CARBONATE
  specific = 4
FEATURE [App::DocumentObjectGroupPython] Na_element015  label="Na_element : 1"  # scripted group (container) (typed FeaturePython)
  n = 1
  ref = Na_element
FEATURE [App::DocumentObjectGroupPython] I_element009  label="I_element : 005"  # scripted group (container) (typed FeaturePython)
  n = 1
  ref = I_element
FEATURE [App::DocumentObjectGroupPython] G4_SODIUM_IODIDE  # scripted group (container) (typed FeaturePython)
  Dunit = g/cm3
  Dvalue = 3.667
  Group = -> [Na_element015,I_element009]
  conduct = 2
  density = 1
  expand = 3
  formula = G4_SODIUM_IODIDE
  name = G4_SODIUM_IODIDE
  specific = 4
FEATURE [App::DocumentObjectGroupPython] Na_element016  label="Na_element : 003"  # scripted group (container) (typed FeaturePython)
  n = 2
  ref = Na_element
FEATURE [App::DocumentObjectGroupPython] O_element090  label="O_element : 050"  # scripted group (container) (typed FeaturePython)
  n = 1
  ref = O_element
FEATURE [App::DocumentObjectGroupPython] G4_SODIUM_MONOXIDE  # scripted group (container) (typed FeaturePython)
  Dunit = g/cm3
  Dvalue = 2.27
  Group = -> [Na_element016,O_element090]
  conduct = 2
  density = 1
  expand = 3
  formula = G4_SODIUM_MONOXIDE
  name = G4_SODIUM_MONOXIDE
  specific = 4
FEATURE [App::DocumentObjectGroupPython] Na_element017  label="Na_element : 004"  # scripted group (container) (typed FeaturePython)
  n = 1
  ref = Na_element
FEATURE [App::DocumentObjectGroupPython] N_element040  label="N_element : 018"  # scripted group (container) (typed FeaturePython)
  n = 1
  ref = N_element
FEATURE [App::DocumentObjectGroupPython] O_element091  label="O_element : 051"  # scripted group (container) (typed FeaturePython)
  n = 3
  ref = O_element
FEATURE [App::DocumentObjectGroupPython] G4_SODIUM_NITRATE  # scripted group (container) (typed FeaturePython)
  Dunit = g/cm3
  Dvalue = 2.261
  Group = -> [Na_element017,N_element040,O_element091]
  conduct = 2
  density = 1
  expand = 3
  formula = G4_SODIUM_NITRATE
  name = G4_SODIUM_NITRATE
  specific = 4
FEATURE [App::DocumentObjectGroupPython] C_element105  label="C_element : 059"  # scripted group (container) (typed FeaturePython)
  n = 14
  ref = C_element
FEATURE [App::DocumentObjectGroupPython] H_element096  label="H_element : 053"  # scripted group (container) (typed FeaturePython)
  n = 12
  ref = H_element
FEATURE [App::DocumentObjectGroupPython] G4_STILBENE  # scripted group (container) (typed FeaturePython)
  Dunit = g/cm3
  Dvalue = 0.9707
  Group = -> [C_element105,H_element096]
  conduct = 2
  density = 1
  expand = 3
  formula = G4_STILBENE
  name = G4_STILBENE
  specific = 4
FEATURE [App::DocumentObjectGroupPython] C_element106  label="C_element : 12"  # scripted group (container) (typed FeaturePython)
  n = 12
  ref = C_element
FEATURE [App::DocumentObjectGroupPython] H_element097  label="H_element : 22"  # scripted group (container) (typed FeaturePython)
  n = 22
  ref = H_element
FEATURE [App::DocumentObjectGroupPython] O_element092  label="O_element : 11"  # scripted group (container) (typed FeaturePython)
  n = 11
  ref = O_element
FEATURE [App::DocumentObjectGroupPython] G4_SUCROSE  # scripted group (container) (typed FeaturePython)
  Dunit = g/cm3
  Dvalue = 1.5805
  Group = -> [C_element106,H_element097,O_element092]
  conduct = 2
  density = 1
  expand = 3
  formula = G4_SUCROSE
  name = G4_SUCROSE
  specific = 4
FEATURE [App::DocumentObjectGroupPython] C_element107  label="C_element : 18"  # scripted group (container) (typed FeaturePython)
  n = 18
  ref = C_element
FEATURE [App::DocumentObjectGroupPython] H_element098  label="H_element : 054"  # scripted group (container) (typed FeaturePython)
  n = 14
  ref = H_element
FEATURE [App::DocumentObjectGroupPython] G4_TERPHENYL  # scripted group (container) (typed FeaturePython)
  Dunit = g/cm3
  Dvalue = 1.24
  Group = -> [C_element107,H_element098]
  conduct = 2
  density = 1
  expand = 3
  formula = G4_TERPHENYL
  name = G4_TERPHENYL
  specific = 4
FEATURE [App::DocumentObjectGroupPython] H_element099  label="H_element : 0.146"  # scripted group (container) (typed FeaturePython)
  n = 0.106
FEATURE [App::DocumentObjectGroupPython] C_element108  label="C_element : 0.883"  # scripted group (container) (typed FeaturePython)
  n = 0.099
FEATURE [App::DocumentObjectGroupPython] N_element041  label="N_element : 0.020"  # scripted group (container) (typed FeaturePython)
  n = 0.02
FEATURE [App::DocumentObjectGroupPython] O_element093  label="O_element : 0.766"  # scripted group (container) (typed FeaturePython)
  n = 0.766
FEATURE [App::DocumentObjectGroupPython] Na_element018  label="Na_element : 0.101"  # scripted group (container) (typed FeaturePython)
  n = 0.002
FEATURE [App::DocumentObjectGroupPython] P_element010  label="P_element : 0.108"  # scripted group (container) (typed FeaturePython)
  n = 0.001
FEATURE [App::DocumentObjectGroupPython] S_element021  label="S_element : 0.022"  # scripted group (container) (typed FeaturePython)
  n = 0.002
FEATURE [App::DocumentObjectGroupPython] Cl_element024  label="Cl_element : 0.002"  # scripted group (container) (typed FeaturePython)
  n = 0.002
FEATURE [App::DocumentObjectGroupPython] K_element011  label="K_element : 0.017"  # scripted group (container) (typed FeaturePython)
  n = 0.002
FEATURE [App::DocumentObjectGroupPython] G4_TESTIS_ICRP  # scripted group (container) (typed FeaturePython)
  Dunit = g/cm3
  Dvalue = 1.04
  Group = -> [H_element099,C_element108,N_element041,O_element093,Na_element018,P_element010,S_element021,Cl_element024,K_element011]
  conduct = 2
  density = 1
  expand = 3
  formula = G4_TESTIS_ICRP
  name = G4_TESTIS_ICRP
  specific = 4
FEATURE [App::DocumentObjectGroupPython] C_element109  label="C_element : 060"  # scripted group (container) (typed FeaturePython)
  n = 2
  ref = C_element
FEATURE [App::DocumentObjectGroupPython] Cl_element025  label="Cl_element : 012"  # scripted group (container) (typed FeaturePython)
  n = 4
  ref = Cl_element
FEATURE [App::DocumentObjectGroupPython] G4_TETRACHLOROETHYLENE  # scripted group (container) (typed FeaturePython)
  Dunit = g/cm3
  Dvalue = 1.625
  Group = -> [C_element109,Cl_element025]
  conduct = 2
  density = 1
  expand = 3
  formula = G4_TETRACHLOROETHYLENE
  name = G4_TETRACHLOROETHYLENE
  specific = 4
FEATURE [App::DocumentObjectGroupPython] Tl_element001  label="Tl_element : 1"  # scripted group (container) (typed FeaturePython)
  n = 1
  ref = Tl_element
FEATURE [App::DocumentObjectGroupPython] Cl_element026  label="Cl_element : 013"  # scripted group (container) (typed FeaturePython)
  n = 1
  ref = Cl_element
FEATURE [App::DocumentObjectGroupPython] G4_THALLIUM_CHLORIDE  # scripted group (container) (typed FeaturePython)
  Dunit = g/cm3
  Dvalue = 7.004
  Group = -> [Tl_element001,Cl_element026]
  conduct = 2
  density = 1
  expand = 3
  formula = G4_THALLIUM_CHLORIDE
  name = G4_THALLIUM_CHLORIDE
  specific = 4
FEATURE [App::DocumentObjectGroupPython] H_element100  label="H_element : 0.147"  # scripted group (container) (typed FeaturePython)
  n = 0.105
FEATURE [App::DocumentObjectGroupPython] C_element110  label="C_element : 0.256"  # scripted group (container) (typed FeaturePython)
  n = 0.256
FEATURE [App::DocumentObjectGroupPython] N_element042  label="N_element : 0.760"  # scripted group (container) (typed FeaturePython)
  n = 0.027
FEATURE [App::DocumentObjectGroupPython] O_element094  label="O_element : 0.602"  # scripted group (container) (typed FeaturePython)
  n = 0.602
FEATURE [App::DocumentObjectGroupPython] Na_element019  label="Na_element : 0.102"  # scripted group (container) (typed FeaturePython)
  n = 0.001
FEATURE [App::DocumentObjectGroupPython] P_element011  label="P_element : 0.109"  # scripted group (container) (typed FeaturePython)
  n = 0.002
FEATURE [App::DocumentObjectGroupPython] S_element022  label="S_element : 0.023"  # scripted group (container) (typed FeaturePython)
  n = 0.003
FEATURE [App::DocumentObjectGroupPython] Cl_element027  label="Cl_element : 0.591"  # scripted group (container) (typed FeaturePython)
  n = 0.002
FEATURE [App::DocumentObjectGroupPython] K_element012  label="K_element : 0.018"  # scripted group (container) (typed FeaturePython)
  n = 0.002
FEATURE [App::DocumentObjectGroupPython] G4_TISSUE_SOFT_ICRP  # scripted group (container) (typed FeaturePython)
  Dunit = g/cm3
  Dvalue = 1.03
  Group = -> [H_element100,C_element110,N_element042,O_element094,Na_element019,P_element011,S_element022,Cl_element027,K_element012]
  conduct = 2
  density = 1
  expand = 3
  formula = G4_TISSUE_SOFT_ICRP
  name = G4_TISSUE_SOFT_ICRP
  specific = 4
FEATURE [App::DocumentObjectGroupPython] H_element101  label="H_element : 0.148"  # scripted group (container) (typed FeaturePython)
  n = 0.101
FEATURE [App::DocumentObjectGroupPython] C_element111  label="C_element : 0.111"  # scripted group (container) (typed FeaturePython)
  n = 0.111
FEATURE [App::DocumentObjectGroupPython] N_element043  label="N_element : 0.026"  # scripted group (container) (typed FeaturePython)
  n = 0.026
FEATURE [App::DocumentObjectGroupPython] O_element095  label="O_element : 0.762"  # scripted group (container) (typed FeaturePython)
  n = 0.762
FEATURE [App::DocumentObjectGroupPython] G4_TISSUE_SOFT_ICRU_4  label="G4_TISSUE_SOFT_ICRU-4"  # scripted group (container) (typed FeaturePython)
  Dunit = g/cm3
  Dvalue = 1
  Group = -> [H_element101,C_element111,N_element043,O_element095]
  conduct = 2
  density = 1
  expand = 3
  formula = G4_TISSUE_SOFT_ICRU-4
  name = G4_TISSUE_SOFT_ICRU-4
  specific = 4
FEATURE [App::DocumentObjectGroupPython] H_element102  label="H_element : 0.149"  # scripted group (container) (typed FeaturePython)
  n = 0.101869
FEATURE [App::DocumentObjectGroupPython] C_element112  label="C_element : 0.456"  # scripted group (container) (typed FeaturePython)
  n = 0.456179
FEATURE [App::DocumentObjectGroupPython] N_element044  label="N_element : 0.761"  # scripted group (container) (typed FeaturePython)
  n = 0.035172
FEATURE [App::DocumentObjectGroupPython] O_element096  label="O_element : 0.407"  # scripted group (container) (typed FeaturePython)
  n = 0.40678
FEATURE [App::DocumentObjectGroupPython] G4_TISSUE_METHANE  label="G4_TISSUE-METHANE"  # scripted group (container) (typed FeaturePython)
  Dunit = g/cm3
  Dvalue = 0.00106409
  Group = -> [H_element102,C_element112,N_element044,O_element096]
  conduct = 2
  density = 1
  expand = 3
  formula = G4_TISSUE-METHANE
  name = G4_TISSUE-METHANE
  specific = 4
FEATURE [App::DocumentObjectGroupPython] H_element103  label="H_element : 0.103"  # scripted group (container) (typed FeaturePython)
  n = 0.102672
FEATURE [App::DocumentObjectGroupPython] C_element113  label="C_element : 0.569"  # scripted group (container) (typed FeaturePython)
  n = 0.56894
FEATURE [App::DocumentObjectGroupPython] N_element045  label="N_element : 0.762"  # scripted group (container) (typed FeaturePython)
  n = 0.035022
FEATURE [App::DocumentObjectGroupPython] O_element097  label="O_element : 0.293"  # scripted group (container) (typed FeaturePython)
  n = 0.293366
FEATURE [App::DocumentObjectGroupPython] G4_TISSUE_PROPANE  label="G4_TISSUE-PROPANE"  # scripted group (container) (typed FeaturePython)
  Dunit = g/cm3
  Dvalue = 0.00182628
  Group = -> [H_element103,C_element113,N_element045,O_element097]
  conduct = 2
  density = 1
  expand = 3
  formula = G4_TISSUE-PROPANE
  name = G4_TISSUE-PROPANE
  specific = 4
FEATURE [App::DocumentObjectGroupPython] Ti_element003  label="Ti_element : 1"  # scripted group (container) (typed FeaturePython)
  n = 1
  ref = Ti_element
FEATURE [App::DocumentObjectGroupPython] O_element098  label="O_element : 052"  # scripted group (container) (typed FeaturePython)
  n = 2
  ref = O_element
FEATURE [App::DocumentObjectGroupPython] G4_TITANIUM_DIOXIDE  # scripted group (container) (typed FeaturePython)
  Dunit = g/cm3
  Dvalue = 4.26
  Group = -> [Ti_element003,O_element098]
  conduct = 2
  density = 1
  expand = 3
  formula = G4_TITANIUM_DIOXIDE
  name = G4_TITANIUM_DIOXIDE
  specific = 4
FEATURE [App::DocumentObjectGroupPython] C_element114  label="C_element : 061"  # scripted group (container) (typed FeaturePython)
  n = 7
  ref = C_element
FEATURE [App::DocumentObjectGroupPython] H_element104  label="H_element : 055"  # scripted group (container) (typed FeaturePython)
  n = 8
  ref = H_element
FEATURE [App::DocumentObjectGroupPython] G4_TOLUENE  # scripted group (container) (typed FeaturePython)
  Dunit = g/cm3
  Dvalue = 0.8669
  Group = -> [C_element114,H_element104]
  conduct = 2
  density = 1
  expand = 3
  formula = G4_TOLUENE
  name = G4_TOLUENE
  specific = 4
FEATURE [App::DocumentObjectGroupPython] C_element115  label="C_element : 062"  # scripted group (container) (typed FeaturePython)
  n = 2
  ref = C_element
FEATURE [App::DocumentObjectGroupPython] H_element105  label="H_element : 056"  # scripted group (container) (typed FeaturePython)
  n = 1
  ref = H_element
FEATURE [App::DocumentObjectGroupPython] Cl_element028  label="Cl_element : 014"  # scripted group (container) (typed FeaturePython)
  n = 3
  ref = Cl_element
FEATURE [App::DocumentObjectGroupPython] G4_TRICHLOROETHYLENE  # scripted group (container) (typed FeaturePython)
  Dunit = g/cm3
  Dvalue = 1.46
  Group = -> [C_element115,H_element105,Cl_element028]
  conduct = 2
  density = 1
  expand = 3
  formula = G4_TRICHLOROETHYLENE
  name = G4_TRICHLOROETHYLENE
  specific = 4
FEATURE [App::DocumentObjectGroupPython] C_element116  label="C_element : 063"  # scripted group (container) (typed FeaturePython)
  n = 6
  ref = C_element
FEATURE [App::DocumentObjectGroupPython] H_element106  label="H_element : 15"  # scripted group (container) (typed FeaturePython)
  n = 15
  ref = H_element
FEATURE [App::DocumentObjectGroupPython] O_element099  label="O_element : 053"  # scripted group (container) (typed FeaturePython)
  n = 4
  ref = O_element
FEATURE [App::DocumentObjectGroupPython] P_element012  label="P_element : 1"  # scripted group (container) (typed FeaturePython)
  n = 1
  ref = P_element
FEATURE [App::DocumentObjectGroupPython] G4_TRIETHYL_PHOSPHATE  # scripted group (container) (typed FeaturePython)
  Dunit = g/cm3
  Dvalue = 1.07
  Group = -> [C_element116,H_element106,O_element099,P_element012]
  conduct = 2
  density = 1
  expand = 3
  formula = G4_TRIETHYL_PHOSPHATE
  name = G4_TRIETHYL_PHOSPHATE
  specific = 4
FEATURE [App::DocumentObjectGroupPython] W_element003  label="W_element : 003"  # scripted group (container) (typed FeaturePython)
  n = 1
  ref = W_element
FEATURE [App::DocumentObjectGroupPython] F_element017  label="F_element : 6"  # scripted group (container) (typed FeaturePython)
  n = 6
  ref = F_element
FEATURE [App::DocumentObjectGroupPython] G4_TUNGSTEN_HEXAFLUORIDE  # scripted group (container) (typed FeaturePython)
  Dunit = g/cm3
  Dvalue = 2.4
  Group = -> [W_element003,F_element017]
  conduct = 2
  density = 1
  expand = 3
  formula = G4_TUNGSTEN_HEXAFLUORIDE
  name = G4_TUNGSTEN_HEXAFLUORIDE
  specific = 4
FEATURE [App::DocumentObjectGroupPython] U_element001  label="U_element : 1"  # scripted group (container) (typed FeaturePython)
  n = 1
  ref = U_element
FEATURE [App::DocumentObjectGroupPython] C_element117  label="C_element : 064"  # scripted group (container) (typed FeaturePython)
  n = 2
  ref = C_element
FEATURE [App::DocumentObjectGroupPython] G4_URANIUM_DICARBIDE  # scripted group (container) (typed FeaturePython)
  Dunit = g/cm3
  Dvalue = 11.28
  Group = -> [U_element001,C_element117]
  conduct = 2
  density = 1
  expand = 3
  formula = G4_URANIUM_DICARBIDE
  name = G4_URANIUM_DICARBIDE
  specific = 4
FEATURE [App::DocumentObjectGroupPython] U_element002  label="U_element : 002"  # scripted group (container) (typed FeaturePython)
  n = 1
  ref = U_element
FEATURE [App::DocumentObjectGroupPython] C_element118  label="C_element : 065"  # scripted group (container) (typed FeaturePython)
  n = 1
  ref = C_element
FEATURE [App::DocumentObjectGroupPython] G4_URANIUM_MONOCARBIDE  # scripted group (container) (typed FeaturePython)
  Dunit = g/cm3
  Dvalue = 13.63
  Group = -> [U_element002,C_element118]
  conduct = 2
  density = 1
  expand = 3
  formula = G4_URANIUM_MONOCARBIDE
  name = G4_URANIUM_MONOCARBIDE
  specific = 4
FEATURE [App::DocumentObjectGroupPython] U_element003  label="U_element : 003"  # scripted group (container) (typed FeaturePython)
  n = 1
  ref = U_element
FEATURE [App::DocumentObjectGroupPython] O_element100  label="O_element : 054"  # scripted group (container) (typed FeaturePython)
  n = 2
  ref = O_element
FEATURE [App::DocumentObjectGroupPython] G4_URANIUM_OXIDE  # scripted group (container) (typed FeaturePython)
  Dunit = g/cm3
  Dvalue = 10.96
  Group = -> [U_element003,O_element100]
  conduct = 2
  density = 1
  expand = 3
  formula = G4_URANIUM_OXIDE
  name = G4_URANIUM_OXIDE
  specific = 4
FEATURE [App::DocumentObjectGroupPython] C_element119  label="C_element : 066"  # scripted group (container) (typed FeaturePython)
  n = 1
  ref = C_element
FEATURE [App::DocumentObjectGroupPython] H_element107  label="H_element : 057"  # scripted group (container) (typed FeaturePython)
  n = 4
  ref = H_element
FEATURE [App::DocumentObjectGroupPython] N_element046  label="N_element : 019"  # scripted group (container) (typed FeaturePython)
  n = 2
  ref = N_element
FEATURE [App::DocumentObjectGroupPython] O_element101  label="O_element : 055"  # scripted group (container) (typed FeaturePython)
  n = 1
  ref = O_element
FEATURE [App::DocumentObjectGroupPython] G4_UREA  # scripted group (container) (typed FeaturePython)
  Dunit = g/cm3
  Dvalue = 1.323
  Group = -> [C_element119,H_element107,N_element046,O_element101]
  conduct = 2
  density = 1
  expand = 3
  formula = G4_UREA
  name = G4_UREA
  specific = 4
FEATURE [App::DocumentObjectGroupPython] C_element120  label="C_element : 067"  # scripted group (container) (typed FeaturePython)
  n = 5
  ref = C_element
FEATURE [App::DocumentObjectGroupPython] H_element108  label="H_element : 058"  # scripted group (container) (typed FeaturePython)
  n = 11
  ref = H_element
FEATURE [App::DocumentObjectGroupPython] N_element047  label="N_element : 020"  # scripted group (container) (typed FeaturePython)
  n = 1
  ref = N_element
FEATURE [App::DocumentObjectGroupPython] O_element102  label="O_element : 056"  # scripted group (container) (typed FeaturePython)
  n = 2
  ref = O_element
FEATURE [App::DocumentObjectGroupPython] G4_VALINE  # scripted group (container) (typed FeaturePython)
  Dunit = g/cm3
  Dvalue = 1.23
  Group = -> [C_element120,H_element108,N_element047,O_element102]
  conduct = 2
  density = 1
  expand = 3
  formula = G4_VALINE
  name = G4_VALINE
  specific = 4
FEATURE [App::DocumentObjectGroupPython] H_element109  label="H_element : 0.009"  # scripted group (container) (typed FeaturePython)
  n = 0.009417
FEATURE [App::DocumentObjectGroupPython] C_element121  label="C_element : 0.281"  # scripted group (container) (typed FeaturePython)
  n = 0.280555
FEATURE [App::DocumentObjectGroupPython] F_element018  label="F_element : 0.710"  # scripted group (container) (typed FeaturePython)
  n = 0.710028
FEATURE [App::DocumentObjectGroupPython] G4_VITON  # scripted group (container) (typed FeaturePython)
  Dunit = g/cm3
  Dvalue = 1.8
  Group = -> [H_element109,C_element121,F_element018]
  conduct = 2
  density = 1
  expand = 3
  formula = G4_VITON
  name = G4_VITON
  specific = 4
FEATURE [App::DocumentObjectGroupPython] H_element110  label="H_element : 059"  # scripted group (container) (typed FeaturePython)
  n = 2
  ref = H_element
FEATURE [App::DocumentObjectGroupPython] O_element103  label="O_element : 057"  # scripted group (container) (typed FeaturePython)
  n = 1
  ref = O_element
FEATURE [App::DocumentObjectGroupPython] G4_WATER  # scripted group (container) (typed FeaturePython)
  Dunit = g/cm3
  Dvalue = 1
  Group = -> [H_element110,O_element103]
  conduct = 2
  density = 1
  expand = 3
  formula = G4_WATER
  name = G4_WATER
  specific = 4
FEATURE [App::DocumentObjectGroupPython] H_element111  label="H_element : 060"  # scripted group (container) (typed FeaturePython)
  n = 2
  ref = H_element
FEATURE [App::DocumentObjectGroupPython] O_element104  label="O_element : 058"  # scripted group (container) (typed FeaturePython)
  n = 1
  ref = O_element
FEATURE [App::DocumentObjectGroupPython] G4_WATER_VAPOR  # scripted group (container) (typed FeaturePython)
  Dunit = g/cm3
  Dvalue = 0.000756182
  Group = -> [H_element111,O_element104]
  conduct = 2
  density = 1
  expand = 3
  formula = G4_WATER_VAPOR
  name = G4_WATER_VAPOR
  specific = 4
FEATURE [App::DocumentObjectGroupPython] C_element122  label="C_element : 068"  # scripted group (container) (typed FeaturePython)
  n = 8
  ref = C_element
FEATURE [App::DocumentObjectGroupPython] H_element112  label="H_element : 061"  # scripted group (container) (typed FeaturePython)
  n = 10
  ref = H_element
FEATURE [App::DocumentObjectGroupPython] G4_XYLENE  # scripted group (container) (typed FeaturePython)
  Dunit = g/cm3
  Dvalue = 0.87
  Group = -> [C_element122,H_element112]
  conduct = 2
  density = 1
  expand = 3
  formula = G4_XYLENE
  name = G4_XYLENE
  specific = 4
FEATURE [App::DocumentObjectGroupPython] C_element123  label="C_element : 069"  # scripted group (container) (typed FeaturePython)
  n = 1
  ref = C_element
FEATURE [App::DocumentObjectGroupPython] G4_GRAPHITE  # scripted group (container) (typed FeaturePython)
  Dunit = g/cm3
  Dvalue = 2.21
  Group = -> [C_element123]
  conduct = 2
  density = 1
  expand = 3
  formula = G4_GRAPHITE
  name = G4_GRAPHITE
  specific = 4
FEATURE [App::DocumentObjectGroupPython] NIST  # scripted group (container) (typed FeaturePython)
  Group = -> [G4_A_150_TISSUE,G4_ACETONE,G4_ACETYLENE,G4_ADENINE,G4_ADIPOSE_TISSUE_ICRP,G4_AIR,G4_ALANINE,G4_ALUMINUM_OXIDE,G4_AMBER,G4_AMMONIA,G4_ANILINE,G4_ANTHRACENE,G4_B_100_BONE,G4_BAKELITE,G4_BARIUM_FLUORIDE,G4_BARIUM_SULFATE,G4_BENZENE,G4_BERYLLIUM_OXIDE,G4_BGO,G4_BLOOD_ICRP,G4_BONE_COMPACT_ICRU,G4_BONE_CORTICAL_ICRP,G4_BORON_CARBIDE,G4_BORON_OXIDE,G4_BRAIN_ICRP,G4_BUTANE,G4_N_BUTYL_ALCOHOL,G4_C_552,+152 more]
FEATURE [App::DocumentObjectGroupPython] H_element113  label="H_element : 062"  # scripted group (container) (typed FeaturePython)
  n = 1
  ref = H_element
FEATURE [App::DocumentObjectGroupPython] G4_H  # scripted group (container) (typed FeaturePython)
  Dunit = g/cm3
  Dvalue = 8.3748e-05
  Group = -> [H_element113]
  conduct = 2
  density = 1
  expand = 3
  formula = H
  name = G4_H
  specific = 4
FEATURE [App::DocumentObjectGroupPython] He_element001  label="He_element : 1"  # scripted group (container) (typed FeaturePython)
  n = 1
  ref = He_element
FEATURE [App::DocumentObjectGroupPython] G4_He  # scripted group (container) (typed FeaturePython)
  Dunit = g/cm3
  Dvalue = 0.000166322
  Group = -> [He_element001]
  conduct = 2
  density = 1
  expand = 3
  formula = He
  name = G4_He
  specific = 4
FEATURE [App::DocumentObjectGroupPython] Li_element008  label="Li_element : 008"  # scripted group (container) (typed FeaturePython)
  n = 1
  ref = Li_element
FEATURE [App::DocumentObjectGroupPython] G4_Li  # scripted group (container) (typed FeaturePython)
  Dunit = g/cm3
  Dvalue = 0.534
  Group = -> [Li_element008]
  conduct = 2
  density = 1
  expand = 3
  formula = Li
  name = G4_Li
  specific = 4
FEATURE [App::DocumentObjectGroupPython] Be_element002  label="Be_element : 002"  # scripted group (container) (typed FeaturePython)
  n = 1
  ref = Be_element
FEATURE [App::DocumentObjectGroupPython] G4_Be  # scripted group (container) (typed FeaturePython)
  Dunit = g/cm3
  Dvalue = 1.848
  Group = -> [Be_element002]
  conduct = 2
  density = 1
  expand = 3
  formula = Be
  name = G4_Be
  specific = 4
FEATURE [App::DocumentObjectGroupPython] B_element007  label="B_element : 007"  # scripted group (container) (typed FeaturePython)
  n = 1
  ref = B_element
FEATURE [App::DocumentObjectGroupPython] G4_B  # scripted group (container) (typed FeaturePython)
  Dunit = g/cm3
  Dvalue = 2.37
  Group = -> [B_element007]
  conduct = 2
  density = 1
  expand = 3
  formula = B
  name = G4_B
  specific = 4
FEATURE [App::DocumentObjectGroupPython] C_element124  label="C_element : 070"  # scripted group (container) (typed FeaturePython)
  n = 1
  ref = C_element
FEATURE [App::DocumentObjectGroupPython] G4_C  # scripted group (container) (typed FeaturePython)
  Dunit = g/cm3
  Dvalue = 2
  Group = -> [C_element124]
  conduct = 2
  density = 1
  expand = 3
  formula = C
  name = G4_C
  specific = 4
FEATURE [App::DocumentObjectGroupPython] N_element048  label="N_element : 021"  # scripted group (container) (typed FeaturePython)
  n = 1
  ref = N_element
FEATURE [App::DocumentObjectGroupPython] G4_N  # scripted group (container) (typed FeaturePython)
  Dunit = g/cm3
  Dvalue = 0.0011652
  Group = -> [N_element048]
  conduct = 2
  density = 1
  expand = 3
  formula = N
  name = G4_N
  specific = 4
FEATURE [App::DocumentObjectGroupPython] O_element105  label="O_element : 059"  # scripted group (container) (typed FeaturePython)
  n = 1
  ref = O_element
FEATURE [App::DocumentObjectGroupPython] G4_O  # scripted group (container) (typed FeaturePython)
  Dunit = g/cm3
  Dvalue = 0.00133151
  Group = -> [O_element105]
  conduct = 2
  density = 1
  expand = 3
  formula = O
  name = G4_O
  specific = 4
FEATURE [App::DocumentObjectGroupPython] F_element019  label="F_element : 008"  # scripted group (container) (typed FeaturePython)
  n = 1
  ref = F_element
FEATURE [App::DocumentObjectGroupPython] G4_F  # scripted group (container) (typed FeaturePython)
  Dunit = g/cm3
  Dvalue = 0.00158029
  Group = -> [F_element019]
  conduct = 2
  density = 1
  expand = 3
  formula = F
  name = G4_F
  specific = 4
FEATURE [App::DocumentObjectGroupPython] Ne_element001  label="Ne_element : 1"  # scripted group (container) (typed FeaturePython)
  n = 1
  ref = Ne_element
FEATURE [App::DocumentObjectGroupPython] G4_Ne  # scripted group (container) (typed FeaturePython)
  Dunit = g/cm3
  Dvalue = 0.000838505
  Group = -> [Ne_element001]
  conduct = 2
  density = 1
  expand = 3
  formula = Ne
  name = G4_Ne
  specific = 4
FEATURE [App::DocumentObjectGroupPython] Na_element020  label="Na_element : 005"  # scripted group (container) (typed FeaturePython)
  n = 1
  ref = Na_element
FEATURE [App::DocumentObjectGroupPython] G4_Na  # scripted group (container) (typed FeaturePython)
  Dunit = g/cm3
  Dvalue = 0.971
  Group = -> [Na_element020]
  conduct = 2
  density = 1
  expand = 3
  formula = Na
  name = G4_Na
  specific = 4
FEATURE [App::DocumentObjectGroupPython] Mg_element011  label="Mg_element : 005"  # scripted group (container) (typed FeaturePython)
  n = 1
  ref = Mg_element
FEATURE [App::DocumentObjectGroupPython] G4_Mg  # scripted group (container) (typed FeaturePython)
  Dunit = g/cm3
  Dvalue = 1.74
  Group = -> [Mg_element011]
  conduct = 2
  density = 1
  expand = 3
  formula = Mg
  name = G4_Mg
  specific = 4
FEATURE [App::DocumentObjectGroupPython] Al_element004  label="Al_element : 1"  # scripted group (container) (typed FeaturePython)
  n = 1
  ref = Al_element
FEATURE [App::DocumentObjectGroupPython] G4_Al  # scripted group (container) (typed FeaturePython)
  Dunit = g/cm3
  Dvalue = 2.699
  Group = -> [Al_element004]
  conduct = 2
  density = 1
  expand = 3
  formula = Al
  name = G4_Al
  specific = 4
FEATURE [App::DocumentObjectGroupPython] Si_element007  label="Si_element : 002"  # scripted group (container) (typed FeaturePython)
  n = 1
  ref = Si_element
FEATURE [App::DocumentObjectGroupPython] G4_Si  # scripted group (container) (typed FeaturePython)
  Dunit = g/cm3
  Dvalue = 2.33
  Group = -> [Si_element007]
  conduct = 2
  density = 1
  expand = 3
  formula = Si
  name = G4_Si
  specific = 4
FEATURE [App::DocumentObjectGroupPython] P_element013  label="P_element : 002"  # scripted group (container) (typed FeaturePython)
  n = 1
  ref = P_element
FEATURE [App::DocumentObjectGroupPython] G4_P  # scripted group (container) (typed FeaturePython)
  Dunit = g/cm3
  Dvalue = 2.2
  Group = -> [P_element013]
  conduct = 2
  density = 1
  expand = 3
  formula = P
  name = G4_P
  specific = 4
FEATURE [App::DocumentObjectGroupPython] S_element023  label="S_element : 007"  # scripted group (container) (typed FeaturePython)
  n = 1
  ref = S_element
FEATURE [App::DocumentObjectGroupPython] G4_S  # scripted group (container) (typed FeaturePython)
  Dunit = g/cm3
  Dvalue = 2
  Group = -> [S_element023]
  conduct = 2
  density = 1
  expand = 3
  formula = S
  name = G4_S
  specific = 4
FEATURE [App::DocumentObjectGroupPython] Cl_element029  label="Cl_element : 015"  # scripted group (container) (typed FeaturePython)
  n = 1
  ref = Cl_element
FEATURE [App::DocumentObjectGroupPython] G4_Cl  # scripted group (container) (typed FeaturePython)
  Dunit = g/cm3
  Dvalue = 0.00299473
  Group = -> [Cl_element029]
  conduct = 2
  density = 1
  expand = 3
  formula = Cl
  name = G4_Cl
  specific = 4
FEATURE [App::DocumentObjectGroupPython] Ar_element002  label="Ar_element : 1"  # scripted group (container) (typed FeaturePython)
  n = 1
  ref = Ar_element
FEATURE [App::DocumentObjectGroupPython] G4_Ar  # scripted group (container) (typed FeaturePython)
  Dunit = g/cm3
  Dvalue = 0.00166201
  Group = -> [Ar_element002]
  conduct = 2
  density = 1
  expand = 3
  formula = Ar
  name = G4_Ar
  specific = 4
FEATURE [App::DocumentObjectGroupPython] K_element013  label="K_element : 003"  # scripted group (container) (typed FeaturePython)
  n = 1
  ref = K_element
FEATURE [App::DocumentObjectGroupPython] G4_K  # scripted group (container) (typed FeaturePython)
  Dunit = g/cm3
  Dvalue = 0.862
  Group = -> [K_element013]
  conduct = 2
  density = 1
  expand = 3
  formula = K
  name = G4_K
  specific = 4
FEATURE [App::DocumentObjectGroupPython] Ca_element014  label="Ca_element : 007"  # scripted group (container) (typed FeaturePython)
  n = 1
  ref = Ca_element
FEATURE [App::DocumentObjectGroupPython] G4_Ca  # scripted group (container) (typed FeaturePython)
  Dunit = g/cm3
  Dvalue = 1.55
  Group = -> [Ca_element014]
  conduct = 2
  density = 1
  expand = 3
  formula = Ca
  name = G4_Ca
  specific = 4
FEATURE [App::DocumentObjectGroupPython] Sc_element001  label="Sc_element : 1"  # scripted group (container) (typed FeaturePython)
  n = 1
  ref = Sc_element
FEATURE [App::DocumentObjectGroupPython] G4_Sc  # scripted group (container) (typed FeaturePython)
  Dunit = g/cm3
  Dvalue = 2.989
  Group = -> [Sc_element001]
  conduct = 2
  density = 1
  expand = 3
  formula = Sc
  name = G4_Sc
  specific = 4
FEATURE [App::DocumentObjectGroupPython] Ti_element004  label="Ti_element : 002"  # scripted group (container) (typed FeaturePython)
  n = 1
  ref = Ti_element
FEATURE [App::DocumentObjectGroupPython] G4_Ti  # scripted group (container) (typed FeaturePython)
  Dunit = g/cm3
  Dvalue = 4.54
  Group = -> [Ti_element004]
  conduct = 2
  density = 1
  expand = 3
  formula = Ti
  name = G4_Ti
  specific = 4
FEATURE [App::DocumentObjectGroupPython] V_element001  label="V_element : 1"  # scripted group (container) (typed FeaturePython)
  n = 1
  ref = V_element
FEATURE [App::DocumentObjectGroupPython] G4_V  # scripted group (container) (typed FeaturePython)
  Dunit = g/cm3
  Dvalue = 6.11
  Group = -> [V_element001]
  conduct = 2
  density = 1
  expand = 3
  formula = V
  name = G4_V
  specific = 4
FEATURE [App::DocumentObjectGroupPython] Cr_element001  label="Cr_element : 1"  # scripted group (container) (typed FeaturePython)
  n = 1
  ref = Cr_element
FEATURE [App::DocumentObjectGroupPython] G4_Cr  # scripted group (container) (typed FeaturePython)
  Dunit = g/cm3
  Dvalue = 7.18
  Group = -> [Cr_element001]
  conduct = 2
  density = 1
  expand = 3
  formula = Cr
  name = G4_Cr
  specific = 4
FEATURE [App::DocumentObjectGroupPython] Mn_element001  label="Mn_element : 1"  # scripted group (container) (typed FeaturePython)
  n = 1
  ref = Mn_element
FEATURE [App::DocumentObjectGroupPython] G4_Mn  # scripted group (container) (typed FeaturePython)
  Dunit = g/cm3
  Dvalue = 7.44
  Group = -> [Mn_element001]
  conduct = 2
  density = 1
  expand = 3
  formula = Mn
  name = G4_Mn
  specific = 4
FEATURE [App::DocumentObjectGroupPython] Fe_element007  label="Fe_element : 004"  # scripted group (container) (typed FeaturePython)
  n = 1
  ref = Fe_element
FEATURE [App::DocumentObjectGroupPython] G4_Fe  # scripted group (container) (typed FeaturePython)
  Dunit = g/cm3
  Dvalue = 7.874
  Group = -> [Fe_element007]
  conduct = 2
  density = 1
  expand = 3
  formula = Fe
  name = G4_Fe
  specific = 4
FEATURE [App::DocumentObjectGroupPython] Co_element001  label="Co_element : 1"  # scripted group (container) (typed FeaturePython)
  n = 1
  ref = Co_element
FEATURE [App::DocumentObjectGroupPython] G4_Co  # scripted group (container) (typed FeaturePython)
  Dunit = g/cm3
  Dvalue = 8.9
  Group = -> [Co_element001]
  conduct = 2
  density = 1
  expand = 3
  formula = Co
  name = G4_Co
  specific = 4
FEATURE [App::DocumentObjectGroupPython] Ni_element001  label="Ni_element : 1"  # scripted group (container) (typed FeaturePython)
  n = 1
  ref = Ni_element
FEATURE [App::DocumentObjectGroupPython] G4_Ni  # scripted group (container) (typed FeaturePython)
  Dunit = g/cm3
  Dvalue = 8.902
  Group = -> [Ni_element001]
  conduct = 2
  density = 1
  expand = 3
  formula = Ni
  name = G4_Ni
  specific = 4
FEATURE [App::DocumentObjectGroupPython] Cu_element001  label="Cu_element : 1"  # scripted group (container) (typed FeaturePython)
  n = 1
  ref = Cu_element
FEATURE [App::DocumentObjectGroupPython] G4_Cu  # scripted group (container) (typed FeaturePython)
  Dunit = g/cm3
  Dvalue = 8.96
  Group = -> [Cu_element001]
  conduct = 2
  density = 1
  expand = 3
  formula = Cu
  name = G4_Cu
  specific = 4
FEATURE [App::DocumentObjectGroupPython] Zn_element001  label="Zn_element : 1"  # scripted group (container) (typed FeaturePython)
  n = 1
  ref = Zn_element
FEATURE [App::DocumentObjectGroupPython] G4_Zn  # scripted group (container) (typed FeaturePython)
  Dunit = g/cm3
  Dvalue = 7.133
  Group = -> [Zn_element001]
  conduct = 2
  density = 1
  expand = 3
  formula = Zn
  name = G4_Zn
  specific = 4
FEATURE [App::DocumentObjectGroupPython] Ga_element002  label="Ga_element : 002"  # scripted group (container) (typed FeaturePython)
  n = 1
  ref = Ga_element
FEATURE [App::DocumentObjectGroupPython] G4_Ga  # scripted group (container) (typed FeaturePython)
  Dunit = g/cm3
  Dvalue = 5.904
  Group = -> [Ga_element002]
  conduct = 2
  density = 1
  expand = 3
  formula = Ga
  name = G4_Ga
  specific = 4
FEATURE [App::DocumentObjectGroupPython] Ge_element002  label="Ge_element : 1"  # scripted group (container) (typed FeaturePython)
  n = 1
  ref = Ge_element
FEATURE [App::DocumentObjectGroupPython] G4_Ge  # scripted group (container) (typed FeaturePython)
  Dunit = g/cm3
  Dvalue = 5.323
  Group = -> [Ge_element002]
  conduct = 2
  density = 1
  expand = 3
  formula = Ge
  name = G4_Ge
  specific = 4
FEATURE [App::DocumentObjectGroupPython] As_element003  label="As_element : 002"  # scripted group (container) (typed FeaturePython)
  n = 1
  ref = As_element
FEATURE [App::DocumentObjectGroupPython] G4_As  # scripted group (container) (typed FeaturePython)
  Dunit = g/cm3
  Dvalue = 5.73
  Group = -> [As_element003]
  conduct = 2
  density = 1
  expand = 3
  formula = As
  name = G4_As
  specific = 4
FEATURE [App::DocumentObjectGroupPython] Se_element001  label="Se_element : 1"  # scripted group (container) (typed FeaturePython)
  n = 1
  ref = Se_element
FEATURE [App::DocumentObjectGroupPython] G4_Se  # scripted group (container) (typed FeaturePython)
  Dunit = g/cm3
  Dvalue = 4.5
  Group = -> [Se_element001]
  conduct = 2
  density = 1
  expand = 3
  formula = Se
  name = G4_Se
  specific = 4
FEATURE [App::DocumentObjectGroupPython] Br_element007  label="Br_element : 004"  # scripted group (container) (typed FeaturePython)
  n = 1
  ref = Br_element
FEATURE [App::DocumentObjectGroupPython] G4_Br  # scripted group (container) (typed FeaturePython)
  Dunit = g/cm3
  Dvalue = 0.0070721
  Group = -> [Br_element007]
  conduct = 2
  density = 1
  expand = 3
  formula = Br
  name = G4_Br
  specific = 4
FEATURE [App::DocumentObjectGroupPython] Kr_element001  label="Kr_element : 1"  # scripted group (container) (typed FeaturePython)
  n = 1
  ref = Kr_element
FEATURE [App::DocumentObjectGroupPython] G4_Kr  # scripted group (container) (typed FeaturePython)
  Dunit = g/cm3
  Dvalue = 0.00347832
  Group = -> [Kr_element001]
  conduct = 2
  density = 1
  expand = 3
  formula = Kr
  name = G4_Kr
  specific = 4
FEATURE [App::DocumentObjectGroupPython] Rb_element001  label="Rb_element : 1"  # scripted group (container) (typed FeaturePython)
  n = 1
  ref = Rb_element
FEATURE [App::DocumentObjectGroupPython] G4_Rb  # scripted group (container) (typed FeaturePython)
  Dunit = g/cm3
  Dvalue = 1.532
  Group = -> [Rb_element001]
  conduct = 2
  density = 1
  expand = 3
  formula = Rb
  name = G4_Rb
  specific = 4
FEATURE [App::DocumentObjectGroupPython] Sr_element001  label="Sr_element : 1"  # scripted group (container) (typed FeaturePython)
  n = 1
  ref = Sr_element
FEATURE [App::DocumentObjectGroupPython] G4_Sr  # scripted group (container) (typed FeaturePython)
  Dunit = g/cm3
  Dvalue = 2.54
  Group = -> [Sr_element001]
  conduct = 2
  density = 1
  expand = 3
  formula = Sr
  name = G4_Sr
  specific = 4
FEATURE [App::DocumentObjectGroupPython] Y_element001  label="Y_element : 1"  # scripted group (container) (typed FeaturePython)
  n = 1
  ref = Y_element
FEATURE [App::DocumentObjectGroupPython] G4_Y  # scripted group (container) (typed FeaturePython)
  Dunit = g/cm3
  Dvalue = 4.469
  Group = -> [Y_element001]
  conduct = 2
  density = 1
  expand = 3
  formula = Y
  name = G4_Y
  specific = 4
FEATURE [App::DocumentObjectGroupPython] Zr_element001  label="Zr_element : 1"  # scripted group (container) (typed FeaturePython)
  n = 1
  ref = Zr_element
FEATURE [App::DocumentObjectGroupPython] G4_Zr  # scripted group (container) (typed FeaturePython)
  Dunit = g/cm3
  Dvalue = 6.506
  Group = -> [Zr_element001]
  conduct = 2
  density = 1
  expand = 3
  formula = Zr
  name = G4_Zr
  specific = 4
FEATURE [App::DocumentObjectGroupPython] Nb_element001  label="Nb_element : 1"  # scripted group (container) (typed FeaturePython)
  n = 1
  ref = Nb_element
FEATURE [App::DocumentObjectGroupPython] G4_Nb  # scripted group (container) (typed FeaturePython)
  Dunit = g/cm3
  Dvalue = 8.57
  Group = -> [Nb_element001]
  conduct = 2
  density = 1
  expand = 3
  formula = Nb
  name = G4_Nb
  specific = 4
FEATURE [App::DocumentObjectGroupPython] Mo_element001  label="Mo_element : 1"  # scripted group (container) (typed FeaturePython)
  n = 1
  ref = Mo_element
FEATURE [App::DocumentObjectGroupPython] G4_Mo  # scripted group (container) (typed FeaturePython)
  Dunit = g/cm3
  Dvalue = 10.22
  Group = -> [Mo_element001]
  conduct = 2
  density = 1
  expand = 3
  formula = Mo
  name = G4_Mo
  specific = 4
FEATURE [App::DocumentObjectGroupPython] Tc_element001  label="Tc_element : 1"  # scripted group (container) (typed FeaturePython)
  n = 1
  ref = Tc_element
FEATURE [App::DocumentObjectGroupPython] G4_Tc  # scripted group (container) (typed FeaturePython)
  Dunit = g/cm3
  Dvalue = 11.5
  Group = -> [Tc_element001]
  conduct = 2
  density = 1
  expand = 3
  formula = Tc
  name = G4_Tc
  specific = 4
FEATURE [App::DocumentObjectGroupPython] Ru_element001  label="Ru_element : 1"  # scripted group (container) (typed FeaturePython)
  n = 1
  ref = Ru_element
FEATURE [App::DocumentObjectGroupPython] G4_Ru  # scripted group (container) (typed FeaturePython)
  Dunit = g/cm3
  Dvalue = 12.41
  Group = -> [Ru_element001]
  conduct = 2
  density = 1
  expand = 3
  formula = Ru
  name = G4_Ru
  specific = 4
FEATURE [App::DocumentObjectGroupPython] Rh_element001  label="Rh_element : 1"  # scripted group (container) (typed FeaturePython)
  n = 1
  ref = Rh_element
FEATURE [App::DocumentObjectGroupPython] G4_Rh  # scripted group (container) (typed FeaturePython)
  Dunit = g/cm3
  Dvalue = 12.41
  Group = -> [Rh_element001]
  conduct = 2
  density = 1
  expand = 3
  formula = Rh
  name = G4_Rh
  specific = 4
FEATURE [App::DocumentObjectGroupPython] Pd_element001  label="Pd_element : 1"  # scripted group (container) (typed FeaturePython)
  n = 1
  ref = Pd_element
FEATURE [App::DocumentObjectGroupPython] G4_Pd  # scripted group (container) (typed FeaturePython)
  Dunit = g/cm3
  Dvalue = 12.02
  Group = -> [Pd_element001]
  conduct = 2
  density = 1
  expand = 3
  formula = Pd
  name = G4_Pd
  specific = 4
FEATURE [App::DocumentObjectGroupPython] Ag_element006  label="Ag_element : 004"  # scripted group (container) (typed FeaturePython)
  n = 1
  ref = Ag_element
FEATURE [App::DocumentObjectGroupPython] G4_Ag  # scripted group (container) (typed FeaturePython)
  Dunit = g/cm3
  Dvalue = 10.5
  Group = -> [Ag_element006]
  conduct = 2
  density = 1
  expand = 3
  formula = Ag
  name = G4_Ag
  specific = 4
FEATURE [App::DocumentObjectGroupPython] Cd_element003  label="Cd_element : 003"  # scripted group (container) (typed FeaturePython)
  n = 1
  ref = Cd_element
FEATURE [App::DocumentObjectGroupPython] G4_Cd  # scripted group (container) (typed FeaturePython)
  Dunit = g/cm3
  Dvalue = 8.65
  Group = -> [Cd_element003]
  conduct = 2
  density = 1
  expand = 3
  formula = Cd
  name = G4_Cd
  specific = 4
FEATURE [App::DocumentObjectGroupPython] In_element001  label="In_element : 1"  # scripted group (container) (typed FeaturePython)
  n = 1
  ref = In_element
FEATURE [App::DocumentObjectGroupPython] G4_In  # scripted group (container) (typed FeaturePython)
  Dunit = g/cm3
  Dvalue = 7.31
  Group = -> [In_element001]
  conduct = 2
  density = 1
  expand = 3
  formula = In
  name = G4_In
  specific = 4
FEATURE [App::DocumentObjectGroupPython] Sn_element001  label="Sn_element : 1"  # scripted group (container) (typed FeaturePython)
  n = 1
  ref = Sn_element
FEATURE [App::DocumentObjectGroupPython] G4_Sn  # scripted group (container) (typed FeaturePython)
  Dunit = g/cm3
  Dvalue = 7.31
  Group = -> [Sn_element001]
  conduct = 2
  density = 1
  expand = 3
  formula = Sn
  name = G4_Sn
  specific = 4
FEATURE [App::DocumentObjectGroupPython] Sb_element001  label="Sb_element : 1"  # scripted group (container) (typed FeaturePython)
  n = 1
  ref = Sb_element
FEATURE [App::DocumentObjectGroupPython] G4_Sb  # scripted group (container) (typed FeaturePython)
  Dunit = g/cm3
  Dvalue = 6.691
  Group = -> [Sb_element001]
  conduct = 2
  density = 1
  expand = 3
  formula = Sb
  name = G4_Sb
  specific = 4
FEATURE [App::DocumentObjectGroupPython] Te_element002  label="Te_element : 002"  # scripted group (container) (typed FeaturePython)
  n = 1
  ref = Te_element
FEATURE [App::DocumentObjectGroupPython] G4_Te  # scripted group (container) (typed FeaturePython)
  Dunit = g/cm3
  Dvalue = 6.24
  Group = -> [Te_element002]
  conduct = 2
  density = 1
  expand = 3
  formula = Te
  name = G4_Te
  specific = 4
FEATURE [App::DocumentObjectGroupPython] I_element010  label="I_element : 006"  # scripted group (container) (typed FeaturePython)
  n = 1
  ref = I_element
FEATURE [App::DocumentObjectGroupPython] G4_I  # scripted group (container) (typed FeaturePython)
  Dunit = g/cm3
  Dvalue = 4.93
  Group = -> [I_element010]
  conduct = 2
  density = 1
  expand = 3
  formula = I
  name = G4_I
  specific = 4
FEATURE [App::DocumentObjectGroupPython] Xe_element001  label="Xe_element : 1"  # scripted group (container) (typed FeaturePython)
  n = 1
  ref = Xe_element
FEATURE [App::DocumentObjectGroupPython] G4_Xe  # scripted group (container) (typed FeaturePython)
  Dunit = g/cm3
  Dvalue = 0.00548536
  Group = -> [Xe_element001]
  conduct = 2
  density = 1
  expand = 3
  formula = Xe
  name = G4_Xe
  specific = 4
FEATURE [App::DocumentObjectGroupPython] Cs_element003  label="Cs_element : 003"  # scripted group (container) (typed FeaturePython)
  n = 1
  ref = Cs_element
FEATURE [App::DocumentObjectGroupPython] G4_Cs  # scripted group (container) (typed FeaturePython)
  Dunit = g/cm3
  Dvalue = 1.873
  Group = -> [Cs_element003]
  conduct = 2
  density = 1
  expand = 3
  formula = Cs
  name = G4_Cs
  specific = 4
FEATURE [App::DocumentObjectGroupPython] Ba_element003  label="Ba_element : 003"  # scripted group (container) (typed FeaturePython)
  n = 1
  ref = Ba_element
FEATURE [App::DocumentObjectGroupPython] G4_Ba  # scripted group (container) (typed FeaturePython)
  Dunit = g/cm3
  Dvalue = 3.5
  Group = -> [Ba_element003]
  conduct = 2
  density = 1
  expand = 3
  formula = Ba
  name = G4_Ba
  specific = 4
FEATURE [App::DocumentObjectGroupPython] La_element003  label="La_element : 003"  # scripted group (container) (typed FeaturePython)
  n = 1
  ref = La_element
FEATURE [App::DocumentObjectGroupPython] G4_La  # scripted group (container) (typed FeaturePython)
  Dunit = g/cm3
  Dvalue = 6.154
  Group = -> [La_element003]
  conduct = 2
  density = 1
  expand = 3
  formula = La
  name = G4_La
  specific = 4
FEATURE [App::DocumentObjectGroupPython] Ce_element002  label="Ce_element : 1"  # scripted group (container) (typed FeaturePython)
  n = 1
  ref = Ce_element
FEATURE [App::DocumentObjectGroupPython] G4_Ce  # scripted group (container) (typed FeaturePython)
  Dunit = g/cm3
  Dvalue = 6.657
  Group = -> [Ce_element002]
  conduct = 2
  density = 1
  expand = 3
  formula = Ce
  name = G4_Ce
  specific = 4
FEATURE [App::DocumentObjectGroupPython] Pr_element001  label="Pr_element : 1"  # scripted group (container) (typed FeaturePython)
  n = 1
  ref = Pr_element
FEATURE [App::DocumentObjectGroupPython] G4_Pr  # scripted group (container) (typed FeaturePython)
  Dunit = g/cm3
  Dvalue = 6.71
  Group = -> [Pr_element001]
  conduct = 2
  density = 1
  expand = 3
  formula = Pr
  name = G4_Pr
  specific = 4
FEATURE [App::DocumentObjectGroupPython] Nd_element001  label="Nd_element : 1"  # scripted group (container) (typed FeaturePython)
  n = 1
  ref = Nd_element
FEATURE [App::DocumentObjectGroupPython] G4_Nd  # scripted group (container) (typed FeaturePython)
  Dunit = g/cm3
  Dvalue = 6.9
  Group = -> [Nd_element001]
  conduct = 2
  density = 1
  expand = 3
  formula = Nd
  name = G4_Nd
  specific = 4
FEATURE [App::DocumentObjectGroupPython] Pm_element001  label="Pm_element : 1"  # scripted group (container) (typed FeaturePython)
  n = 1
  ref = Pm_element
FEATURE [App::DocumentObjectGroupPython] G4_Pm  # scripted group (container) (typed FeaturePython)
  Dunit = g/cm3
  Dvalue = 7.22
  Group = -> [Pm_element001]
  conduct = 2
  density = 1
  expand = 3
  formula = Pm
  name = G4_Pm
  specific = 4
FEATURE [App::DocumentObjectGroupPython] Sm_element001  label="Sm_element : 1"  # scripted group (container) (typed FeaturePython)
  n = 1
  ref = Sm_element
FEATURE [App::DocumentObjectGroupPython] G4_Sm  # scripted group (container) (typed FeaturePython)
  Dunit = g/cm3
  Dvalue = 7.46
  Group = -> [Sm_element001]
  conduct = 2
  density = 1
  expand = 3
  formula = Sm
  name = G4_Sm
  specific = 4
FEATURE [App::DocumentObjectGroupPython] Eu_element001  label="Eu_element : 1"  # scripted group (container) (typed FeaturePython)
  n = 1
  ref = Eu_element
FEATURE [App::DocumentObjectGroupPython] G4_Eu  # scripted group (container) (typed FeaturePython)
  Dunit = g/cm3
  Dvalue = 5.243
  Group = -> [Eu_element001]
  conduct = 2
  density = 1
  expand = 3
  formula = Eu
  name = G4_Eu
  specific = 4
FEATURE [App::DocumentObjectGroupPython] Gd_element002  label="Gd_element : 1"  # scripted group (container) (typed FeaturePython)
  n = 1
  ref = Gd_element
FEATURE [App::DocumentObjectGroupPython] G4_Gd  # scripted group (container) (typed FeaturePython)
  Dunit = g/cm3
  Dvalue = 7.9004
  Group = -> [Gd_element002]
  conduct = 2
  density = 1
  expand = 3
  formula = Gd
  name = G4_Gd
  specific = 4
FEATURE [App::DocumentObjectGroupPython] Tb_element001  label="Tb_element : 1"  # scripted group (container) (typed FeaturePython)
  n = 1
  ref = Tb_element
FEATURE [App::DocumentObjectGroupPython] G4_Tb  # scripted group (container) (typed FeaturePython)
  Dunit = g/cm3
  Dvalue = 8.229
  Group = -> [Tb_element001]
  conduct = 2
  density = 1
  expand = 3
  formula = Tb
  name = G4_Tb
  specific = 4
FEATURE [App::DocumentObjectGroupPython] Dy_element001  label="Dy_element : 1"  # scripted group (container) (typed FeaturePython)
  n = 1
  ref = Dy_element
FEATURE [App::DocumentObjectGroupPython] G4_Dy  # scripted group (container) (typed FeaturePython)
  Dunit = g/cm3
  Dvalue = 8.55
  Group = -> [Dy_element001]
  conduct = 2
  density = 1
  expand = 3
  formula = Dy
  name = G4_Dy
  specific = 4
FEATURE [App::DocumentObjectGroupPython] Ho_element001  label="Ho_element : 1"  # scripted group (container) (typed FeaturePython)
  n = 1
  ref = Ho_element
FEATURE [App::DocumentObjectGroupPython] G4_Ho  # scripted group (container) (typed FeaturePython)
  Dunit = g/cm3
  Dvalue = 8.795
  Group = -> [Ho_element001]
  conduct = 2
  density = 1
  expand = 3
  formula = Ho
  name = G4_Ho
  specific = 4
FEATURE [App::DocumentObjectGroupPython] Er_element001  label="Er_element : 1"  # scripted group (container) (typed FeaturePython)
  n = 1
  ref = Er_element
FEATURE [App::DocumentObjectGroupPython] G4_Er  # scripted group (container) (typed FeaturePython)
  Dunit = g/cm3
  Dvalue = 9.066
  Group = -> [Er_element001]
  conduct = 2
  density = 1
  expand = 3
  formula = Er
  name = G4_Er
  specific = 4
FEATURE [App::DocumentObjectGroupPython] Tm_element001  label="Tm_element : 1"  # scripted group (container) (typed FeaturePython)
  n = 1
  ref = Tm_element
FEATURE [App::DocumentObjectGroupPython] G4_Tm  # scripted group (container) (typed FeaturePython)
  Dunit = g/cm3
  Dvalue = 9.321
  Group = -> [Tm_element001]
  conduct = 2
  density = 1
  expand = 3
  formula = Tm
  name = G4_Tm
  specific = 4
FEATURE [App::DocumentObjectGroupPython] Yb_element001  label="Yb_element : 1"  # scripted group (container) (typed FeaturePython)
  n = 1
  ref = Yb_element
FEATURE [App::DocumentObjectGroupPython] G4_Yb  # scripted group (container) (typed FeaturePython)
  Dunit = g/cm3
  Dvalue = 6.73
  Group = -> [Yb_element001]
  conduct = 2
  density = 1
  expand = 3
  formula = Yb
  name = G4_Yb
  specific = 4
FEATURE [App::DocumentObjectGroupPython] Lu_element001  label="Lu_element : 1"  # scripted group (container) (typed FeaturePython)
  n = 1
  ref = Lu_element
FEATURE [App::DocumentObjectGroupPython] G4_Lu  # scripted group (container) (typed FeaturePython)
  Dunit = g/cm3
  Dvalue = 9.84
  Group = -> [Lu_element001]
  conduct = 2
  density = 1
  expand = 3
  formula = Lu
  name = G4_Lu
  specific = 4
FEATURE [App::DocumentObjectGroupPython] Hf_element001  label="Hf_element : 1"  # scripted group (container) (typed FeaturePython)
  n = 1
  ref = Hf_element
FEATURE [App::DocumentObjectGroupPython] G4_Hf  # scripted group (container) (typed FeaturePython)
  Dunit = g/cm3
  Dvalue = 13.31
  Group = -> [Hf_element001]
  conduct = 2
  density = 1
  expand = 3
  formula = Hf
  name = G4_Hf
  specific = 4
FEATURE [App::DocumentObjectGroupPython] Ta_element001  label="Ta_element : 1"  # scripted group (container) (typed FeaturePython)
  n = 1
  ref = Ta_element
FEATURE [App::DocumentObjectGroupPython] G4_Ta  # scripted group (container) (typed FeaturePython)
  Dunit = g/cm3
  Dvalue = 16.654
  Group = -> [Ta_element001]
  conduct = 2
  density = 1
  expand = 3
  formula = Ta
  name = G4_Ta
  specific = 4
FEATURE [App::DocumentObjectGroupPython] W_element004  label="W_element : 004"  # scripted group (container) (typed FeaturePython)
  n = 1
  ref = W_element
FEATURE [App::DocumentObjectGroupPython] G4_W  # scripted group (container) (typed FeaturePython)
  Dunit = g/cm3
  Dvalue = 19.3
  Group = -> [W_element004]
  conduct = 2
  density = 1
  expand = 3
  formula = W
  name = G4_W
  specific = 4
FEATURE [App::DocumentObjectGroupPython] Re_element001  label="Re_element : 1"  # scripted group (container) (typed FeaturePython)
  n = 1
  ref = Re_element
FEATURE [App::DocumentObjectGroupPython] G4_Re  # scripted group (container) (typed FeaturePython)
  Dunit = g/cm3
  Dvalue = 21.02
  Group = -> [Re_element001]
  conduct = 2
  density = 1
  expand = 3
  formula = Re
  name = G4_Re
  specific = 4
FEATURE [App::DocumentObjectGroupPython] Os_element001  label="Os_element : 1"  # scripted group (container) (typed FeaturePython)
  n = 1
  ref = Os_element
FEATURE [App::DocumentObjectGroupPython] G4_Os  # scripted group (container) (typed FeaturePython)
  Dunit = g/cm3
  Dvalue = 22.57
  Group = -> [Os_element001]
  conduct = 2
  density = 1
  expand = 3
  formula = Os
  name = G4_Os
  specific = 4
FEATURE [App::DocumentObjectGroupPython] Ir_element001  label="Ir_element : 1"  # scripted group (container) (typed FeaturePython)
  n = 1
  ref = Ir_element
FEATURE [App::DocumentObjectGroupPython] G4_Ir  # scripted group (container) (typed FeaturePython)
  Dunit = g/cm3
  Dvalue = 22.42
  Group = -> [Ir_element001]
  conduct = 2
  density = 1
  expand = 3
  formula = Ir
  name = G4_Ir
  specific = 4
FEATURE [App::DocumentObjectGroupPython] Pt_element001  label="Pt_element : 1"  # scripted group (container) (typed FeaturePython)
  n = 1
  ref = Pt_element
FEATURE [App::DocumentObjectGroupPython] G4_Pt  # scripted group (container) (typed FeaturePython)
  Dunit = g/cm3
  Dvalue = 21.45
  Group = -> [Pt_element001]
  conduct = 2
  density = 1
  expand = 3
  formula = Pt
  name = G4_Pt
  specific = 4
FEATURE [App::DocumentObjectGroupPython] Au_element001  label="Au_element : 1"  # scripted group (container) (typed FeaturePython)
  n = 1
  ref = Au_element
FEATURE [App::DocumentObjectGroupPython] G4_Au  # scripted group (container) (typed FeaturePython)
  Dunit = g/cm3
  Dvalue = 19.32
  Group = -> [Au_element001]
  conduct = 2
  density = 1
  expand = 3
  formula = Au
  name = G4_Au
  specific = 4
FEATURE [App::DocumentObjectGroupPython] Hg_element002  label="Hg_element : 002"  # scripted group (container) (typed FeaturePython)
  n = 1
  ref = Hg_element
FEATURE [App::DocumentObjectGroupPython] G4_Hg  # scripted group (container) (typed FeaturePython)
  Dunit = g/cm3
  Dvalue = 13.546
  Group = -> [Hg_element002]
  conduct = 2
  density = 1
  expand = 3
  formula = Hg
  name = G4_Hg
  specific = 4
FEATURE [App::DocumentObjectGroupPython] Tl_element002  label="Tl_element : 002"  # scripted group (container) (typed FeaturePython)
  n = 1
  ref = Tl_element
FEATURE [App::DocumentObjectGroupPython] G4_Tl  # scripted group (container) (typed FeaturePython)
  Dunit = g/cm3
  Dvalue = 11.72
  Group = -> [Tl_element002]
  conduct = 2
  density = 1
  expand = 3
  formula = Tl
  name = G4_Tl
  specific = 4
FEATURE [App::DocumentObjectGroupPython] Pb_element003  label="Pb_element : 1"  # scripted group (container) (typed FeaturePython)
  n = 1
  ref = Pb_element
FEATURE [App::DocumentObjectGroupPython] G4_Pb  # scripted group (container) (typed FeaturePython)
  Dunit = g/cm3
  Dvalue = 11.35
  Group = -> [Pb_element003]
  conduct = 2
  density = 1
  expand = 3
  formula = Pb
  name = G4_Pb
  specific = 4
FEATURE [App::DocumentObjectGroupPython] Bi_element002  label="Bi_element : 1"  # scripted group (container) (typed FeaturePython)
  n = 1
  ref = Bi_element
FEATURE [App::DocumentObjectGroupPython] G4_Bi  # scripted group (container) (typed FeaturePython)
  Dunit = g/cm3
  Dvalue = 9.747
  Group = -> [Bi_element002]
  conduct = 2
  density = 1
  expand = 3
  formula = Bi
  name = G4_Bi
  specific = 4
FEATURE [App::DocumentObjectGroupPython] Po_element001  label="Po_element : 1"  # scripted group (container) (typed FeaturePython)
  n = 1
  ref = Po_element
FEATURE [App::DocumentObjectGroupPython] G4_Po  # scripted group (container) (typed FeaturePython)
  Dunit = g/cm3
  Dvalue = 9.32
  Group = -> [Po_element001]
  conduct = 2
  density = 1
  expand = 3
  formula = Po
  name = G4_Po
  specific = 4
FEATURE [App::DocumentObjectGroupPython] At_element001  label="At_element : 1"  # scripted group (container) (typed FeaturePython)
  n = 1
  ref = At_element
FEATURE [App::DocumentObjectGroupPython] G4_At  # scripted group (container) (typed FeaturePython)
  Dunit = g/cm3
  Dvalue = 9.32
  Group = -> [At_element001]
  conduct = 2
  density = 1
  expand = 3
  formula = At
  name = G4_At
  specific = 4
FEATURE [App::DocumentObjectGroupPython] Rn_element001  label="Rn_element : 1"  # scripted group (container) (typed FeaturePython)
  n = 1
  ref = Rn_element
FEATURE [App::DocumentObjectGroupPython] G4_Rn  # scripted group (container) (typed FeaturePython)
  Dunit = g/cm3
  Dvalue = 0.00900662
  Group = -> [Rn_element001]
  conduct = 2
  density = 1
  expand = 3
  formula = Rn
  name = G4_Rn
  specific = 4
FEATURE [App::DocumentObjectGroupPython] Fr_element001  label="Fr_element : 1"  # scripted group (container) (typed FeaturePython)
  n = 1
  ref = Fr_element
FEATURE [App::DocumentObjectGroupPython] G4_Fr  # scripted group (container) (typed FeaturePython)
  Dunit = g/cm3
  Dvalue = 1
  Group = -> [Fr_element001]
  conduct = 2
  density = 1
  expand = 3
  formula = Fr
  name = G4_Fr
  specific = 4
FEATURE [App::DocumentObjectGroupPython] Ra_element001  label="Ra_element : 1"  # scripted group (container) (typed FeaturePython)
  n = 1
  ref = Ra_element
FEATURE [App::DocumentObjectGroupPython] G4_Ra  # scripted group (container) (typed FeaturePython)
  Dunit = g/cm3
  Dvalue = 5
  Group = -> [Ra_element001]
  conduct = 2
  density = 1
  expand = 3
  formula = Ra
  name = G4_Ra
  specific = 4
FEATURE [App::DocumentObjectGroupPython] Ac_element001  label="Ac_element : 1"  # scripted group (container) (typed FeaturePython)
  n = 1
  ref = Ac_element
FEATURE [App::DocumentObjectGroupPython] G4_Ac  # scripted group (container) (typed FeaturePython)
  Dunit = g/cm3
  Dvalue = 10.07
  Group = -> [Ac_element001]
  conduct = 2
  density = 1
  expand = 3
  formula = Ac
  name = G4_Ac
  specific = 4
FEATURE [App::DocumentObjectGroupPython] Th_element001  label="Th_element : 1"  # scripted group (container) (typed FeaturePython)
  n = 1
  ref = Th_element
FEATURE [App::DocumentObjectGroupPython] G4_Th  # scripted group (container) (typed FeaturePython)
  Dunit = g/cm3
  Dvalue = 11.72
  Group = -> [Th_element001]
  conduct = 2
  density = 1
  expand = 3
  formula = Th
  name = G4_Th
  specific = 4
FEATURE [App::DocumentObjectGroupPython] Pa_element001  label="Pa_element : 1"  # scripted group (container) (typed FeaturePython)
  n = 1
  ref = Pa_element
FEATURE [App::DocumentObjectGroupPython] G4_Pa  # scripted group (container) (typed FeaturePython)
  Dunit = g/cm3
  Dvalue = 15.37
  Group = -> [Pa_element001]
  conduct = 2
  density = 1
  expand = 3
  formula = Pa
  name = G4_Pa
  specific = 4
FEATURE [App::DocumentObjectGroupPython] U_element004  label="U_element : 004"  # scripted group (container) (typed FeaturePython)
  n = 1
  ref = U_element
FEATURE [App::DocumentObjectGroupPython] G4_U  # scripted group (container) (typed FeaturePython)
  Dunit = g/cm3
  Dvalue = 18.95
  Group = -> [U_element004]
  conduct = 2
  density = 1
  expand = 3
  formula = U
  name = G4_U
  specific = 4
FEATURE [App::DocumentObjectGroupPython] Np_element001  label="Np_element : 1"  # scripted group (container) (typed FeaturePython)
  n = 1
  ref = Np_element
FEATURE [App::DocumentObjectGroupPython] G4_Np  # scripted group (container) (typed FeaturePython)
  Dunit = g/cm3
  Dvalue = 20.25
  Group = -> [Np_element001]
  conduct = 2
  density = 1
  expand = 3
  formula = Np
  name = G4_Np
  specific = 4
FEATURE [App::DocumentObjectGroupPython] Pu_element002  label="Pu_element : 002"  # scripted group (container) (typed FeaturePython)
  n = 1
  ref = Pu_element
FEATURE [App::DocumentObjectGroupPython] G4_Pu  # scripted group (container) (typed FeaturePython)
  Dunit = g/cm3
  Dvalue = 19.84
  Group = -> [Pu_element002]
  conduct = 2
  density = 1
  expand = 3
  formula = Pu
  name = G4_Pu
  specific = 4
FEATURE [App::DocumentObjectGroupPython] Am_element001  label="Am_element : 1"  # scripted group (container) (typed FeaturePython)
  n = 1
  ref = Am_element
FEATURE [App::DocumentObjectGroupPython] G4_Am  # scripted group (container) (typed FeaturePython)
  Dunit = g/cm3
  Dvalue = 13.67
  Group = -> [Am_element001]
  conduct = 2
  density = 1
  expand = 3
  formula = Am
  name = G4_Am
  specific = 4
FEATURE [App::DocumentObjectGroupPython] Cm_element001  label="Cm_element : 1"  # scripted group (container) (typed FeaturePython)
  n = 1
  ref = Cm_element
FEATURE [App::DocumentObjectGroupPython] G4_Cm  # scripted group (container) (typed FeaturePython)
  Dunit = g/cm3
  Dvalue = 13.51
  Group = -> [Cm_element001]
  conduct = 2
  density = 1
  expand = 3
  formula = Cm
  name = G4_Cm
  specific = 4
FEATURE [App::DocumentObjectGroupPython] Bk_element001  label="Bk_element : 1"  # scripted group (container) (typed FeaturePython)
  n = 1
  ref = Bk_element
FEATURE [App::DocumentObjectGroupPython] G4_Bk  # scripted group (container) (typed FeaturePython)
  Dunit = g/cm3
  Dvalue = 14
  Group = -> [Bk_element001]
  conduct = 2
  density = 1
  expand = 3
  formula = Bk
  name = G4_Bk
  specific = 4
FEATURE [App::DocumentObjectGroupPython] Cf_element001  label="Cf_element : 1"  # scripted group (container) (typed FeaturePython)
  n = 1
  ref = Cf_element
FEATURE [App::DocumentObjectGroupPython] G4_Cf  # scripted group (container) (typed FeaturePython)
  Dunit = g/cm3
  Dvalue = 10
  Group = -> [Cf_element001]
  conduct = 2
  density = 1
  expand = 3
  formula = Cf
  name = G4_Cf
  specific = 4
FEATURE [App::DocumentObjectGroupPython] Element  # scripted group (container) (typed FeaturePython)
  Group = -> [G4_H,G4_He,G4_Li,G4_Be,G4_B,G4_C,G4_N,G4_O,G4_F,G4_Ne,G4_Na,G4_Mg,G4_Al,G4_Si,G4_P,G4_S,G4_Cl,G4_Ar,G4_K,G4_Ca,G4_Sc,G4_Ti,G4_V,G4_Cr,G4_Mn,G4_Fe,G4_Co,G4_Ni,G4_Cu,G4_Zn,G4_Ga,G4_Ge,G4_As,G4_Se,G4_Br,G4_Kr,G4_Rb,G4_Sr,G4_Y,G4_Zr,G4_Nb,G4_Mo,G4_Tc,G4_Ru,G4_Rh,G4_Pd,G4_Ag,G4_Cd,G4_In,G4_Sn,G4_Sb,G4_Te,G4_I,G4_Xe,G4_Cs,G4_Ba,G4_La,G4_Ce,G4_Pr,G4_Nd,G4_Pm,G4_Sm,G4_Eu,G4_Gd,G4_Tb,G4_Dy,G4_Ho,G4_Er,+30 more]
FEATURE [App::DocumentObjectGroupPython] H_element114  label="H_element : 063"  # scripted group (container) (typed FeaturePython)
  n = 2
  ref = H_element
FEATURE [App::DocumentObjectGroupPython] G4_lH2  # scripted group (container) (typed FeaturePython)
  Dunit = g/cm3
  Dvalue = 0.0708
  Group = -> [H_element114]
  conduct = 2
  density = 1
  expand = 3
  formula = G4_lH2
  name = G4_lH2
  specific = 4
FEATURE [App::DocumentObjectGroupPython] N_element049  label="N_element : 022"  # scripted group (container) (typed FeaturePython)
  n = 2
  ref = N_element
FEATURE [App::DocumentObjectGroupPython] G4_lN2  # scripted group (container) (typed FeaturePython)
  Dunit = g/cm3
  Dvalue = 0.807
  Group = -> [N_element049]
  conduct = 2
  density = 1
  expand = 3
  formula = G4_lN2
  name = G4_lN2
  specific = 4
FEATURE [App::DocumentObjectGroupPython] O_element106  label="O_element : 060"  # scripted group (container) (typed FeaturePython)
  n = 2
  ref = O_element
FEATURE [App::DocumentObjectGroupPython] G4_lO2  # scripted group (container) (typed FeaturePython)
  Dunit = g/cm3
  Dvalue = 1.141
  Group = -> [O_element106]
  conduct = 2
  density = 1
  expand = 3
  formula = G4_lO2
  name = G4_lO2
  specific = 4
FEATURE [App::DocumentObjectGroupPython] Ar  label="Ar : 1"  # scripted group (container) (typed FeaturePython)
  n = 1
  ref = Ar
FEATURE [App::DocumentObjectGroupPython] G4_lAr  # scripted group (container) (typed FeaturePython)
  Dunit = g/cm3
  Dvalue = 1.396
  Group = -> [Ar]
  conduct = 2
  density = 1
  expand = 3
  formula = G4_lAr
  name = G4_lAr
  specific = 4
FEATURE [App::DocumentObjectGroupPython] Br  label="Br : 1"  # scripted group (container) (typed FeaturePython)
  n = 1
  ref = Br
FEATURE [App::DocumentObjectGroupPython] G4_lBr  # scripted group (container) (typed FeaturePython)
  Dunit = g/cm3
  Dvalue = 3.1028
  Group = -> [Br]
  conduct = 2
  density = 1
  expand = 3
  formula = G4_lBr
  name = G4_lBr
  specific = 4
FEATURE [App::DocumentObjectGroupPython] Kr  label="Kr : 1"  # scripted group (container) (typed FeaturePython)
  n = 1
  ref = Kr
FEATURE [App::DocumentObjectGroupPython] G4_lKr  # scripted group (container) (typed FeaturePython)
  Dunit = g/cm3
  Dvalue = 2.418
  Group = -> [Kr]
  conduct = 2
  density = 1
  expand = 3
  formula = G4_lKr
  name = G4_lKr
  specific = 4
FEATURE [App::DocumentObjectGroupPython] Xe  label="Xe : 1"  # scripted group (container) (typed FeaturePython)
  n = 1
  ref = Xe
FEATURE [App::DocumentObjectGroupPython] G4_lXe  # scripted group (container) (typed FeaturePython)
  Dunit = g/cm3
  Dvalue = 2.953
  Group = -> [Xe]
  conduct = 2
  density = 1
  expand = 3
  formula = G4_lXe
  name = G4_lXe
  specific = 4
FEATURE [App::DocumentObjectGroupPython] O_element107  label="O_element : 061"  # scripted group (container) (typed FeaturePython)
  n = 4
  ref = O_element
FEATURE [App::DocumentObjectGroupPython] Pb_element004  label="Pb_element : 002"  # scripted group (container) (typed FeaturePython)
  n = 1
  ref = Pb_element
FEATURE [App::DocumentObjectGroupPython] W_element005  label="W_element : 005"  # scripted group (container) (typed FeaturePython)
  n = 1
  ref = W_element
FEATURE [App::DocumentObjectGroupPython] G4_PbWO4  # scripted group (container) (typed FeaturePython)
  Dunit = g/cm3
  Dvalue = 8.28
  Group = -> [O_element107,Pb_element004,W_element005]
  conduct = 2
  density = 1
  expand = 3
  formula = G4_PbWO4
  name = G4_PbWO4
  specific = 4
FEATURE [App::DocumentObjectGroupPython] alactic  label="alactic : 1"  # scripted group (container) (typed FeaturePython)
  n = 1
  ref = alactic
FEATURE [App::DocumentObjectGroupPython] G4_Galactic  # scripted group (container) (typed FeaturePython)
  Dunit = g/cm3
  Dvalue = 0
  Group = -> [alactic]
  conduct = 2
  density = 1
  expand = 3
  formula = G4_Galactic
  name = G4_Galactic
  specific = 4
FEATURE [App::DocumentObjectGroupPython] RAPHITE_POROUS  label="RAPHITE_POROUS : 1"  # scripted group (container) (typed FeaturePython)
  n = 1
  ref = RAPHITE_POROUS
FEATURE [App::DocumentObjectGroupPython] G4_GRAPHITE_POROUS  # scripted group (container) (typed FeaturePython)
  Dunit = g/cm3
  Dvalue = 1.7
  Group = -> [RAPHITE_POROUS]
  conduct = 2
  density = 1
  expand = 3
  formula = G4_GRAPHITE_POROUS
  name = G4_GRAPHITE_POROUS
  specific = 4
FEATURE [App::DocumentObjectGroupPython] H_element115  label="H_element : 0.150"  # scripted group (container) (typed FeaturePython)
  n = 0.080538
FEATURE [App::DocumentObjectGroupPython] C_element125  label="C_element : 0.600"  # scripted group (container) (typed FeaturePython)
  n = 0.599848
FEATURE [App::DocumentObjectGroupPython] O_element108  label="O_element : 0.320"  # scripted group (container) (typed FeaturePython)
  n = 0.319614
FEATURE [App::DocumentObjectGroupPython] G4_LUCITE  # scripted group (container) (typed FeaturePython)
  Dunit = g/cm3
  Dvalue = 1.19
  Group = -> [H_element115,C_element125,O_element108]
  conduct = 2
  density = 1
  expand = 3
  formula = G4_LUCITE
  name = G4_LUCITE
  specific = 4
FEATURE [App::DocumentObjectGroupPython] Cu_element002  label="Cu_element : 62"  # scripted group (container) (typed FeaturePython)
  n = 62
  ref = Cu_element
FEATURE [App::DocumentObjectGroupPython] Zn_element002  label="Zn_element : 35"  # scripted group (container) (typed FeaturePython)
  n = 35
  ref = Zn_element
FEATURE [App::DocumentObjectGroupPython] Pb_element005  label="Pb_element : 3"  # scripted group (container) (typed FeaturePython)
  n = 3
  ref = Pb_element
FEATURE [App::DocumentObjectGroupPython] G4_BRASS  # scripted group (container) (typed FeaturePython)
  Dunit = g/cm3
  Dvalue = 8.52
  Group = -> [Cu_element002,Zn_element002,Pb_element005]
  conduct = 2
  density = 1
  expand = 3
  formula = G4_BRASS
  name = G4_BRASS
  specific = 4
FEATURE [App::DocumentObjectGroupPython] Cu_element003  label="Cu_element : 89"  # scripted group (container) (typed FeaturePython)
  n = 89
  ref = Cu_element
FEATURE [App::DocumentObjectGroupPython] Zn_element003  label="Zn_element : 9"  # scripted group (container) (typed FeaturePython)
  n = 9
  ref = Zn_element
FEATURE [App::DocumentObjectGroupPython] Pb_element006  label="Pb_element : 2"  # scripted group (container) (typed FeaturePython)
  n = 2
  ref = Pb_element
FEATURE [App::DocumentObjectGroupPython] G4_BRONZE  # scripted group (container) (typed FeaturePython)
  Dunit = g/cm3
  Dvalue = 8.82
  Group = -> [Cu_element003,Zn_element003,Pb_element006]
  conduct = 2
  density = 1
  expand = 3
  formula = G4_BRONZE
  name = G4_BRONZE
  specific = 4
FEATURE [App::DocumentObjectGroupPython] Fe_element008  label="Fe_element : 74"  # scripted group (container) (typed FeaturePython)
  n = 74
  ref = Fe_element
FEATURE [App::DocumentObjectGroupPython] Cr_element002  label="Cr_element : 18"  # scripted group (container) (typed FeaturePython)
  n = 18
  ref = Cr_element
FEATURE [App::DocumentObjectGroupPython] Ni_element002  label="Ni_element : 8"  # scripted group (container) (typed FeaturePython)
  n = 8
  ref = Ni_element
FEATURE [App::DocumentObjectGroupPython] G4_STAINLESS_STEEL  label="G4_STAINLESS-STEEL"  # scripted group (container) (typed FeaturePython)
  Dunit = g/cm3
  Dvalue = 8
  Group = -> [Fe_element008,Cr_element002,Ni_element002]
  conduct = 2
  density = 1
  expand = 3
  formula = G4_STAINLESS-STEEL
  name = G4_STAINLESS-STEEL
  specific = 4
FEATURE [App::DocumentObjectGroupPython] H_element116  label="H_element : 064"  # scripted group (container) (typed FeaturePython)
  n = 18
  ref = H_element
FEATURE [App::DocumentObjectGroupPython] C_element126  label="C_element : 071"  # scripted group (container) (typed FeaturePython)
  n = 12
  ref = C_element
FEATURE [App::DocumentObjectGroupPython] O_element109  label="O_element : 062"  # scripted group (container) (typed FeaturePython)
  n = 7
  ref = O_element
FEATURE [App::DocumentObjectGroupPython] G4_CR39  # scripted group (container) (typed FeaturePython)
  Dunit = g/cm3
  Dvalue = 1.32
  Group = -> [H_element116,C_element126,O_element109]
  conduct = 2
  density = 1
  expand = 3
  formula = G4_CR39
  name = G4_CR39
  specific = 4
FEATURE [App::DocumentObjectGroupPython] H_element117  label="H_element : 38"  # scripted group (container) (typed FeaturePython)
  n = 38
  ref = H_element
FEATURE [App::DocumentObjectGroupPython] C_element127  label="C_element : 072"  # scripted group (container) (typed FeaturePython)
  n = 18
  ref = C_element
FEATURE [App::DocumentObjectGroupPython] O_element110  label="O_element : 063"  # scripted group (container) (typed FeaturePython)
  n = 1
  ref = O_element
FEATURE [App::DocumentObjectGroupPython] G4_OCTADECANOL  # scripted group (container) (typed FeaturePython)
  Dunit = g/cm3
  Dvalue = 0.812
  Group = -> [H_element117,C_element127,O_element110]
  conduct = 2
  density = 1
  expand = 3
  formula = G4_OCTADECANOL
  name = G4_OCTADECANOL
  specific = 4
FEATURE [App::DocumentObjectGroupPython] HEP  # scripted group (container) (typed FeaturePython)
  Group = -> [G4_lH2,G4_lN2,G4_lO2,G4_lAr,G4_lBr,G4_lKr,G4_lXe,G4_PbWO4,G4_Galactic,G4_GRAPHITE_POROUS,G4_LUCITE,G4_BRASS,G4_BRONZE,G4_STAINLESS_STEEL,G4_CR39,G4_OCTADECANOL]
FEATURE [App::DocumentObjectGroupPython] C_element128  label="C_element : 073"  # scripted group (container) (typed FeaturePython)
  n = 14
  ref = C_element
FEATURE [App::DocumentObjectGroupPython] H_element118  label="H_element : 065"  # scripted group (container) (typed FeaturePython)
  n = 10
  ref = H_element
FEATURE [App::DocumentObjectGroupPython] O_element111  label="O_element : 064"  # scripted group (container) (typed FeaturePython)
  n = 2
  ref = O_element
FEATURE [App::DocumentObjectGroupPython] N_element050  label="N_element : 023"  # scripted group (container) (typed FeaturePython)
  n = 2
  ref = N_element
FEATURE [App::DocumentObjectGroupPython] G4_KEVLAR  # scripted group (container) (typed FeaturePython)
  Dunit = g/cm3
  Dvalue = 1.44
  Group = -> [C_element128,H_element118,O_element111,N_element050]
  conduct = 2
  density = 1
  expand = 3
  formula = G4_KEVLAR
  name = G4_KEVLAR
  specific = 4
FEATURE [App::DocumentObjectGroupPython] C_element129  label="C_element : 074"  # scripted group (container) (typed FeaturePython)
  n = 10
  ref = C_element
FEATURE [App::DocumentObjectGroupPython] H_element119  label="H_element : 066"  # scripted group (container) (typed FeaturePython)
  n = 8
  ref = H_element
FEATURE [App::DocumentObjectGroupPython] O_element112  label="O_element : 065"  # scripted group (container) (typed FeaturePython)
  n = 4
  ref = O_element
FEATURE [App::DocumentObjectGroupPython] G4_DACRON  # scripted group (container) (typed FeaturePython)
  Dunit = g/cm3
  Dvalue = 1.4
  Group = -> [C_element129,H_element119,O_element112]
  conduct = 2
  density = 1
  expand = 3
  formula = G4_DACRON
  name = G4_DACRON
  specific = 4
FEATURE [App::DocumentObjectGroupPython] C_element130  label="C_element : 075"  # scripted group (container) (typed FeaturePython)
  n = 4
  ref = C_element
FEATURE [App::DocumentObjectGroupPython] H_element120  label="H_element : 067"  # scripted group (container) (typed FeaturePython)
  n = 5
  ref = H_element
FEATURE [App::DocumentObjectGroupPython] Cl_element030  label="Cl_element : 016"  # scripted group (container) (typed FeaturePython)
  n = 1
  ref = Cl_element
FEATURE [App::DocumentObjectGroupPython] G4_NEOPRENE  # scripted group (container) (typed FeaturePython)
  Dunit = g/cm3
  Dvalue = 1.23
  Group = -> [C_element130,H_element120,Cl_element030]
  conduct = 2
  density = 1
  expand = 3
  formula = G4_NEOPRENE
  name = G4_NEOPRENE
  specific = 4
FEATURE [App::DocumentObjectGroupPython] Space  # scripted group (container) (typed FeaturePython)
  Group = -> [G4_KEVLAR,G4_DACRON,G4_NEOPRENE]
FEATURE [App::DocumentObjectGroupPython] H_element121  label="H_element : 068"  # scripted group (container) (typed FeaturePython)
  n = 5
  ref = H_element
FEATURE [App::DocumentObjectGroupPython] C_element131  label="C_element : 076"  # scripted group (container) (typed FeaturePython)
  n = 4
  ref = C_element
FEATURE [App::DocumentObjectGroupPython] N_element051  label="N_element : 3"  # scripted group (container) (typed FeaturePython)
  n = 3
  ref = N_element
FEATURE [App::DocumentObjectGroupPython] O_element113  label="O_element : 066"  # scripted group (container) (typed FeaturePython)
  n = 1
  ref = O_element
FEATURE [App::DocumentObjectGroupPython] G4_CYTOSINE  # scripted group (container) (typed FeaturePython)
  Dunit = g/cm3
  Dvalue = 1.55
  Group = -> [H_element121,C_element131,N_element051,O_element113]
  conduct = 2
  density = 1
  expand = 3
  formula = G4_CYTOSINE
  name = G4_CYTOSINE
  specific = 4
FEATURE [App::DocumentObjectGroupPython] H_element122  label="H_element : 069"  # scripted group (container) (typed FeaturePython)
  n = 6
  ref = H_element
FEATURE [App::DocumentObjectGroupPython] C_element132  label="C_element : 077"  # scripted group (container) (typed FeaturePython)
  n = 5
  ref = C_element
FEATURE [App::DocumentObjectGroupPython] N_element052  label="N_element : 024"  # scripted group (container) (typed FeaturePython)
  n = 2
  ref = N_element
FEATURE [App::DocumentObjectGroupPython] O_element114  label="O_element : 067"  # scripted group (container) (typed FeaturePython)
  n = 2
  ref = O_element
FEATURE [App::DocumentObjectGroupPython] G4_THYMINE  # scripted group (container) (typed FeaturePython)
  Dunit = g/cm3
  Dvalue = 1.23
  Group = -> [H_element122,C_element132,N_element052,O_element114]
  conduct = 2
  density = 1
  expand = 3
  formula = G4_THYMINE
  name = G4_THYMINE
  specific = 4
FEATURE [App::DocumentObjectGroupPython] H_element123  label="H_element : 070"  # scripted group (container) (typed FeaturePython)
  n = 4
  ref = H_element
FEATURE [App::DocumentObjectGroupPython] C_element133  label="C_element : 078"  # scripted group (container) (typed FeaturePython)
  n = 4
  ref = C_element
FEATURE [App::DocumentObjectGroupPython] N_element053  label="N_element : 025"  # scripted group (container) (typed FeaturePython)
  n = 2
  ref = N_element
FEATURE [App::DocumentObjectGroupPython] O_element115  label="O_element : 068"  # scripted group (container) (typed FeaturePython)
  n = 2
  ref = O_element
FEATURE [App::DocumentObjectGroupPython] G4_URACIL  # scripted group (container) (typed FeaturePython)
  Dunit = g/cm3
  Dvalue = 1.32
  Group = -> [H_element123,C_element133,N_element053,O_element115]
  conduct = 2
  density = 1
  expand = 3
  formula = G4_URACIL
  name = G4_URACIL
  specific = 4
FEATURE [App::DocumentObjectGroupPython] H_element124  label="H_element : 071"  # scripted group (container) (typed FeaturePython)
  n = 4
  ref = H_element
FEATURE [App::DocumentObjectGroupPython] C_element134  label="C_element : 079"  # scripted group (container) (typed FeaturePython)
  n = 5
  ref = C_element
FEATURE [App::DocumentObjectGroupPython] N_element054  label="N_element : 026"  # scripted group (container) (typed FeaturePython)
  n = 5
  ref = N_element
FEATURE [App::DocumentObjectGroupPython] G4_DNA_ADENINE  # scripted group (container) (typed FeaturePython)
  Dunit = g/cm3
  Dvalue = 1
  Group = -> [H_element124,C_element134,N_element054]
  conduct = 2
  density = 1
  expand = 3
  formula = G4_DNA_ADENINE
  name = G4_DNA_ADENINE
  specific = 4
FEATURE [App::DocumentObjectGroupPython] H_element125  label="H_element : 072"  # scripted group (container) (typed FeaturePython)
  n = 4
  ref = H_element
FEATURE [App::DocumentObjectGroupPython] C_element135  label="C_element : 080"  # scripted group (container) (typed FeaturePython)
  n = 5
  ref = C_element
FEATURE [App::DocumentObjectGroupPython] N_element055  label="N_element : 027"  # scripted group (container) (typed FeaturePython)
  n = 5
  ref = N_element
FEATURE [App::DocumentObjectGroupPython] O_element116  label="O_element : 069"  # scripted group (container) (typed FeaturePython)
  n = 1
  ref = O_element
FEATURE [App::DocumentObjectGroupPython] G4_DNA_GUANINE  # scripted group (container) (typed FeaturePython)
  Dunit = g/cm3
  Dvalue = 1
  Group = -> [H_element125,C_element135,N_element055,O_element116]
  conduct = 2
  density = 1
  expand = 3
  formula = G4_DNA_GUANINE
  name = G4_DNA_GUANINE
  specific = 4
FEATURE [App::DocumentObjectGroupPython] H_element126  label="H_element : 073"  # scripted group (container) (typed FeaturePython)
  n = 4
  ref = H_element
FEATURE [App::DocumentObjectGroupPython] C_element136  label="C_element : 081"  # scripted group (container) (typed FeaturePython)
  n = 4
  ref = C_element
FEATURE [App::DocumentObjectGroupPython] N_element056  label="N_element : 028"  # scripted group (container) (typed FeaturePython)
  n = 3
  ref = N_element
FEATURE [App::DocumentObjectGroupPython] O_element117  label="O_element : 070"  # scripted group (container) (typed FeaturePython)
  n = 1
  ref = O_element
FEATURE [App::DocumentObjectGroupPython] G4_DNA_CYTOSINE  # scripted group (container) (typed FeaturePython)
  Dunit = g/cm3
  Dvalue = 1
  Group = -> [H_element126,C_element136,N_element056,O_element117]
  conduct = 2
  density = 1
  expand = 3
  formula = G4_DNA_CYTOSINE
  name = G4_DNA_CYTOSINE
  specific = 4
FEATURE [App::DocumentObjectGroupPython] H_element127  label="H_element : 074"  # scripted group (container) (typed FeaturePython)
  n = 5
  ref = H_element
FEATURE [App::DocumentObjectGroupPython] C_element137  label="C_element : 082"  # scripted group (container) (typed FeaturePython)
  n = 5
  ref = C_element
FEATURE [App::DocumentObjectGroupPython] N_element057  label="N_element : 029"  # scripted group (container) (typed FeaturePython)
  n = 2
  ref = N_element
FEATURE [App::DocumentObjectGroupPython] O_element118  label="O_element : 071"  # scripted group (container) (typed FeaturePython)
  n = 2
  ref = O_element
FEATURE [App::DocumentObjectGroupPython] G4_DNA_THYMINE  # scripted group (container) (typed FeaturePython)
  Dunit = g/cm3
  Dvalue = 1
  Group = -> [H_element127,C_element137,N_element057,O_element118]
  conduct = 2
  density = 1
  expand = 3
  formula = G4_DNA_THYMINE
  name = G4_DNA_THYMINE
  specific = 4
FEATURE [App::DocumentObjectGroupPython] H_element128  label="H_element : 075"  # scripted group (container) (typed FeaturePython)
  n = 3
  ref = H_element
FEATURE [App::DocumentObjectGroupPython] C_element138  label="C_element : 083"  # scripted group (container) (typed FeaturePython)
  n = 4
  ref = C_element
FEATURE [App::DocumentObjectGroupPython] N_element058  label="N_element : 030"  # scripted group (container) (typed FeaturePython)
  n = 2
  ref = N_element
FEATURE [App::DocumentObjectGroupPython] O_element119  label="O_element : 072"  # scripted group (container) (typed FeaturePython)
  n = 2
  ref = O_element
FEATURE [App::DocumentObjectGroupPython] G4_DNA_URACIL  # scripted group (container) (typed FeaturePython)
  Dunit = g/cm3
  Dvalue = 1
  Group = -> [H_element128,C_element138,N_element058,O_element119]
  conduct = 2
  density = 1
  expand = 3
  formula = G4_DNA_URACIL
  name = G4_DNA_URACIL
  specific = 4
FEATURE [App::DocumentObjectGroupPython] H_element129  label="H_element : 076"  # scripted group (container) (typed FeaturePython)
  n = 10
  ref = H_element
FEATURE [App::DocumentObjectGroupPython] C_element139  label="C_element : 084"  # scripted group (container) (typed FeaturePython)
  n = 10
  ref = C_element
FEATURE [App::DocumentObjectGroupPython] N_element059  label="N_element : 031"  # scripted group (container) (typed FeaturePython)
  n = 5
  ref = N_element
FEATURE [App::DocumentObjectGroupPython] O_element120  label="O_element : 073"  # scripted group (container) (typed FeaturePython)
  n = 4
  ref = O_element
FEATURE [App::DocumentObjectGroupPython] G4_DNA_ADENOSINE  # scripted group (container) (typed FeaturePython)
  Dunit = g/cm3
  Dvalue = 1
  Group = -> [H_element129,C_element139,N_element059,O_element120]
  conduct = 2
  density = 1
  expand = 3
  formula = G4_DNA_ADENOSINE
  name = G4_DNA_ADENOSINE
  specific = 4
FEATURE [App::DocumentObjectGroupPython] H_element130  label="H_element : 077"  # scripted group (container) (typed FeaturePython)
  n = 10
  ref = H_element
FEATURE [App::DocumentObjectGroupPython] C_element140  label="C_element : 085"  # scripted group (container) (typed FeaturePython)
  n = 10
  ref = C_element
FEATURE [App::DocumentObjectGroupPython] N_element060  label="N_element : 032"  # scripted group (container) (typed FeaturePython)
  n = 5
  ref = N_element
FEATURE [App::DocumentObjectGroupPython] O_element121  label="O_element : 074"  # scripted group (container) (typed FeaturePython)
  n = 5
  ref = O_element
FEATURE [App::DocumentObjectGroupPython] G4_DNA_GUANOSINE  # scripted group (container) (typed FeaturePython)
  Dunit = g/cm3
  Dvalue = 1
  Group = -> [H_element130,C_element140,N_element060,O_element121]
  conduct = 2
  density = 1
  expand = 3
  formula = G4_DNA_GUANOSINE
  name = G4_DNA_GUANOSINE
  specific = 4
FEATURE [App::DocumentObjectGroupPython] H_element131  label="H_element : 078"  # scripted group (container) (typed FeaturePython)
  n = 10
  ref = H_element
FEATURE [App::DocumentObjectGroupPython] C_element141  label="C_element : 086"  # scripted group (container) (typed FeaturePython)
  n = 9
  ref = C_element
FEATURE [App::DocumentObjectGroupPython] N_element061  label="N_element : 033"  # scripted group (container) (typed FeaturePython)
  n = 3
  ref = N_element
FEATURE [App::DocumentObjectGroupPython] O_element122  label="O_element : 075"  # scripted group (container) (typed FeaturePython)
  n = 5
  ref = O_element
FEATURE [App::DocumentObjectGroupPython] G4_DNA_CYTIDINE  # scripted group (container) (typed FeaturePython)
  Dunit = g/cm3
  Dvalue = 1
  Group = -> [H_element131,C_element141,N_element061,O_element122]
  conduct = 2
  density = 1
  expand = 3
  formula = G4_DNA_CYTIDINE
  name = G4_DNA_CYTIDINE
  specific = 4
FEATURE [App::DocumentObjectGroupPython] H_element132  label="H_element : 079"  # scripted group (container) (typed FeaturePython)
  n = 9
  ref = H_element
FEATURE [App::DocumentObjectGroupPython] C_element142  label="C_element : 087"  # scripted group (container) (typed FeaturePython)
  n = 9
  ref = C_element
FEATURE [App::DocumentObjectGroupPython] N_element062  label="N_element : 034"  # scripted group (container) (typed FeaturePython)
  n = 2
  ref = N_element
FEATURE [App::DocumentObjectGroupPython] O_element123  label="O_element : 076"  # scripted group (container) (typed FeaturePython)
  n = 6
  ref = O_element
FEATURE [App::DocumentObjectGroupPython] G4_DNA_URIDINE  # scripted group (container) (typed FeaturePython)
  Dunit = g/cm3
  Dvalue = 1
  Group = -> [H_element132,C_element142,N_element062,O_element123]
  conduct = 2
  density = 1
  expand = 3
  formula = G4_DNA_URIDINE
  name = G4_DNA_URIDINE
  specific = 4
FEATURE [App::DocumentObjectGroupPython] H_element133  label="H_element : 080"  # scripted group (container) (typed FeaturePython)
  n = 11
  ref = H_element
FEATURE [App::DocumentObjectGroupPython] C_element143  label="C_element : 088"  # scripted group (container) (typed FeaturePython)
  n = 10
  ref = C_element
FEATURE [App::DocumentObjectGroupPython] N_element063  label="N_element : 035"  # scripted group (container) (typed FeaturePython)
  n = 2
  ref = N_element
FEATURE [App::DocumentObjectGroupPython] O_element124  label="O_element : 077"  # scripted group (container) (typed FeaturePython)
  n = 6
  ref = O_element
FEATURE [App::DocumentObjectGroupPython] G4_DNA_METHYLURIDINE  # scripted group (container) (typed FeaturePython)
  Dunit = g/cm3
  Dvalue = 1
  Group = -> [H_element133,C_element143,N_element063,O_element124]
  conduct = 2
  density = 1
  expand = 3
  formula = G4_DNA_METHYLURIDINE
  name = G4_DNA_METHYLURIDINE
  specific = 4
FEATURE [App::DocumentObjectGroupPython] P_element014  label="P_element : 003"  # scripted group (container) (typed FeaturePython)
  n = 1
  ref = P_element
FEATURE [App::DocumentObjectGroupPython] O_element125  label="O_element : 078"  # scripted group (container) (typed FeaturePython)
  n = 3
  ref = O_element
FEATURE [App::DocumentObjectGroupPython] G4_DNA_MONOPHOSPHATE  # scripted group (container) (typed FeaturePython)
  Dunit = g/cm3
  Dvalue = 1
  Group = -> [P_element014,O_element125]
  conduct = 2
  density = 1
  expand = 3
  formula = G4_DNA_MONOPHOSPHATE
  name = G4_DNA_MONOPHOSPHATE
  specific = 4
FEATURE [App::DocumentObjectGroupPython] H_element134  label="H_element : 081"  # scripted group (container) (typed FeaturePython)
  n = 10
  ref = H_element
FEATURE [App::DocumentObjectGroupPython] C_element144  label="C_element : 089"  # scripted group (container) (typed FeaturePython)
  n = 10
  ref = C_element
FEATURE [App::DocumentObjectGroupPython] N_element064  label="N_element : 036"  # scripted group (container) (typed FeaturePython)
  n = 5
  ref = N_element
FEATURE [App::DocumentObjectGroupPython] O_element126  label="O_element : 079"  # scripted group (container) (typed FeaturePython)
  n = 7
  ref = O_element
FEATURE [App::DocumentObjectGroupPython] P_element015  label="P_element : 004"  # scripted group (container) (typed FeaturePython)
  n = 1
  ref = P_element
FEATURE [App::DocumentObjectGroupPython] G4_DNA_A  # scripted group (container) (typed FeaturePython)
  Dunit = g/cm3
  Dvalue = 1
  Group = -> [H_element134,C_element144,N_element064,O_element126,P_element015]
  conduct = 2
  density = 1
  expand = 3
  formula = G4_DNA_A
  name = G4_DNA_A
  specific = 4
FEATURE [App::DocumentObjectGroupPython] H_element135  label="H_element : 082"  # scripted group (container) (typed FeaturePython)
  n = 10
  ref = H_element
FEATURE [App::DocumentObjectGroupPython] C_element145  label="C_element : 090"  # scripted group (container) (typed FeaturePython)
  n = 10
  ref = C_element
FEATURE [App::DocumentObjectGroupPython] N_element065  label="N_element : 037"  # scripted group (container) (typed FeaturePython)
  n = 5
  ref = N_element
FEATURE [App::DocumentObjectGroupPython] O_element127  label="O_element : 8"  # scripted group (container) (typed FeaturePython)
  n = 8
  ref = O_element
FEATURE [App::DocumentObjectGroupPython] P_element016  label="P_element : 005"  # scripted group (container) (typed FeaturePython)
  n = 1
  ref = P_element
FEATURE [App::DocumentObjectGroupPython] G4_DNA_G  # scripted group (container) (typed FeaturePython)
  Dunit = g/cm3
  Dvalue = 1
  Group = -> [H_element135,C_element145,N_element065,O_element127,P_element016]
  conduct = 2
  density = 1
  expand = 3
  formula = G4_DNA_G
  name = G4_DNA_G
  specific = 4
FEATURE [App::DocumentObjectGroupPython] H_element136  label="H_element : 083"  # scripted group (container) (typed FeaturePython)
  n = 10
  ref = H_element
FEATURE [App::DocumentObjectGroupPython] C_element146  label="C_element : 091"  # scripted group (container) (typed FeaturePython)
  n = 9
  ref = C_element
FEATURE [App::DocumentObjectGroupPython] N_element066  label="N_element : 038"  # scripted group (container) (typed FeaturePython)
  n = 3
  ref = N_element
FEATURE [App::DocumentObjectGroupPython] O_element128  label="O_element : 080"  # scripted group (container) (typed FeaturePython)
  n = 8
  ref = O_element
FEATURE [App::DocumentObjectGroupPython] P_element017  label="P_element : 006"  # scripted group (container) (typed FeaturePython)
  n = 1
  ref = P_element
FEATURE [App::DocumentObjectGroupPython] G4_DNA_C  # scripted group (container) (typed FeaturePython)
  Dunit = g/cm3
  Dvalue = 1
  Group = -> [H_element136,C_element146,N_element066,O_element128,P_element017]
  conduct = 2
  density = 1
  expand = 3
  formula = G4_DNA_C
  name = G4_DNA_C
  specific = 4
FEATURE [App::DocumentObjectGroupPython] H_element137  label="H_element : 084"  # scripted group (container) (typed FeaturePython)
  n = 9
  ref = H_element
FEATURE [App::DocumentObjectGroupPython] C_element147  label="C_element : 092"  # scripted group (container) (typed FeaturePython)
  n = 9
  ref = C_element
FEATURE [App::DocumentObjectGroupPython] N_element067  label="N_element : 039"  # scripted group (container) (typed FeaturePython)
  n = 2
  ref = N_element
FEATURE [App::DocumentObjectGroupPython] O_element129  label="O_element : 9"  # scripted group (container) (typed FeaturePython)
  n = 9
  ref = O_element
FEATURE [App::DocumentObjectGroupPython] P_element018  label="P_element : 007"  # scripted group (container) (typed FeaturePython)
  n = 1
  ref = P_element
FEATURE [App::DocumentObjectGroupPython] G4_DNA_U  # scripted group (container) (typed FeaturePython)
  Dunit = g/cm3
  Dvalue = 1
  Group = -> [H_element137,C_element147,N_element067,O_element129,P_element018]
  conduct = 2
  density = 1
  expand = 3
  formula = G4_DNA_U
  name = G4_DNA_U
  specific = 4
FEATURE [App::DocumentObjectGroupPython] H_element138  label="H_element : 085"  # scripted group (container) (typed FeaturePython)
  n = 11
  ref = H_element
FEATURE [App::DocumentObjectGroupPython] C_element148  label="C_element : 093"  # scripted group (container) (typed FeaturePython)
  n = 10
  ref = C_element
FEATURE [App::DocumentObjectGroupPython] N_element068  label="N_element : 040"  # scripted group (container) (typed FeaturePython)
  n = 2
  ref = N_element
FEATURE [App::DocumentObjectGroupPython] O_element130  label="O_element : 081"  # scripted group (container) (typed FeaturePython)
  n = 9
  ref = O_element
FEATURE [App::DocumentObjectGroupPython] P_element019  label="P_element : 008"  # scripted group (container) (typed FeaturePython)
  n = 1
  ref = P_element
FEATURE [App::DocumentObjectGroupPython] G4_DNA_MU  # scripted group (container) (typed FeaturePython)
  Dunit = g/cm3
  Dvalue = 1
  Group = -> [H_element138,C_element148,N_element068,O_element130,P_element019]
  conduct = 2
  density = 1
  expand = 3
  formula = G4_DNA_MU
  name = G4_DNA_MU
  specific = 4
FEATURE [App::DocumentObjectGroupPython] BioChemical  # scripted group (container) (typed FeaturePython)
  Group = -> [G4_CYTOSINE,G4_THYMINE,G4_URACIL,G4_DNA_ADENINE,G4_DNA_GUANINE,G4_DNA_CYTOSINE,G4_DNA_THYMINE,G4_DNA_URACIL,G4_DNA_ADENOSINE,G4_DNA_GUANOSINE,G4_DNA_CYTIDINE,G4_DNA_URIDINE,G4_DNA_METHYLURIDINE,G4_DNA_MONOPHOSPHATE,G4_DNA_A,G4_DNA_G,G4_DNA_C,G4_DNA_U,G4_DNA_MU]
FEATURE [App::DocumentObjectGroupPython] G4Materials  # scripted group (container) (typed FeaturePython)
  Group = -> [NIST,Element,HEP,Space,BioChemical]
  version = 1
FEATURE [App::DocumentObjectGroupPython] Geant4  # scripted group (container) (typed FeaturePython)
  Group = -> [G4Isotopes,G4Elements,G4Materials]
FEATURE [App::DocumentObjectGroupPython] Materials  # scripted group (container) (typed FeaturePython)
  Group = -> [Geant4]
FEATURE [Part::FeaturePython] GDMLBox_WorldBox  # WARN: FeaturePython — macro-defined, semantics opaque (R4)
  lunit = 2
  material = 5
  x = 273
  y = 273
  z = 130
FEATURE [Part::FeaturePython] GDMLBox_Box  # WARN: FeaturePython — macro-defined, semantics opaque (R4)
  lunit = 2
  material = 0
  x = 10
  y = 10
  z = 10
FEATURE [Part::FeaturePython] Array  # Draft array (typed FeaturePython)
  AlwaysSyncPlacement = false
  Angle = 360
  ArrayType = 0
  Axis = (0,0,1)
  Base = -> GDMLBox_Box
  Center = (0,0,0)
  Count = 4
  ExpandArray = false
  Fuse = false
  IntervalAxis = (0,0,0)
  IntervalX = (100,0,0)
  IntervalY = (0,100,0)
  IntervalZ = (0,0,100)
  NumberCircles = 3
  NumberPolar = 5
  NumberX = 2
  NumberY = 2
  NumberZ = 1
  PlacementList = 4 placements: [(0,0,0),(0,100,0),(100,0,0),(100,100,0)]
  RadialDistance = 50
  ScaleList = (4) [(1,1,1),(1,1,1),(1,1,1),(1,1,1)]
  Symmetry = 1
  TangentialDistance = 25
FEATURE [App::Part] Part  label="experiment"
  Group = -> [Array]
  Origin = -> Origin001
FEATURE [App::Part] worldVOL
  Group = -> [GDMLBox_WorldBox,Part]
  Origin = -> Origin
